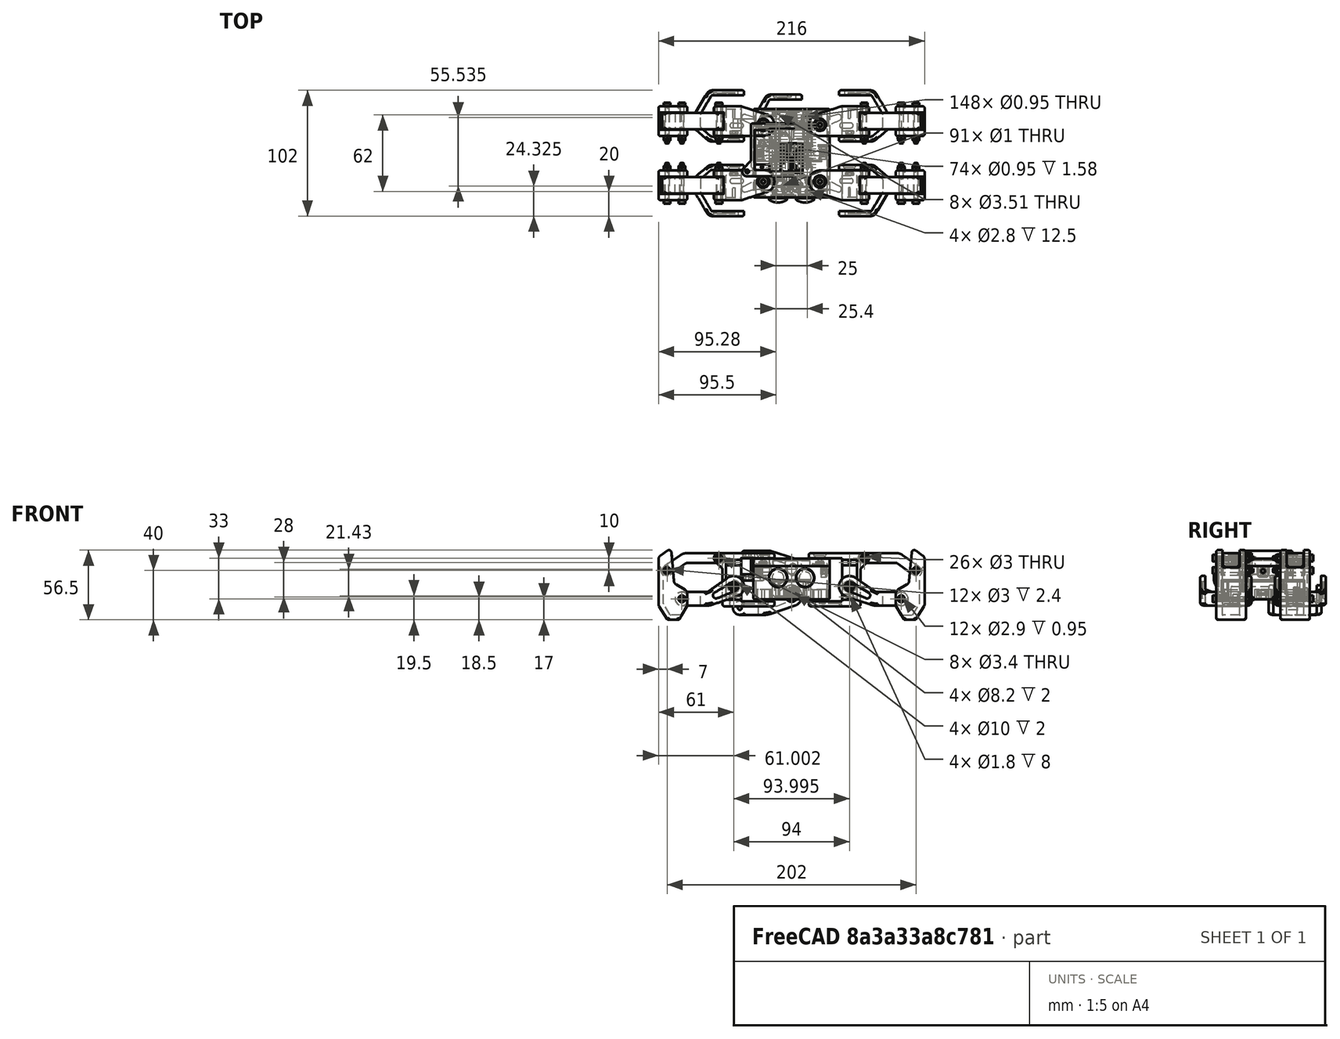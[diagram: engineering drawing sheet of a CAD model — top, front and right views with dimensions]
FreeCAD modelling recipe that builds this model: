
FCSTD DOCUMENT  (FreeCAD 1.0R39109 (Git))
Label: kame32
License: All rights reserved
LicenseURL: http://en.wikipedia.org/wiki/All_rights_reserved
objects: Sketcher::SketchObject×74, Part::FeaturePython×56, PartDesign::Pocket×54, PartDesign::Pad×23, PartDesign::Fillet×20, Part::Feature×14, PartDesign::Body×9, PartDesign::Chamfer×4, App::DocumentObjectGroup×4, PartDesign::Thickness×1, Part::MultiFuse×1, Part::Box×1, Part::Fillet×1, App::Part×1
note: 536 computed .brp shape members not serialized (recipe doc carries the construction recipe); baked Part::Feature solids carry a one-line shape summary decoded from their .brp

FEATURE [Sketcher::SketchObject] Sketch032
  ArcFitTolerance = 0
  AttachmentOffset = pos=(0,-0.5,0) rot=(0,0,1;0rad)
  AttachmentSupport = -> [XZ_Plane001]
  FullyConstrained = true
  MakeInternals = false
  MapMode = 5
  Placement = pos=(0,-1e-16,-0.5) rot=(1,0,0;1.5708rad)
  sketch-geometry (10):
    g0: ArcOfCircle CenterX=-42 CenterY=-10 CenterZ=0 NormalX=0 NormalY=0 NormalZ=1 AngleXU=0 Radius=5.5 StartAngle=1.5708 EndAngle=4.71239
    g1: ArcOfCircle CenterX=0 CenterY=0 CenterZ=0 NormalX=0 NormalY=0 NormalZ=1 AngleXU=0 Radius=8.5 StartAngle=5.03312 EndAngle=8.46485
    g2: LineSegment StartX=-42 StartY=-4.5 StartZ=0 EndX=-21.7189 EndY=-4.5 EndZ=0
    g3: LineSegment StartX=-20.8585 StartY=-4.22873 StartZ=0 EndX=-4.8754 EndY=6.96279 EndZ=0
    g4: LineSegment StartX=2.67968 StartY=-8.06656 StartZ=0 EndX=-17.7782 EndY=-14.8626 EndZ=0
    g5: LineSegment StartX=-21.7189 StartY=-15.5 StartZ=0 EndX=-42 EndY=-15.5 EndZ=0
    g6: Circle CenterX=-42 CenterY=-10 CenterZ=0 NormalX=0 NormalY=0 NormalZ=1 AngleXU=0 Radius=1.7
    g7: Circle CenterX=0 CenterY=0 CenterZ=0 NormalX=0 NormalY=0 NormalZ=1 AngleXU=0 Radius=1.7
    g8: ArcOfCircle CenterX=-21.7189 CenterY=-3 CenterZ=0 NormalX=0 NormalY=0 NormalZ=1 AngleXU=0 Radius=12.5 StartAngle=4.71239 EndAngle=5.03312
    g9: ArcOfCircle CenterX=-21.7189 CenterY=-3 CenterZ=0 NormalX=0 NormalY=0 NormalZ=1 AngleXU=0 Radius=1.5 StartAngle=4.71239 EndAngle=5.32325
  constraints (22):
    c: Tangent(g0,g2) = 1.5708
    c: Tangent(g1,g4) = 1.5708
    c: Horizontal(g5)
    c: Radius(g0) = 5.5
    c: Horizontal(g2)
    c: Tangent(g5,g0) = 1.5708
    c: Coincident(g6,g0)
    c: Radius(g6) = 1.7
    c: Radius(g1) = 8.5
    c: DistanceX(g0,g1) = 42
    c: DistanceY(g0,g1) = 10
    c: Coincident(g7,g1)
    c: Equal(g7,g6)
    c: Tangent(g3,g1) = 1.5708
    c: Coincident(g1,g-1)
    c: Tangent(g8,g5) = 1.5708
    c: Tangent(g8,g4) = 1.5708
    c: Coincident(g9,g8)
    c: Tangent(g9,g3) = -1.5708
    c: Tangent(g9,g2) = -1.5708
    c: Radius(g9) = 1.5
    c: Angle(g3,g2) = 2.53073
FEATURE [PartDesign::Pad] Pad017
  Direction = (0,-1,2e-16)
  Length = 50
  Length2 = 10
  Placement = pos=(0,0,0) rot=(1,0,0;1.5708rad)
  Profile = -> Sketch032
  ReferenceAxis = -> Sketch032 [N_Axis]
  Refine = true
  Reversed = true
  Suppressed = false
  Type = 0
FEATURE [Sketcher::SketchObject] Sketch033
  ArcFitTolerance = 0
  AttachmentSupport = -> [Pad017]
  ExternalGeometry = -> [Pad017]
  FullyConstrained = true
  MakeInternals = false
  MapMode = 5
  Placement = pos=(0,-7e-15,-16) rot=(1,0,0;3.14159rad)
  sketch-geometry (31):
    g0: LineSegment StartX=-54 StartY=-14.25 StartZ=0 EndX=-31.4689 EndY=-14.25 EndZ=0
    g1: LineSegment StartX=-30.8158 StartY=-14.0072 StartZ=0 EndX=-21.7189 EndY=-6.16102 EndZ=0
    g2: LineSegment StartX=-17.25 StartY=-4.5 StartZ=0 EndX=11 EndY=-4.5 EndZ=0
    g3: LineSegment StartX=11 StartY=-4.5 StartZ=0 EndX=11 EndY=-8.5 EndZ=0
    g4: LineSegment StartX=11 StartY=-8.5 StartZ=0 EndX=-17.25 EndY=-8.5 EndZ=0
    g5: LineSegment StartX=-19.1064 StartY=-9.18998 StartZ=0 EndX=-26.6531 EndY=-15.6992 EndZ=0
    g6: LineSegment StartX=-27 StartY=-16.4565 StartZ=0 EndX=-27 EndY=-26.2161 EndZ=0
    g7: LineSegment StartX=-26.8632 StartY=-26.721 StartZ=0 EndX=-18.2663 EndY=-41.4171 EndZ=0
    g8: LineSegment StartX=-17.25 StartY=-42 StartZ=0 EndX=11 EndY=-42 EndZ=0
    g9: LineSegment StartX=11 StartY=-42 StartZ=0 EndX=11 EndY=-46 EndZ=0
    g10: LineSegment StartX=11 StartY=-46 StartZ=0 EndX=-17.25 EndY=-46 EndZ=0
    g11: LineSegment StartX=-21.7189 StartY=-43.4368 StartZ=0 EndX=-30.6058 EndY=-28.2451 EndZ=0
    g12: LineSegment StartX=-31.4689 StartY=-27.75 StartZ=0 EndX=-54 EndY=-27.75 EndZ=0
    g13: LineSegment [constr] StartX=-54 StartY=-27.75 StartZ=0 EndX=-54 EndY=-14.25 EndZ=0
    g14: LineSegment [constr] StartX=11 StartY=-8.5 StartZ=0 EndX=11 EndY=-42 EndZ=0
    g15: ArcOfCircle CenterX=-31.4689 CenterY=-13.25 CenterZ=0 NormalX=0 NormalY=0 NormalZ=1 AngleXU=0 Radius=1 StartAngle=4.71239 EndAngle=5.42411
    g16: ArcOfCircle CenterX=-17.25 CenterY=-11.3422 CenterZ=0 NormalX=0 NormalY=0 NormalZ=1 AngleXU=0 Radius=6.84224 StartAngle=1.5708 EndAngle=2.28251
    g17: ArcOfCircle CenterX=-17.25 CenterY=-11.3422 CenterZ=0 NormalX=0 NormalY=0 NormalZ=1 AngleXU=0 Radius=2.84224 StartAngle=1.5708 EndAngle=2.28251
    g18: ArcOfCircle CenterX=-17.25 CenterY=-40.8226 CenterZ=0 NormalX=0 NormalY=0 NormalZ=1 AngleXU=0 Radius=1.17738 StartAngle=3.67089 EndAngle=4.71239
    g19: ArcOfCircle CenterX=-17.25 CenterY=-40.8226 CenterZ=0 NormalX=0 NormalY=0 NormalZ=1 AngleXU=0 Radius=5.17738 StartAngle=3.67089 EndAngle=4.71239
    g20: ArcOfCircle CenterX=-26 CenterY=-16.4565 CenterZ=0 NormalX=0 NormalY=0 NormalZ=1 AngleXU=0 Radius=1 StartAngle=2.28251 EndAngle=3.14159
    g21: ArcOfCircle CenterX=-26 CenterY=-26.2161 CenterZ=0 NormalX=0 NormalY=0 NormalZ=1 AngleXU=0 Radius=1 StartAngle=3.14159 EndAngle=3.67089
    g22: ArcOfCircle CenterX=-31.4689 CenterY=-28.75 CenterZ=0 NormalX=0 NormalY=0 NormalZ=1 AngleXU=0 Radius=1 StartAngle=0.5293 EndAngle=1.5708
    g23: LineSegment StartX=-54 StartY=-14.25 StartZ=0 EndX=-54 EndY=20 EndZ=0
    g24: LineSegment StartX=-54 StartY=20 StartZ=0 EndX=26 EndY=20 EndZ=0
    g25: LineSegment StartX=26 StartY=-60 StartZ=0 EndX=-54 EndY=-60 EndZ=0
    g26: LineSegment StartX=-54 StartY=-60 StartZ=0 EndX=-54 EndY=-27.75 EndZ=0
    g27: LineSegment StartX=26 StartY=20 StartZ=0 EndX=26 EndY=-60 EndZ=0
    g28: LineSegment [constr] StartX=-31.4689 StartY=-14.25 StartZ=0 EndX=-31.4689 EndY=-27.75 EndZ=0
    g29: LineSegment [constr] StartX=-21.7189 StartY=-6.16102 StartZ=0 EndX=-21.7189 EndY=-43.4368 EndZ=0
    g30: LineSegment [constr] StartX=-17.25 StartY=-4.5 StartZ=0 EndX=-17.25 EndY=-46 EndZ=0
  constraints (80):
    c: Coincident(g25,g26)
    c: Coincident(g12,g26)
    c: Coincident(g0,g23)
    c: Coincident(g23,g24)
    c: Coincident(g4,g17)
    c: Coincident(g2,g16)
    c: Coincident(g9,g10)
    c: Coincident(g8,g9)
    c: Coincident(g3,g4)
    c: Coincident(g2,g3)
    c: Coincident(g25,g27)
    c: Coincident(g24,g27)
    c: Coincident(g0,g13)
    c: Coincident(g12,g13)
    c: Tangent(g7,g18) = -1.5708
    c: Tangent(g11,g19) = 1.5708
    c: Coincident(g18,g19)
    c: Tangent(g8,g18) = -1.5708
    c: Tangent(g10,g19) = 1.5708
    c: Coincident(g16,g17)
    c: Equal(g9,g3)
    c: Distance(g3) = 4
    c: Horizontal(g2)
    c: Horizontal(g4)
    c: Horizontal(g8)
    c: Horizontal(g10)
    c: Horizontal(g12)
    c: Horizontal(g0)
    c: Horizontal(g24)
    c: Horizontal(g25)
    c: Vertical(g23)
    c: Vertical(g13)
    c: Vertical(g26)
    c: Vertical(g6)
    c: Vertical(g3)
    c: Vertical(g9)
    c: Equal(g15,g20)
    c: Equal(g15,g21)
    c: Equal(g15,g22)
    c: Radius(g15) = 1
    c: Tangent(g12,g22) = -1.5708
    c: Tangent(g11,g22) = -1.5708
    c: Tangent(g7,g21) = -1.5708
    c: Tangent(g6,g21) = -1.5708
    c: Tangent(g5,g20) = -1.5708
    c: Tangent(g6,g20) = -1.5708
    c: Tangent(g1,g15) = -1.5708
    c: Tangent(g0,g15) = -1.5708
    c: Tangent(g5,g17) = -1.5708
    c: Tangent(g1,g16) = 1.5708
    c: Parallel(g1,g5)
    c: Parallel(g7,g11)
    c: Distance(g13) = 13.5
    c: Coincident(g3,g14)
    c: Vertical(g14)
    c: Equal(g25,g27)
    c: Distance(g27) = 80
    c: Vertical(g27)
    c: DistanceX(g-2,g23) = -54
    c: DistanceX(g-2,g2) = 11
    c: Distance(g14) = 33.5
    c: Coincident(g14,g8)
    c: Coincident(g28,g0)
    c: Coincident(g28,g12)
    c: Vertical(g28)
    c: DistanceY(g-1,g0) = -14.25
    c: DistanceY(g-1,g3) = -8.5
    c: Distance(g6,g27) = 53
    c: DistanceY(g-1,g23) = 20
    c: Coincident(g29,g1)
    c: Coincident(g29,g11)
    c: Vertical(g29)
    c: Coincident(g30,g2)
    c: Coincident(g30,g10)
    c: Vertical(g30)
    c: PointOnObject(g16,g30)
    c: PointOnObject(g4,g30)
    c: PointOnObject(g1,g-3)
    c: DistanceX(g-2,g2) = -17.25
    c: Distance(g0,g29) = 9.75
FEATURE [PartDesign::Pocket] Pocket012
  BaseFeature = -> Pad017
  Direction = (0,0,1)
  Length = 40
  Length2 = 5
  Placement = pos=(0,0,0) rot=(1,0,0;1.5708rad)
  Profile = -> Sketch033
  ReferenceAxis = -> Sketch033 [N_Axis]
  Refine = true
  Suppressed = false
  Type = 0
FEATURE [Sketcher::SketchObject] Sketch007
  ArcFitTolerance = 0
  FullyConstrained = true
  MakeInternals = false
  MapMode = 5
  Placement = pos=(0,19.25,0) rot=(0,0.707107,0.707107;3.14159rad)
  sketch-geometry (10):
    g0: ArcOfCircle CenterX=12 CenterY=22 CenterZ=0 NormalX=0 NormalY=0 NormalZ=1 AngleXU=0 Radius=4 StartAngle=1.5708 EndAngle=4.71239
    g1: LineSegment StartX=12 StartY=26 StartZ=0 EndX=38.4573 EndY=26 EndZ=0
    g2: LineSegment StartX=43.0459 StartY=24.5532 StartZ=0 EndX=56.2943 EndY=15.2766 EndZ=0
    g3: LineSegment StartX=12 StartY=18 StartZ=0 EndX=37.9844 EndY=18 EndZ=0
    g4: LineSegment StartX=38.8447 StartY=17.7287 StartZ=0 EndX=51.7057 EndY=8.72338 EndZ=0
    g5: ArcOfCircle CenterX=54 CenterY=12 CenterZ=0 NormalX=0 NormalY=0 NormalZ=1 AngleXU=0 Radius=4 StartAngle=4.10153 EndAngle=7.24312
    g6: Circle CenterX=12 CenterY=22 CenterZ=0 NormalX=0 NormalY=0 NormalZ=1 AngleXU=0 Radius=1.7
    g7: Circle CenterX=54 CenterY=12 CenterZ=0 NormalX=0 NormalY=0 NormalZ=1 AngleXU=0 Radius=1.7
    g8: ArcOfCircle CenterX=38.4573 CenterY=18 CenterZ=0 NormalX=0 NormalY=0 NormalZ=1 AngleXU=0 Radius=8 StartAngle=0.959931 EndAngle=1.5708
    g9: ArcOfCircle CenterX=37.9844 CenterY=16.5 CenterZ=0 NormalX=0 NormalY=0 NormalZ=1 AngleXU=0 Radius=1.5 StartAngle=0.959931 EndAngle=1.5708
  constraints (26):
    c: Tangent(g0,g1) = 1.5708
    c: Tangent(g0,g3) = -1.5708
    c: Coincident(g5,g2)
    c: Coincident(g5,g4)
    c: Tangent(g2,g5)
    c: Tangent(g4,g5)
    c: Parallel(g1,g3)
    c: Parallel(g2,g4)
    c: Horizontal(g1)
    c: Radius(g0) = 4
    c: Equal(g0,g5)
    c: Coincident(g6,g0)
    c: Coincident(g7,g5)
    c: Radius(g6) = 1.7
    c: Equal(g6,g7)
    c: Angle(g1,g2) = 2.53073
    c: DistanceY(g0,g5) = -10  'z_length'
    c: DistanceX(g0,g5) = 42  'x_legth'
    c: DistanceX(g-2,g0) = 12
    c: DistanceY(g-1,g0) = 22
    c: Tangent(g1,g8) = 1.5708
    c: Tangent(g2,g8) = 1.5708
    c: Tangent(g3,g9) = 1.5708
    c: Tangent(g4,g9) = 1.5708
    c: Radius(g8) = 8
    c: Radius(g9) = 1.5
FEATURE [PartDesign::Pad] Pad019
  Direction = (1e-16,1,-2e-16)
  Length = 13.5
  Length2 = 10
  Placement = pos=(0,19.25,0) rot=(0,0.707107,0.707107;3.14159rad)
  Profile = -> Sketch007
  ReferenceAxis = -> Sketch007 [N_Axis]
  Refine = true
  Suppressed = false
  Type = 0
FEATURE [PartDesign::Fillet] Fillet006
  Base = -> Pad019 [Edge24,Edge23]
  BaseFeature = -> Pad019
  Placement = pos=(0,19.25,0) rot=(0,0.707107,0.707107;3.14159rad)
  Radius = 1.5
  Refine = true
  SupportTransform = false
  Suppressed = false
  UseAllEdges = false
FEATURE [Sketcher::SketchObject] Sketch035
  ArcFitTolerance = 0
  AttachmentSupport = -> [Fillet006]
  ExternalGeometry = -> [Fillet006]
  FullyConstrained = true
  MakeInternals = false
  MapMode = 5
  Placement = pos=(0,32.75,-4.7e-15) rot=(0,0.707107,0.707107;3.14159rad)
  sketch-geometry (4):
    g0: Circle CenterX=12 CenterY=22 CenterZ=0 NormalX=0 NormalY=0 NormalZ=1 AngleXU=0 Radius=1.7
    g1: Circle CenterX=54 CenterY=12 CenterZ=0 NormalX=0 NormalY=0 NormalZ=1 AngleXU=0 Radius=1.7
    g2: Circle CenterX=54 CenterY=12 CenterZ=0 NormalX=0 NormalY=0 NormalZ=1 AngleXU=0 Radius=4
    g3: Circle CenterX=12 CenterY=22 CenterZ=0 NormalX=0 NormalY=0 NormalZ=1 AngleXU=0 Radius=4
  constraints (8):
    c: Coincident(g0,g-5)
    c: Equal(g-3,g0)
    c: Equal(g-4,g1)
    c: Coincident(g2,g1)
    c: PointOnObject(g-6,g2)
    c: Coincident(g3,g0)
    c: PointOnObject(g-5,g3)
    c: Coincident(g-6,g1)
FEATURE [PartDesign::Pad] Pad020
  BaseFeature = -> Fillet006
  Direction = (0,1,-2e-16)
  Length = 13.5
  Length2 = 10
  Placement = pos=(0,19.25,0) rot=(0,0.707107,0.707107;3.14159rad)
  Profile = -> Sketch035
  ReferenceAxis = -> Sketch035 [N_Axis]
  Refine = true
  Reversed = true
  Suppressed = false
  Type = 0
FEATURE [PartDesign::Body] Body002  label="leg-link"
  AllowCompound = false
  Group = -> [Sketch007,Pad019,Fillet006,Sketch035,Pad020]
  Origin = -> Origin002
  Placement = pos=(0,-5,0) rot=(0,0,1;0rad)
  Tip = -> Pad020
FEATURE [Sketcher::SketchObject] Sketch036
  ArcFitTolerance = 0
  AttachmentSupport = -> [XZ_Plane003]
  FullyConstrained = true
  MakeInternals = false
  MapMode = 5
  Placement = pos=(0,0,0) rot=(1,0,0;1.5708rad)
  sketch-geometry (19):
    g0: Circle CenterX=-54 CenterY=12.5 CenterZ=0 NormalX=0 NormalY=0 NormalZ=1 AngleXU=0 Radius=1.5
    g1: Circle CenterX=-42 CenterY=-10.5 CenterZ=0 NormalX=0 NormalY=0 NormalZ=1 AngleXU=0 Radius=1.5
    g2: LineSegment StartX=-59.2943 StartY=24.6841 StartZ=0 EndX=-53.6472 EndY=28.6383 EndZ=0
    g3: LineSegment StartX=-37.5 StartY=-6.5 StartZ=0 EndX=-37.5 EndY=-14.5 EndZ=0
    g4: LineSegment StartX=-38.041 StartY=-16.5089 StartZ=0 EndX=-44.1353 EndY=-27.0022 EndZ=0
    g5: LineSegment StartX=-45 StartY=-27.5 StartZ=0 EndX=-53 EndY=-27.5 EndZ=0
    g6: LineSegment StartX=-53.8466 StartY=-27.0322 StartZ=0 EndX=-60.3865 EndY=-16.6288 EndZ=0
    g7: LineSegment StartX=-61 StartY=-14.5 StartZ=0 EndX=-61 EndY=21.4075 EndZ=0
    g8: ArcOfCircle CenterX=-52.5 CenterY=27 CenterZ=0 NormalX=0 NormalY=0 NormalZ=1 AngleXU=0 Radius=2 StartAngle=0.0872665 EndAngle=2.18166
    g9: ArcOfCircle CenterX=-41.5 CenterY=-6.5 CenterZ=0 NormalX=0 NormalY=0 NormalZ=1 AngleXU=0 Radius=4 StartAngle=0 EndAngle=1.0472
    g10: ArcOfCircle CenterX=-41.5 CenterY=-14.5 CenterZ=0 NormalX=0 NormalY=0 NormalZ=1 AngleXU=0 Radius=4 StartAngle=5.75703 EndAngle=6.28319
    g11: ArcOfCircle CenterX=-57 CenterY=-14.5 CenterZ=0 NormalX=0 NormalY=0 NormalZ=1 AngleXU=0 Radius=4 StartAngle=3.14159 EndAngle=3.7028
    g12: ArcOfCircle CenterX=-57 CenterY=21.4075 CenterZ=0 NormalX=0 NormalY=0 NormalZ=1 AngleXU=0 Radius=4 StartAngle=2.18166 EndAngle=3.14159
    g13: ArcOfCircle CenterX=-45 CenterY=-26.5 CenterZ=0 NormalX=0 NormalY=0 NormalZ=1 AngleXU=0 Radius=1 StartAngle=4.71239 EndAngle=5.75703
    g14: ArcOfCircle CenterX=-53 CenterY=-26.5 CenterZ=0 NormalX=0 NormalY=0 NormalZ=1 AngleXU=0 Radius=1 StartAngle=3.7028 EndAngle=4.71239
    g15: LineSegment StartX=-50.5076 StartY=27.1743 StartZ=0 EndX=-48.491 EndY=4.12464 EndZ=0
    g16: LineSegment StartX=-39.5 StartY=-3.0359 StartZ=0 EndX=-46.5062 EndY=1.00916 EndZ=0
    g17: ArcOfCircle CenterX=-44.5062 CenterY=4.47326 CenterZ=0 NormalX=0 NormalY=0 NormalZ=1 AngleXU=0 Radius=4 StartAngle=3.22886 EndAngle=4.18879
    g18: LineSegment [constr] StartX=-61 StartY=-14.5 StartZ=0 EndX=-37.5 EndY=-14.5 EndZ=0
  constraints (48):
    c: Equal(g1,g0)
    c: Radius(g1) = 1.5
    c: DistanceX(g0,g1) = 12
    c: Vertical(g3)
    c: Horizontal(g5)
    c: Vertical(g7)
    c: Tangent(g2,g8) = 1.5708
    c: Tangent(g3,g9) = 1.5708
    c: Tangent(g3,g10) = 1.5708
    c: Tangent(g4,g10) = 1.5708
    c: Tangent(g6,g11) = 1.5708
    c: Tangent(g7,g11) = 1.5708
    c: Tangent(g2,g12) = 1.5708
    c: Tangent(g7,g12) = 1.5708
    c: Tangent(g5,g13) = 1.5708
    c: Tangent(g4,g13) = 1.5708
    c: Tangent(g6,g14) = 1.5708
    c: Tangent(g5,g14) = 1.5708
    c: Equal(g14,g13)
    c: Radius(g14) = 1
    c: Distance(g5) = 8
    c: Distance(g3,g7) = 23.5
    c: Angle(g-1,g2) = 0.610865
    c: Radius(g8) = 2
    c: Distance(g3) = 8
    c: Distance(g0,g7) = 7
    c: Tangent(g15,g17) = -1.5708
    c: Tangent(g16,g17) = 1.5708
    c: Tangent(g15,g8) = 1.5708
    c: Tangent(g16,g9) = -1.5708
    c: DistanceX(g5,g1) = 3
    c: Coincident(g18,g7)
    c: Coincident(g18,g3)
    c: Horizontal(g18)
    c: Equal(g10,g11)
    c: Equal(g11,g9)
    c: Radius(g9) = 4
    c: Equal(g17,g12)
    c: Angle(g-1,g15) = 1.65806
    c: Angle(g-1,g16) = 2.61799
    c: DistanceX(g0,g8) = 1.5
    c: Equal(g9,g17)
    c: DistanceX(g-2,g1) = -42
    c: DistanceY(g-1,g0) = 12.5
    c: DistanceY(g-1,g8) = 27
    c: DistanceY(g-1,g5) = -27.5
    c: DistanceY(g-1,g11) = -14.5
    c: DistanceY(g-1,g1) = -10.5
FEATURE [PartDesign::Pad] Pad021
  Direction = (0,-1,2e-16)
  Length = 24
  Length2 = 10
  Placement = pos=(0,0,0) rot=(1,0,0;1.5708rad)
  Profile = -> Sketch036
  ReferenceAxis = -> Sketch036 [N_Axis]
  Refine = true
  Suppressed = false
  Type = 0
FEATURE [PartDesign::Fillet] Fillet007
  Base = -> Pad021 [Edge6,Edge7]
  BaseFeature = -> Pad021
  Placement = pos=(0,0,0) rot=(1,0,0;1.5708rad)
  Radius = 1.5
  Refine = true
  SupportTransform = false
  Suppressed = false
  UseAllEdges = false
FEATURE [Sketcher::SketchObject] Sketch037
  ArcFitTolerance = 0
  AttachmentOffset = pos=(0,0,-5) rot=(0,0,1;0rad)
  AttachmentSupport = -> [Fillet007]
  ExternalGeometry = -> [Fillet007]
  FullyConstrained = true
  MakeInternals = false
  MapMode = 5
  Placement = pos=(0,-19,4.2e-15) rot=(1,0,0;1.5708rad)
  sketch-geometry (15):
    g0: LineSegment StartX=-37.4756 StartY=-23.5 StartZ=0 EndX=-51.3424 EndY=-23.5 EndZ=0
    g1: LineSegment StartX=-51.3424 StartY=-23.5 StartZ=0 EndX=-57 EndY=-14.5 EndZ=0
    g2: LineSegment StartX=-57 StartY=-14.5 StartZ=0 EndX=-57 EndY=8.5 EndZ=0
    g3: LineSegment StartX=-79 StartY=15 StartZ=0 EndX=-79 EndY=35 EndZ=0
    g4: LineSegment StartX=-79 StartY=35 StartZ=0 EndX=-15.7333 EndY=35 EndZ=0
    g5: LineSegment StartX=-15.7333 StartY=35 StartZ=0 EndX=-15.7333 EndY=-20.5 EndZ=0
    g6: LineSegment StartX=-15.7333 StartY=-20.5 StartZ=0 EndX=-35.7333 EndY=-20.5 EndZ=0
    g7: LineSegment StartX=-35.7333 StartY=-20.5 StartZ=0 EndX=-37.4756 EndY=-23.5 EndZ=0
    g8: LineSegment [constr] StartX=-51.3424 StartY=-23.5 StartZ=0 EndX=-54.7288 EndY=-25.6288 EndZ=0
    g9: LineSegment [constr] StartX=-51.3424 StartY=-23.5 StartZ=0 EndX=-51.3424 EndY=-27.5 EndZ=0
    g10: LineSegment [constr] StartX=-37.4756 StartY=-23.5 StartZ=0 EndX=-40.9346 EndY=-21.4911 EndZ=0
    g11: LineSegment [constr] StartX=-61 StartY=-14.5 StartZ=0 EndX=-57 EndY=-14.5 EndZ=0
    g12: ArcOfCircle CenterX=-54 CenterY=12.5 CenterZ=0 NormalX=0 NormalY=0 NormalZ=1 AngleXU=0 Radius=5 StartAngle=3.14159 EndAngle=4.06889
    g13: LineSegment StartX=-59 StartY=12.5 StartZ=0 EndX=-59 EndY=15 EndZ=0
    g14: LineSegment StartX=-59 StartY=15 StartZ=0 EndX=-79 EndY=15 EndZ=0
  constraints (44):
    c: Horizontal(g0)
    c: Coincident(g0,g1)
    c: Coincident(g1,g2)
    c: Vertical(g2)
    c: Vertical(g3)
    c: Coincident(g3,g4)
    c: Horizontal(g4)
    c: Coincident(g4,g5)
    c: Vertical(g5)
    c: Coincident(g5,g6)
    c: Horizontal(g6)
    c: Coincident(g6,g7)
    c: Coincident(g7,g0)
    c: Parallel(g1,g-7)
    c: Coincident(g8,g0)
    c: PointOnObject(g8,g-7)
    c: Coincident(g9,g0)
    c: PointOnObject(g9,g-9)
    c: Vertical(g9)
    c: Coincident(g10,g0)
    c: PointOnObject(g10,g-11)
    c: Coincident(g11,g-6)
    c: PointOnObject(g11,g2)
    c: Horizontal(g11)
    c: Equal(g11,g8)
    c: Equal(g8,g9)
    c: Equal(g9,g10)
    c: Perpendicular(g-7,g8)
    c: Perpendicular(g-11,g10)
    c: Parallel(g7,g-11)
    c: Distance(g11) = 4
    c: DistanceY(g-10,g6) = 7
    c: Coincident(g12,g-12)
    c: Coincident(g12,g2)
    c: Tangent(g12,g13) = 1.5708
    c: Coincident(g13,g14)
    c: Horizontal(g14)
    c: Coincident(g14,g3)
    c: Radius(g12) = 5
    c: Distance(g6) = 20
    c: Distance(g14) = 20
    c: Distance(g3) = 20
    c: Vertical(g13)
    c: DistanceY(g-9,g13) = 42.5
FEATURE [PartDesign::Pocket] Pocket013
  BaseFeature = -> Fillet007
  Direction = (0,1,-2e-16)
  Length = 14
  Length2 = 5
  Placement = pos=(0,0,0) rot=(1,0,0;1.5708rad)
  Profile = -> Sketch037
  ReferenceAxis = -> Sketch037 [N_Axis]
  Refine = true
  Suppressed = false
  Type = 0
FEATURE [PartDesign::Fillet] Fillet008
  Base = -> Pocket013 [Edge79,Edge33,Edge80,Edge81,Edge82]
  BaseFeature = -> Pocket013
  Placement = pos=(0,0,0) rot=(1,0,0;1.5708rad)
  Radius = 0.5
  Refine = true
  SupportTransform = false
  Suppressed = false
  UseAllEdges = false
FEATURE [PartDesign::Body] Body003  label="foot"
  AllowCompound = false
  Group = -> [Sketch036,Pad021,Fillet007,Sketch037,Pocket013,Fillet008]
  Origin = -> Origin003
  Placement = pos=(0,33,0) rot=(0,0,1;0rad)
  Tip = -> Fillet008
FEATURE [Sketcher::SketchObject] Sketch056
  ArcFitTolerance = 0
  AttachmentSupport = -> [XY_Plane006]
  FullyConstrained = true
  MakeInternals = false
  MapMode = 5
  sketch-geometry (5):
    g0: ArcOfCircle CenterX=0 CenterY=0 CenterZ=0 NormalX=0 NormalY=0 NormalZ=1 AngleXU=0 Radius=9 StartAngle=4.71239 EndAngle=7.5465
    g1: LineSegment StartX=2.72391 StartY=8.5779 StartZ=0 EndX=-17.5 EndY=15 EndZ=0
    g2: LineSegment StartX=-17.5 StartY=15 StartZ=0 EndX=-33 EndY=15 EndZ=0
    g3: LineSegment StartX=-33 StartY=15 StartZ=0 EndX=-33 EndY=-9 EndZ=0
    g4: LineSegment StartX=-33 StartY=-9 StartZ=0 EndX=0 EndY=-9 EndZ=0
  constraints (13):
    c: Coincident(g0,g-1)
    c: Tangent(g0,g1) = -1.5708
    c: Coincident(g1,g2)
    c: Horizontal(g2)
    c: Coincident(g2,g3)
    c: Vertical(g3)
    c: Coincident(g3,g4)
    c: Horizontal(g4)
    c: Tangent(g4,g0) = -1.5708
    c: Radius(g0) = 9
    c: Distance(g3) = 24
    c: Distance(g4) = 33
    c: Distance(g2) = 15.5
FEATURE [PartDesign::Pad] Pad025
  Direction = (0,0,1)
  Length = 43
  Length2 = 10
  Profile = -> Sketch056
  ReferenceAxis = -> Sketch056 [N_Axis]
  Refine = true
  Suppressed = false
  Type = 0
FEATURE [Sketcher::SketchObject] Sketch057
  ArcFitTolerance = 0
  AttachmentSupport = -> [Pad025]
  ExternalGeometry = -> [Pad025]
  FullyConstrained = false
  MakeInternals = false
  MapMode = 5
  Placement = pos=(0,-9,0) rot=(1,0,0;1.5708rad)
  sketch-geometry (5):
    g0: Circle CenterX=-35.9977 CenterY=39 CenterZ=0 NormalX=0 NormalY=0 NormalZ=1 AngleXU=0 Radius=1.5
    g1: ArcOfCircle CenterX=-35.9977 CenterY=39 CenterZ=0 NormalX=0 NormalY=0 NormalZ=1 AngleXU=0 Radius=4 StartAngle=1.57403 EndAngle=3.9468
    g2: LineSegment StartX=-36.0107 StartY=43 StartZ=0 EndX=-33 EndY=43 EndZ=0
    g3: LineSegment StartX=-33 StartY=43 StartZ=0 EndX=-33 EndY=30.3465 EndZ=0
    g4: LineSegment StartX=-38.7696 StartY=36.1161 StartZ=0 EndX=-33 EndY=30.3465 EndZ=0
  constraints (11):
    c: Coincident(g1,g0)
    c: Coincident(g2,g1)
    c: Coincident(g2,g-3)
    c: Horizontal(g2)
    c: Coincident(g3,g2)
    c: Vertical(g3)
    c: Coincident(g4,g1)
    c: Coincident(g4,g3)
    c: Angle(g3,g4) = 0.785398
    c: Radius(g1) = 4
    c: Radius(g0) = 1.5
FEATURE [PartDesign::Pad] Pad026
  BaseFeature = -> Pad025
  Direction = (0,-1,2e-16)
  Length = 24
  Length2 = 10
  Profile = -> Sketch057
  ReferenceAxis = -> Sketch057 [N_Axis]
  Refine = true
  Reversed = true
  Suppressed = false
  Type = 0
FEATURE [Sketcher::SketchObject] Sketch058
  ArcFitTolerance = 0
  AttachmentSupport = -> [Pad026]
  FullyConstrained = true
  MakeInternals = false
  MapMode = 5
  Placement = pos=(0,-9,0) rot=(1,0,0;1.5708rad)
  sketch-geometry (4):
    g0: LineSegment StartX=-18 StartY=4 StartZ=0 EndX=18 EndY=4 EndZ=0
    g1: LineSegment StartX=18 StartY=4 StartZ=0 EndX=18 EndY=39 EndZ=0
    g2: LineSegment StartX=18 StartY=39 StartZ=0 EndX=-18 EndY=39 EndZ=0
    g3: LineSegment StartX=-18 StartY=39 StartZ=0 EndX=-18 EndY=4 EndZ=0
  constraints (12):
    c: Coincident(g0,g1)
    c: Coincident(g1,g2)
    c: Coincident(g2,g3)
    c: Coincident(g3,g0)
    c: Horizontal(g0)
    c: Horizontal(g2)
    c: Vertical(g1)
    c: Vertical(g3)
    c: DistanceX(g-2,g2) = -18
    c: Distance(g3) = 35
    c: DistanceY(g-1,g0) = 4
    c: Distance(g2) = 36
FEATURE [PartDesign::Pocket] Pocket027
  BaseFeature = -> Pad026
  Direction = (0,1,-2e-16)
  Length = 30
  Length2 = 5
  Profile = -> Sketch058
  ReferenceAxis = -> Sketch058 [N_Axis]
  Refine = true
  Suppressed = false
  Type = 0
FEATURE [Sketcher::SketchObject] Sketch059
  ArcFitTolerance = 1e-06
  AttachmentSupport = -> [Pocket027]
  ExternalGeometry = -> [Pocket027]
  FullyConstrained = true
  MakeInternals = false
  MapMode = 5
  Placement = pos=(0,-9,0) rot=(1,0,0;1.5708rad)
  sketch-geometry (1):
    g0: Circle CenterX=-23.9977 CenterY=16 CenterZ=0 NormalX=0 NormalY=0 NormalZ=1 AngleXU=0 Radius=1.5
  constraints (3):
    c: DistanceX(g-3,g0) = 12
    c: DistanceY(g0,g-3) = 23
    c: Radius(g0) = 1.5
FEATURE [PartDesign::Pocket] Pocket028
  BaseFeature = -> Pocket027
  Direction = (0,1,-2e-16)
  Length = 35
  Length2 = 5
  Profile = -> Sketch059
  ReferenceAxis = -> Sketch059 [N_Axis]
  Refine = true
  Suppressed = false
  Type = 0
FEATURE [Sketcher::SketchObject] Sketch060
  ArcFitTolerance = 1e-06
  AttachmentSupport = -> [Pocket028]
  ExternalGeometry = -> [Pocket028]
  FullyConstrained = true
  MakeInternals = false
  MapMode = 5
  Placement = pos=(0,15,0) rot=(0,0.707107,0.707107;3.14159rad)
  sketch-geometry (4):
    g0: LineSegment StartX=18 StartY=33.2 StartZ=0 EndX=18 EndY=9.80002 EndZ=0
    g1: LineSegment StartX=18 StartY=9.80002 StartZ=0 EndX=30.2 EndY=9.80002 EndZ=0
    g2: LineSegment StartX=30.2 StartY=9.80002 StartZ=0 EndX=30.2 EndY=33.2 EndZ=0
    g3: LineSegment StartX=30.2 StartY=33.2 StartZ=0 EndX=18 EndY=33.2 EndZ=0
  constraints (12):
    c: Coincident(g0,g1)
    c: Coincident(g1,g2)
    c: Coincident(g2,g3)
    c: Coincident(g3,g0)
    c: Vertical(g0)
    c: Vertical(g2)
    c: Horizontal(g1)
    c: Horizontal(g3)
    c: PointOnObject(g0,g-3)
    c: Distance(g1) = 12.2
    c: Distance(g2) = 23.4
    c: Distance(g-4,g1) = 6.2
FEATURE [PartDesign::Pocket] Pocket029
  BaseFeature = -> Pocket028
  Direction = (0,-1,2e-16)
  Length = 20
  Length2 = 5
  Profile = -> Sketch060
  ReferenceAxis = -> Sketch060 [N_Axis]
  Refine = true
  Suppressed = false
  Type = 0
FEATURE [Sketcher::SketchObject] Sketch061
  ArcFitTolerance = 1e-06
  AttachmentSupport = -> [Pocket029]
  ExternalGeometry = -> [Pocket029]
  FullyConstrained = true
  MakeInternals = false
  MapMode = 5
  Placement = pos=(0,15,0) rot=(0,0.707107,0.707107;3.14159rad)
  sketch-geometry (6):
    g0: LineSegment StartX=30.2 StartY=37.7 StartZ=0 EndX=30.2 EndY=33.2 EndZ=0
    g1: LineSegment StartX=30.2 StartY=33.2 StartZ=0 EndX=30.2 EndY=9.80002 EndZ=0
    g2: LineSegment StartX=30.2 StartY=9.80002 StartZ=0 EndX=30.2 EndY=5.30002 EndZ=0
    g3: LineSegment StartX=30.2 StartY=5.30002 StartZ=0 EndX=18 EndY=5.30002 EndZ=0
    g4: LineSegment StartX=18 StartY=5.30002 StartZ=0 EndX=18 EndY=37.7 EndZ=0
    g5: LineSegment StartX=18 StartY=37.7 StartZ=0 EndX=30.2 EndY=37.7 EndZ=0
  constraints (16):
    c: Vertical(g0)
    c: Coincident(g0,g1)
    c: Coincident(g1,g2)
    c: Vertical(g2)
    c: Coincident(g2,g3)
    c: Horizontal(g3)
    c: Coincident(g3,g4)
    c: Vertical(g4)
    c: Coincident(g4,g5)
    c: Coincident(g5,g0)
    c: Horizontal(g5)
    c: Equal(g0,g2)
    c: Coincident(g0,g-3)
    c: PointOnObject(g-3,g4)
    c: Distance(g4) = 32.4
    c: Coincident(g-4,g1)
FEATURE [PartDesign::Pocket] Pocket030
  BaseFeature = -> Pocket029
  Direction = (0,-1,2e-16)
  Length = 2
  Length2 = 5
  Profile = -> Sketch061
  ReferenceAxis = -> Sketch061 [N_Axis]
  Refine = true
  Suppressed = false
  Type = 0
FEATURE [Sketcher::SketchObject] Sketch062
  ArcFitTolerance = 1e-06
  AttachmentSupport = -> [Pocket030]
  ExternalGeometry = -> [Pocket030]
  FullyConstrained = true
  MakeInternals = false
  MapMode = 5
  Placement = pos=(0,13,0) rot=(0,0.707107,0.707107;3.14159rad)
  sketch-geometry (5):
    g0: Circle CenterX=23.9977 CenterY=35.5 CenterZ=0 NormalX=0 NormalY=0 NormalZ=1 AngleXU=0 Radius=0.9
    g1: Circle CenterX=23.9977 CenterY=7.50002 CenterZ=0 NormalX=0 NormalY=0 NormalZ=1 AngleXU=0 Radius=0.9
    g2: LineSegment [constr] StartX=23.9977 StartY=7.50002 StartZ=0 EndX=23.9977 EndY=9.80002 EndZ=0
    g3: LineSegment [constr] StartX=23.9977 StartY=9.80002 StartZ=0 EndX=23.9977 EndY=33.2 EndZ=0
    g4: LineSegment [constr] StartX=23.9977 StartY=33.2 StartZ=0 EndX=23.9977 EndY=35.5 EndZ=0
  constraints (14):
    c: Coincident(g2,g1)
    c: PointOnObject(g2,g-4)
    c: Coincident(g3,g2)
    c: PointOnObject(g3,g-3)
    c: Vertical(g3)
    c: Coincident(g4,g3)
    c: Coincident(g4,g0)
    c: Vertical(g4)
    c: Vertical(g2)
    c: Equal(g2,g4)
    c: PointOnObject(g-5,g3)
    c: Distance(g1,g0) = 28
    c: Equal(g1,g0)
    c: Radius(g0) = 0.9
FEATURE [PartDesign::Pocket] Pocket031
  BaseFeature = -> Pocket030
  Direction = (0,-1,2e-16)
  Length = 8
  Length2 = 5
  Profile = -> Sketch062
  ReferenceAxis = -> Sketch062 [N_Axis]
  Refine = true
  Suppressed = false
  Type = 0
FEATURE [Sketcher::SketchObject] Sketch063
  ArcFitTolerance = 1e-06
  AttachmentOffset = pos=(0,0,-5) rot=(0,0,1;0rad)
  AttachmentSupport = -> [Pocket031]
  ExternalGeometry = -> [Pocket031]
  FullyConstrained = true
  MakeInternals = false
  MapMode = 5
  Placement = pos=(0,10,1.1e-15) rot=(0,0.707107,0.707107;3.14159rad)
  sketch-geometry (1):
    g0: Circle CenterX=35.9977 CenterY=39 CenterZ=0 NormalX=0 NormalY=0 NormalZ=1 AngleXU=0 Radius=5
  constraints (2):
    c: Coincident(g0,g-3)
    c: Radius(g0) = 5
FEATURE [PartDesign::Pocket] Pocket032
  BaseFeature = -> Pocket031
  Direction = (0,-1,2e-16)
  Length = 14
  Length2 = 5
  Profile = -> Sketch063
  ReferenceAxis = -> Sketch063 [N_Axis]
  Refine = true
  Suppressed = false
  Type = 0
FEATURE [Sketcher::SketchObject] Sketch064
  ArcFitTolerance = 1e-06
  AttachmentSupport = -> [Pocket032]
  ExternalGeometry = -> [Pocket032]
  FullyConstrained = true
  MakeInternals = false
  MapMode = 5
  Placement = pos=(0,-5,1.1e-15) rot=(0,0.707107,0.707107;3.14159rad)
  sketch-geometry (7):
    g0: LineSegment StartX=22.41 StartY=18.75 StartZ=0 EndX=20.8223 EndY=16 EndZ=0
    g1: LineSegment StartX=20.8223 StartY=16 StartZ=0 EndX=22.41 EndY=13.25 EndZ=0
    g2: LineSegment StartX=22.41 StartY=13.25 StartZ=0 EndX=25.5855 EndY=13.25 EndZ=0
    g3: LineSegment StartX=25.5855 StartY=13.25 StartZ=0 EndX=27.1732 EndY=16 EndZ=0
    g4: LineSegment StartX=27.1732 StartY=16 StartZ=0 EndX=25.5855 EndY=18.75 EndZ=0
    g5: LineSegment StartX=25.5855 StartY=18.75 StartZ=0 EndX=22.41 EndY=18.75 EndZ=0
    g6: Circle [constr] CenterX=23.9977 CenterY=16 CenterZ=0 NormalX=0 NormalY=0 NormalZ=1 AngleXU=0 Radius=3.17543
  constraints (16):
    c: Coincident(g0,g1)
    c: Coincident(g1,g2)
    c: Coincident(g2,g3)
    c: Coincident(g3,g4)
    c: Coincident(g4,g5)
    c: Coincident(g5,g0)
    c: Equal(g0, g1-g5) x5
    c: PointOnObject(g0,g6)
    c: PointOnObject(g1,g6)
    c: PointOnObject(g2,g6)
    c: PointOnObject(g3,g6)
    c: PointOnObject(g4,g6)
    c: PointOnObject(g5,g6)
    c: Coincident(g6,g-3)
    c: Horizontal(g5)
    c: Distance(g0,g1) = 5.5
FEATURE [PartDesign::Pocket] Pocket033
  BaseFeature = -> Pocket032
  Direction = (0,-1,2e-16)
  Length = 2
  Length2 = 5
  Profile = -> Sketch064
  ReferenceAxis = -> Sketch064 [N_Axis]
  Refine = true
  Suppressed = false
  Type = 0
FEATURE [PartDesign::Fillet] Fillet012
  Base = -> Pocket033 [Edge67,Edge64,Edge52,Edge46]
  BaseFeature = -> Pocket033
  Radius = 0.5
  Refine = true
  SupportTransform = false
  Suppressed = false
  UseAllEdges = false
FEATURE [Sketcher::SketchObject] Sketch065
  ArcFitTolerance = 1e-06
  AttachmentSupport = -> [Fillet012]
  ExternalGeometry = -> [Fillet012]
  FullyConstrained = true
  MakeInternals = false
  MapMode = 5
  Placement = pos=(0,0,0) rot=(1,0,0;3.14159rad)
  sketch-geometry (4):
    g0: ArcOfCircle CenterX=-25 CenterY=0.5 CenterZ=0 NormalX=0 NormalY=0 NormalZ=1 AngleXU=0 Radius=2 StartAngle=1.5708 EndAngle=4.71239
    g1: ArcOfCircle CenterX=-18 CenterY=0.5 CenterZ=0 NormalX=0 NormalY=0 NormalZ=1 AngleXU=0 Radius=2 StartAngle=4.71239 EndAngle=7.85398
    g2: LineSegment StartX=-25 StartY=2.5 StartZ=0 EndX=-18 EndY=2.5 EndZ=0
    g3: LineSegment StartX=-25 StartY=-1.5 StartZ=0 EndX=-18 EndY=-1.5 EndZ=0
  constraints (10):
    c: Tangent(g0,g2) = 1.5708
    c: Tangent(g0,g3) = -1.5708
    c: Tangent(g1,g2) = 1.5708
    c: Tangent(g1,g3) = -1.5708
    c: Equal(g0,g1)
    c: Horizontal(g2)
    c: Distance(g0,g-3) = 2.5
    c: Radius(g1) = 2
    c: Distance(g3) = 7
    c: DistanceX(g-2,g0) = -25
FEATURE [PartDesign::Pocket] Pocket034
  BaseFeature = -> Fillet012
  Direction = (0,0,1)
  Length = 10
  Length2 = 5
  Profile = -> Sketch065
  ReferenceAxis = -> Sketch065 [N_Axis]
  Refine = true
  Suppressed = false
  Type = 0
FEATURE [Sketcher::SketchObject] Sketch066
  ArcFitTolerance = 1e-06
  AttachmentSupport = -> [Pocket034]
  FullyConstrained = true
  MakeInternals = false
  MapMode = 5
  Placement = pos=(0,0,0) rot=(1,0,0;3.14159rad)
  sketch-geometry (1):
    g0: Circle CenterX=0 CenterY=0 CenterZ=0 NormalX=0 NormalY=0 NormalZ=1 AngleXU=0 Radius=3.75
  constraints (2):
    c: Coincident(g0,g-1)
    c: Diameter(g0) = 7.5
FEATURE [PartDesign::Pocket] Pocket035
  BaseFeature = -> Pocket034
  Direction = (0,0,1)
  Length = 9
  Length2 = 5
  Profile = -> Sketch066
  ReferenceAxis = -> Sketch066 [N_Axis]
  Refine = true
  Suppressed = false
  Type = 0
FEATURE [Sketcher::SketchObject] Sketch067
  ArcFitTolerance = 1e-06
  AttachmentSupport = -> [Pocket035]
  ExternalGeometry = -> [Pocket035]
  FullyConstrained = true
  MakeInternals = false
  MapMode = 5
  Placement = pos=(0,0,0) rot=(1,0,0;3.14159rad)
  sketch-geometry (7):
    g0: ArcOfCircle CenterX=-14.9681 CenterY=-6.06462 CenterZ=0 NormalX=0 NormalY=0 NormalZ=1 AngleXU=0 Radius=2.5 StartAngle=2.03323 EndAngle=5.01987
    g1: LineSegment StartX=-16.0834 StartY=-3.82719 StartZ=0 EndX=-1.67297 EndY=3.35614 EndZ=0
    g2: LineSegment StartX=-14.2114 StartY=-8.44737 StartZ=0 EndX=1.13496 EndY=-3.57412 EndZ=0
    g3: ArcOfCircle CenterX=0 CenterY=0 CenterZ=0 NormalX=0 NormalY=0 NormalZ=1 AngleXU=0 Radius=3.75 StartAngle=5.01987 EndAngle=8.31641
    g4: LineSegment [constr] StartX=-14.9681 StartY=-6.06462 StartZ=0 EndX=-17.2851 EndY=-7.00341 EndZ=0
    g5: LineSegment [constr] StartX=-14.9681 StartY=-6.06462 StartZ=0 EndX=0 EndY=0 EndZ=0
    g6: LineSegment [constr] StartX=0 StartY=0 StartZ=0 EndX=3.47556 EndY=1.40819 EndZ=0
  constraints (17):
    c: Coincident(g3,g-1)
    c: Tangent(g3,g1) = 1.5708
    c: Tangent(g1,g0) = 1.5708
    c: Tangent(g2,g0) = -1.5708
    c: Tangent(g3,g2) = -1.5708
    c: Coincident(g4,g0)
    c: PointOnObject(g4,g0)
    c: Coincident(g5,g0)
    c: Coincident(g5,g3)
    c: Coincident(g6,g3)
    c: PointOnObject(g6,g3)
    c: Parallel(g6,g5)
    c: Parallel(g5,g4)
    c: Equal(g3,g-3)
    c: Distance(g4,g6) = 22.4
    c: Radius(g0) = 2.5
    c: Parallel(g2,g-4)
FEATURE [PartDesign::Pocket] Pocket036
  BaseFeature = -> Pocket035
  Direction = (0,0,1)
  Length = 2
  Length2 = 5
  Profile = -> Sketch067
  ReferenceAxis = -> Sketch067 [N_Axis]
  Refine = true
  Suppressed = false
  Type = 0
FEATURE [Sketcher::SketchObject] Sketch068
  ArcFitTolerance = 1e-06
  AttachmentSupport = -> [Pocket036]
  ExternalGeometry = -> [Pocket036]
  FullyConstrained = true
  MakeInternals = false
  MapMode = 5
  Placement = pos=(0,0,43) rot=(0,0,1;0rad)
  sketch-geometry (1):
    g0: Circle CenterX=0 CenterY=0 CenterZ=0 NormalX=0 NormalY=0 NormalZ=1 AngleXU=0 Radius=4.1
  constraints (2):
    c: Coincident(g0,g-1)
    c: Radius(g0) = 4.1
FEATURE [PartDesign::Pocket] Pocket037
  BaseFeature = -> Pocket036
  Direction = (0,0,-1)
  Length = 7
  Length2 = 5
  Profile = -> Sketch068
  ReferenceAxis = -> Sketch068 [N_Axis]
  Refine = true
  Suppressed = false
  Type = 0
FEATURE [Sketcher::SketchObject] Sketch069
  ArcFitTolerance = 1e-06
  AttachmentSupport = -> [Pocket037]
  FullyConstrained = true
  MakeInternals = false
  MapMode = 5
  Placement = pos=(0,0,43) rot=(0,0,1;0rad)
  sketch-geometry (1):
    g0: Circle CenterX=0 CenterY=0 CenterZ=0 NormalX=0 NormalY=0 NormalZ=1 AngleXU=0 Radius=5
  constraints (2):
    c: Coincident(g0,g-1)
    c: Radius(g0) = 5
FEATURE [PartDesign::Pocket] Pocket038
  BaseFeature = -> Pocket037
  Direction = (0,0,-1)
  Length = 2
  Length2 = 5
  Profile = -> Sketch069
  ReferenceAxis = -> Sketch069 [N_Axis]
  Refine = true
  Suppressed = false
  Type = 0
FEATURE [PartDesign::Fillet] Fillet013
  Base = -> Pocket038 [Edge85,Edge45,Edge47,Edge7,Edge14,Edge16,Edge9,Edge11,Edge64,Edge65,Edge51]
  BaseFeature = -> Pocket038
  Radius = 1.5
  Refine = true
  SupportTransform = false
  Suppressed = false
  UseAllEdges = false
FEATURE [Sketcher::SketchObject] Sketch070
  ArcFitTolerance = 1e-06
  AttachmentSupport = -> [Fillet013]
  ExternalGeometry = -> [Fillet013]
  FullyConstrained = true
  MakeInternals = false
  MapMode = 5
  Placement = pos=(0,0,0) rot=(1,0,0;3.14159rad)
  sketch-geometry (4):
    g0: LineSegment StartX=-43 StartY=4 StartZ=0 EndX=-43 EndY=-10 EndZ=0
    g1: LineSegment StartX=-43 StartY=-10 StartZ=0 EndX=-33 EndY=-10 EndZ=0
    g2: LineSegment StartX=-33 StartY=-10 StartZ=0 EndX=-33 EndY=4 EndZ=0
    g3: LineSegment StartX=-33 StartY=4 StartZ=0 EndX=-43 EndY=4 EndZ=0
  constraints (12):
    c: Coincident(g0,g1)
    c: Coincident(g1,g2)
    c: Coincident(g2,g3)
    c: Coincident(g3,g0)
    c: Vertical(g0)
    c: Vertical(g2)
    c: Horizontal(g1)
    c: Horizontal(g3)
    c: PointOnObject(g1,g-3)
    c: PointOnObject(g-4,g1)
    c: PointOnObject(g-4,g3)
    c: Distance(g3) = 10
FEATURE [PartDesign::Pocket] Pocket039
  BaseFeature = -> Fillet013
  Direction = (0,0,1)
  Length = 36
  Length2 = 5
  Profile = -> Sketch070
  ReferenceAxis = -> Sketch070 [N_Axis]
  Refine = true
  Suppressed = false
  Type = 0
FEATURE [PartDesign::Fillet] Fillet014
  Base = -> Pocket039 [Edge209]
  BaseFeature = -> Pocket039
  Radius = 1.5
  Refine = true
  SupportTransform = false
  Suppressed = false
  UseAllEdges = false
FEATURE [PartDesign::Body] Body005  label="bracket-sg90"
  AllowCompound = false
  Group = -> [Sketch056,Pad025,Sketch057,Pad026,Sketch058,Pocket027,Sketch059,Pocket028,Sketch060,Pocket029,Sketch061,Pocket030,Sketch062,Pocket031,Sketch063,Pocket032,Sketch064,Pocket033,Fillet012,Sketch065,Pocket034,Sketch066,Pocket035,Sketch067,Pocket036,Sketch068,Pocket037,Sketch069,Pocket038,Fillet013,Sketch070,Pocket039,Fillet014]
  Origin = -> Origin006
  Tip = -> Fillet014
FEATURE [PartDesign::Fillet] Fillet015
  Base = -> Pocket012 [Edge58,Edge76]
  BaseFeature = -> Pocket012
  Placement = pos=(0,0,0) rot=(1,0,0;1.5708rad)
  Radius = 1.5
  Refine = true
  SupportTransform = false
  Suppressed = false
  UseAllEdges = false
FEATURE [Sketcher::SketchObject] Sketch071
  ArcFitTolerance = 1e-06
  AttachmentSupport = -> [Fillet015]
  ExternalGeometry = -> [Fillet015]
  FullyConstrained = false
  MakeInternals = false
  MapMode = 5
  Placement = pos=(0,14.25,-3.1e-15) rot=(1,0,0;1.5708rad)
  sketch-geometry (2):
    g0: Circle CenterX=-42 CenterY=-10.5 CenterZ=0 NormalX=0 NormalY=0 NormalZ=1 AngleXU=0 Radius=5.5
    g1: Circle CenterX=-42 CenterY=-10.5 CenterZ=0 NormalX=0 NormalY=0 NormalZ=1 AngleXU=0 Radius=1.6
  constraints (3):
    c: Coincident(g0,g-3)
    c: PointOnObject(g-3,g0)
    c: Coincident(g1,g0)
FEATURE [PartDesign::Pad] Pad027
  BaseFeature = -> Fillet015
  Direction = (0,-1,2e-16)
  Length = 13.5
  Length2 = 10
  Placement = pos=(0,0,0) rot=(1,0,0;1.5708rad)
  Profile = -> Sketch071
  ReferenceAxis = -> Sketch071 [N_Axis]
  Refine = true
  Reversed = true
  Suppressed = false
  Type = 0
FEATURE [Sketcher::SketchObject] Sketch072
  ArcFitTolerance = 1e-06
  AttachmentSupport = -> [Pad027]
  ExternalGeometry = -> [Pad027]
  FullyConstrained = true
  MakeInternals = false
  MapMode = 5
  Placement = pos=(0,4.5,-1e-15) rot=(1,0,0;1.5708rad)
  sketch-geometry (1):
    g0: Circle CenterX=0 CenterY=-0.5 CenterZ=0 NormalX=0 NormalY=0 NormalZ=1 AngleXU=0 Radius=4.1
  constraints (2):
    c: Coincident(g0,g-3)
    c: Radius(g0) = 4.1
FEATURE [PartDesign::Pocket] Pocket040
  BaseFeature = -> Pad027
  Direction = (0,1,-2e-16)
  Length = 10
  Length2 = 5
  Placement = pos=(0,0,0) rot=(1,0,0;1.5708rad)
  Profile = -> Sketch072
  ReferenceAxis = -> Sketch072 [N_Axis]
  Refine = true
  Suppressed = false
  Type = 0
FEATURE [Sketcher::SketchObject] Sketch073
  ArcFitTolerance = 1e-06
  AttachmentSupport = -> [Pocket040]
  ExternalGeometry = -> [Pocket040]
  FullyConstrained = true
  MakeInternals = false
  MapMode = 5
  Placement = pos=(0,4.5,-1e-15) rot=(1,0,0;1.5708rad)
  sketch-geometry (1):
    g0: Circle CenterX=0 CenterY=-0.5 CenterZ=0 NormalX=0 NormalY=0 NormalZ=1 AngleXU=0 Radius=5
  constraints (2):
    c: Coincident(g0,g-3)
    c: Radius(g0) = 5
FEATURE [PartDesign::Pocket] Pocket041
  BaseFeature = -> Pocket040
  Direction = (0,1,-2e-16)
  Length = 2
  Length2 = 5
  Placement = pos=(0,0,0) rot=(1,0,0;1.5708rad)
  Profile = -> Sketch073
  ReferenceAxis = -> Sketch073 [N_Axis]
  Refine = true
  Suppressed = false
  Type = 0
FEATURE [Sketcher::SketchObject] Sketch074
  ArcFitTolerance = 1e-06
  AttachmentSupport = -> [Pocket041]
  ExternalGeometry = -> [Pocket041]
  FullyConstrained = true
  MakeInternals = false
  MapMode = 5
  Placement = pos=(0,46,-1.01e-14) rot=(-1,0,0;1.5708rad)
  sketch-geometry (1):
    g0: Circle CenterX=0 CenterY=0.5 CenterZ=0 NormalX=0 NormalY=0 NormalZ=1 AngleXU=0 Radius=3.75
  constraints (2):
    c: Coincident(g0,g-3)
    c: Radius(g0) = 3.75
FEATURE [PartDesign::Pocket] Pocket042
  BaseFeature = -> Pocket041
  Direction = (0,-1,-2e-16)
  Length = 7
  Length2 = 5
  Placement = pos=(0,0,0) rot=(1,0,0;1.5708rad)
  Profile = -> Sketch074
  ReferenceAxis = -> Sketch074 [N_Axis]
  Refine = true
  Suppressed = false
  Type = 0
FEATURE [Sketcher::SketchObject] Sketch075
  ArcFitTolerance = 1e-06
  AttachmentSupport = -> [Pocket042]
  ExternalGeometry = -> [Pocket042]
  FullyConstrained = true
  MakeInternals = false
  MapMode = 5
  Placement = pos=(0,46,-1.01e-14) rot=(-1,0,0;1.5708rad)
  sketch-geometry (8):
    g0: ArcOfCircle CenterX=-14.3401 CenterY=7.7086 CenterZ=0 NormalX=0 NormalY=0 NormalZ=1 AngleXU=0 Radius=2.5 StartAngle=1.18296 EndAngle=4.16863
    g1: LineSegment [constr] StartX=0 StartY=0.5 StartZ=0 EndX=-14.3401 EndY=7.7086 EndZ=0
    g2: LineSegment [constr] StartX=-14.3401 StartY=7.7086 StartZ=0 EndX=-16.5738 EndY=8.83144 EndZ=0
    g3: ArcOfCircle CenterX=0 CenterY=0.5 CenterZ=0 NormalX=0 NormalY=0 NormalZ=1 AngleXU=0 Radius=3.75 StartAngle=4.16863 EndAngle=7.46615
    g4: LineSegment [constr] StartX=0 StartY=0.5 StartZ=0 EndX=3.35049 EndY=-1.18425 EndZ=0
    g5: LineSegment StartX=-13.3946 StartY=10.0229 StartZ=0 EndX=1.4182 EndY=3.97149 EndZ=0
    g6: LineSegment StartX=-1.94008 StartY=-2.70914 StartZ=0 EndX=-15.6335 EndY=5.56917 EndZ=0
    g7: Circle [constr] CenterX=-14.3401 CenterY=7.7086 CenterZ=0 NormalX=0 NormalY=0 NormalZ=1 AngleXU=0 Radius=4.67979
  constraints (19):
    c: Coincident(g1,g-3)
    c: Coincident(g1,g0)
    c: Coincident(g2,g0)
    c: PointOnObject(g2,g0)
    c: Coincident(g3,g1)
    c: PointOnObject(g3,g-3)
    c: Coincident(g4,g1)
    c: PointOnObject(g4,g3)
    c: Parallel(g4,g1)
    c: Parallel(g1,g2)
    c: Distance(g2,g4) = 22.3
    c: Radius(g0) = 2.5
    c: Tangent(g6,g0) = 1.5708
    c: Tangent(g5,g0) = 1.5708
    c: Tangent(g5,g3) = 1.5708
    c: Tangent(g6,g3) = 1.5708
    c: Coincident(g7,g0)
    c: Tangent(g7,g-4)
    c: Tangent(g7,g-5)
FEATURE [PartDesign::Pocket] Pocket043
  BaseFeature = -> Pocket042
  Direction = (0,-1,-2e-16)
  Length = 2
  Length2 = 5
  Placement = pos=(0,0,0) rot=(1,0,0;1.5708rad)
  Profile = -> Sketch075
  ReferenceAxis = -> Sketch075 [N_Axis]
  Refine = true
  Suppressed = false
  Type = 0
FEATURE [PartDesign::Body] Body001  label="leg-sg90"
  AllowCompound = false
  Group = -> [Sketch032,Pad017,Sketch033,Pocket012,Fillet015,Sketch071,Pad027,Sketch072,Pocket040,Sketch073,Pocket041,Sketch074,Pocket042,Sketch075,Pocket043]
  Origin = -> Origin001
  Tip = -> Pocket043
FEATURE [Sketcher::SketchObject] Sketch
  ArcFitTolerance = 1e-06
  AttachmentSupport = -> [XY_Plane007]
  FullyConstrained = true
  MakeInternals = false
  MapMode = 5
  sketch-geometry (4):
    g0: LineSegment StartX=-31 StartY=36 StartZ=0 EndX=-31 EndY=-36 EndZ=0
    g1: LineSegment StartX=-31 StartY=-36 StartZ=0 EndX=31 EndY=-36 EndZ=0
    g2: LineSegment StartX=31 StartY=-36 StartZ=0 EndX=31 EndY=36 EndZ=0
    g3: LineSegment StartX=31 StartY=36 StartZ=0 EndX=-31 EndY=36 EndZ=0
  constraints (10):
    c: Coincident(g0,g1)
    c: Coincident(g1,g2)
    c: Coincident(g2,g3)
    c: Coincident(g3,g0)
    c: Vertical(g2)
    c: Horizontal(g1)
    c: Distance(g1) = 62
    c: Distance(g2) = 72
    c: Symmetric(g0,g0,g-1)
    c: Symmetric(g2,g0,g-2)
FEATURE [PartDesign::Pad] Pad
  Direction = (0,0,1)
  Length = 26
  Length2 = 10
  Profile = -> Sketch
  ReferenceAxis = -> Sketch [N_Axis]
  Refine = true
  Suppressed = false
  Type = 0
FEATURE [PartDesign::Thickness] Thickness
  Base = -> Pad [Face6]
  BaseFeature = -> Pad
  Intersection = false
  Join = 0
  Mode = 0
  Refine = true
  Reversed = true
  SupportTransform = false
  Suppressed = false
  Value = 2
FEATURE [PartDesign::Fillet] Fillet
  Base = -> Thickness [Face5,Edge2,Edge1,Edge8,Edge5]
  BaseFeature = -> Thickness
  Radius = 1.5
  Refine = true
  SupportTransform = false
  Suppressed = false
  UseAllEdges = false
FEATURE [Sketcher::SketchObject] Sketch076
  ArcFitTolerance = 1e-06
  AttachmentSupport = -> [Fillet]
  ExternalGeometry = -> [Fillet]
  FullyConstrained = true
  MakeInternals = false
  MapMode = 5
  Placement = pos=(0,0,2) rot=(0,0,1;0rad)
  sketch-geometry (8):
    g0: LineSegment StartX=-29 StartY=34 StartZ=0 EndX=-29 EndY=-34 EndZ=0
    g1: LineSegment StartX=-29 StartY=-34 StartZ=0 EndX=-15.5 EndY=-34 EndZ=0
    g2: LineSegment StartX=-15.5 StartY=-34 StartZ=0 EndX=-15.5 EndY=34 EndZ=0
    g3: LineSegment StartX=-15.5 StartY=34 StartZ=0 EndX=-29 EndY=34 EndZ=0
    g4: LineSegment StartX=15.5 StartY=34 StartZ=0 EndX=15.5 EndY=-34 EndZ=0
    g5: LineSegment StartX=15.5 StartY=-34 StartZ=0 EndX=29 EndY=-34 EndZ=0
    g6: LineSegment StartX=29 StartY=-34 StartZ=0 EndX=29 EndY=34 EndZ=0
    g7: LineSegment StartX=29 StartY=34 StartZ=0 EndX=15.5 EndY=34 EndZ=0
  constraints (22):
    c: Coincident(g0,g1)
    c: Coincident(g1,g2)
    c: Coincident(g2,g3)
    c: Coincident(g3,g0)
    c: Vertical(g0)
    c: Vertical(g2)
    c: Horizontal(g1)
    c: Horizontal(g3)
    c: Coincident(g4,g5)
    c: Coincident(g5,g6)
    c: Coincident(g6,g7)
    c: Coincident(g7,g4)
    c: Vertical(g4)
    c: Vertical(g6)
    c: Horizontal(g5)
    c: Horizontal(g7)
    c: Symmetric(g4,g1,g-2)
    c: Equal(g3,g7)
    c: Equal(g4,g2)
    c: Distance(g1,g4) = 31
    c: Coincident(g0,g-4)
    c: Equal(g0,g-4)
FEATURE [PartDesign::Pad] Pad028
  BaseFeature = -> Fillet
  Direction = (0,0,1)
  Length = 6
  Length2 = 10
  Profile = -> Sketch076
  ReferenceAxis = -> Sketch076 [N_Axis]
  Refine = true
  Suppressed = false
  Type = 0
FEATURE [Sketcher::SketchObject] Sketch077
  ArcFitTolerance = 1e-06
  AttachmentSupport = -> [Pad028]
  ExternalGeometry = -> [Pad028]
  FullyConstrained = true
  MakeInternals = false
  MapMode = 5
  Placement = pos=(0,0,8) rot=(0,0,1;0rad)
  sketch-geometry (44):
    g0: LineSegment StartX=-29 StartY=29.2 StartZ=0 EndX=-29 EndY=6.8 EndZ=0
    g1: LineSegment StartX=-29 StartY=6.8 StartZ=0 EndX=-17 EndY=6.8 EndZ=0
    g2: LineSegment StartX=-17 StartY=6.8 StartZ=0 EndX=-17 EndY=29.2 EndZ=0
    g3: LineSegment StartX=-17 StartY=29.2 StartZ=0 EndX=-29 EndY=29.2 EndZ=0
    g4: LineSegment StartX=-29 StartY=-6.8 StartZ=0 EndX=-29 EndY=-29.2 EndZ=0
    g5: LineSegment StartX=-29 StartY=-29.2 StartZ=0 EndX=-17 EndY=-29.2 EndZ=0
    g6: LineSegment StartX=-17 StartY=-29.2 StartZ=0 EndX=-17 EndY=-6.8 EndZ=0
    g7: LineSegment StartX=-17 StartY=-6.8 StartZ=0 EndX=-29 EndY=-6.8 EndZ=0
    g8: LineSegment StartX=17 StartY=6.8 StartZ=0 EndX=17 EndY=29.2 EndZ=0
    g9: LineSegment StartX=17 StartY=29.2 StartZ=0 EndX=29 EndY=29.2 EndZ=0
    g10: LineSegment StartX=29 StartY=29.2 StartZ=0 EndX=29 EndY=6.8 EndZ=0
    g11: LineSegment StartX=29 StartY=6.8 StartZ=0 EndX=17 EndY=6.8 EndZ=0
    g12: LineSegment StartX=29 StartY=-6.8 StartZ=0 EndX=29 EndY=-29.2 EndZ=0
    g13: LineSegment StartX=29 StartY=-29.2 StartZ=0 EndX=17 EndY=-29.2 EndZ=0
    g14: LineSegment StartX=17 StartY=-29.2 StartZ=0 EndX=17 EndY=-6.8 EndZ=0
    g15: LineSegment StartX=17 StartY=-6.8 StartZ=0 EndX=29 EndY=-6.8 EndZ=0
    g16: Circle CenterX=-23 CenterY=32 CenterZ=0 NormalX=0 NormalY=0 NormalZ=1 AngleXU=0 Radius=0.9
    g17: Circle CenterX=-23 CenterY=4 CenterZ=0 NormalX=0 NormalY=0 NormalZ=1 AngleXU=0 Radius=0.9
    g18: Circle CenterX=-23 CenterY=-4 CenterZ=0 NormalX=0 NormalY=0 NormalZ=1 AngleXU=0 Radius=0.9
    g19: Circle CenterX=-23 CenterY=-32 CenterZ=0 NormalX=0 NormalY=0 NormalZ=1 AngleXU=0 Radius=0.9
    g20: Circle CenterX=23 CenterY=-4 CenterZ=0 NormalX=0 NormalY=0 NormalZ=1 AngleXU=0 Radius=0.9
    g21: Circle CenterX=23 CenterY=-32 CenterZ=0 NormalX=0 NormalY=0 NormalZ=1 AngleXU=0 Radius=0.9
    g22: Circle CenterX=23 CenterY=32 CenterZ=0 NormalX=0 NormalY=0 NormalZ=1 AngleXU=0 Radius=0.9
    g23: LineSegment [constr] StartX=-29 StartY=29.2 StartZ=0 EndX=-23 EndY=32 EndZ=0
    g24: LineSegment [constr] StartX=-23 StartY=32 StartZ=0 EndX=-17 EndY=29.2 EndZ=0
    g25: LineSegment [constr] StartX=-17 StartY=6.8 StartZ=0 EndX=-23 EndY=4 EndZ=0
    g26: LineSegment [constr] StartX=-23 StartY=4 StartZ=0 EndX=-29 EndY=6.8 EndZ=0
    g27: LineSegment [constr] StartX=23 StartY=32 StartZ=0 EndX=17 EndY=29.2 EndZ=0
    g28: LineSegment [constr] StartX=23 StartY=32 StartZ=0 EndX=29 EndY=29.2 EndZ=0
    g29: LineSegment [constr] StartX=23 StartY=-32 StartZ=0 EndX=17 EndY=-29.2 EndZ=0
    g30: LineSegment [constr] StartX=23 StartY=-32 StartZ=0 EndX=29 EndY=-29.2 EndZ=0
    g31: LineSegment [constr] StartX=17 StartY=-6.8 StartZ=0 EndX=23 EndY=-4 EndZ=0
    g32: LineSegment [constr] StartX=23 StartY=-4 StartZ=0 EndX=29 EndY=-6.8 EndZ=0
    g33: LineSegment [constr] StartX=-23 StartY=-32 StartZ=0 EndX=-17 EndY=-29.2 EndZ=0
    g34: LineSegment [constr] StartX=-23 StartY=-32 StartZ=0 EndX=-29 EndY=-29.2 EndZ=0
    g35: LineSegment [constr] StartX=-29 StartY=-6.8 StartZ=0 EndX=-23 EndY=-4 EndZ=0
    g36: LineSegment [constr] StartX=-17 StartY=-6.8 StartZ=0 EndX=-23 EndY=-4 EndZ=0
    g37: Circle CenterX=23 CenterY=4 CenterZ=0 NormalX=0 NormalY=0 NormalZ=1 AngleXU=0 Radius=0.9
    g38: LineSegment [constr] StartX=17 StartY=6.8 StartZ=0 EndX=23 EndY=4 EndZ=0
    g39: LineSegment [constr] StartX=23 StartY=4 StartZ=0 EndX=29 EndY=6.8 EndZ=0
    g40: Circle [constr] CenterX=-23 CenterY=23 CenterZ=0 NormalX=0 NormalY=0 NormalZ=1 AngleXU=0 Radius=2
    g41: LineSegment [constr] StartX=-23 StartY=23 StartZ=0 EndX=-29 EndY=23 EndZ=0
    g42: LineSegment [constr] StartX=-23 StartY=23 StartZ=0 EndX=-17 EndY=23 EndZ=0
    g43: LineSegment [constr] StartX=-23 StartY=23 StartZ=0 EndX=-23 EndY=29.2 EndZ=0
  constraints (113):
    c: Coincident(g0,g1)
    c: Coincident(g1,g2)
    c: Coincident(g2,g3)
    c: Coincident(g3,g0)
    c: Vertical(g0)
    c: Vertical(g2)
    c: Horizontal(g1)
    c: Horizontal(g3)
    c: Coincident(g4,g5)
    c: Coincident(g5,g6)
    c: Coincident(g6,g7)
    c: Coincident(g7,g4)
    c: Vertical(g4)
    c: Vertical(g6)
    c: Horizontal(g5)
    c: Horizontal(g7)
    c: Coincident(g8,g9)
    c: Coincident(g9,g10)
    c: Coincident(g10,g11)
    c: Coincident(g11,g8)
    c: Vertical(g8)
    c: Vertical(g10)
    c: Horizontal(g9)
    c: Horizontal(g11)
    c: Coincident(g12,g13)
    c: Coincident(g13,g14)
    c: Coincident(g14,g15)
    c: Coincident(g15,g12)
    c: Vertical(g12)
    c: Vertical(g14)
    c: Horizontal(g13)
    c: Horizontal(g15)
    c: Equal(g2,g6)
    c: Equal(g6,g10)
    c: Equal(g10,g12)
    c: Symmetric(g1,g6,g-1)
    c: Equal(g7,g15)
    c: Equal(g15,g11)
    c: Equal(g11,g1)
    c: PointOnObject(g0,g-3)
    c: Coincident(g23,g0)
    c: Coincident(g23,g16)
    c: Coincident(g24,g16)
    c: Coincident(g24,g2)
    c: Coincident(g25,g1)
    c: Coincident(g25,g17)
    c: Coincident(g26,g17)
    c: Coincident(g26,g0)
    c: Coincident(g27,g22)
    c: Coincident(g27,g8)
    c: Coincident(g28,g22)
    c: Coincident(g28,g9)
    c: Coincident(g29,g21)
    c: Coincident(g29,g13)
    c: Coincident(g30,g21)
    c: Coincident(g30,g12)
    c: Coincident(g31,g14)
    c: Coincident(g31,g20)
    c: Coincident(g32,g20)
    c: Coincident(g32,g12)
    c: Coincident(g33,g19)
    c: Coincident(g33,g5)
    c: Coincident(g34,g19)
    c: Coincident(g34,g4)
    c: Coincident(g35,g4)
    c: Coincident(g35,g18)
    c: Coincident(g36,g6)
    c: Coincident(g36,g18)
    c: Coincident(g38,g8)
    c: Coincident(g38,g37)
    c: Coincident(g39,g37)
    c: Coincident(g39,g10)
    c: Equal(g24,g23)
    c: Equal(g23,g26)
    c: Equal(g26,g25)
    c: Equal(g25,g38)
    c: Equal(g38,g39)
    c: Equal(g39,g28)
    c: Equal(g28,g27)
    c: Equal(g27,g34)
    c: Equal(g34,g33)
    c: Equal(g33,g35)
    c: Equal(g35,g36)
    c: Equal(g36,g30)
    c: Equal(g30,g29)
    c: Equal(g29,g31)
    c: Equal(g31,g32)
    c: Distance(g16,g17) = 28
    c: Symmetric(g8,g1,g-2)
    c: Symmetric(g6,g14,g-2)
    c: Distance(g1) = 12
    c: Equal(g22,g16)
    c: Equal(g22,g17)
    c: Equal(g22,g37)
    c: Equal(g22,g20)
    c: Equal(g22,g18)
    c: Equal(g22,g19)
    c: Equal(g22,g21)
    c: Radius(g22) = 0.9
    c: Coincident(g41,g40)
    c: PointOnObject(g41,g0)
    c: Horizontal(g41)
    c: Coincident(g42,g40)
    c: PointOnObject(g42,g2)
    c: Horizontal(g42)
    c: Equal(g42,g41)
    c: Distance(g0) = 22.4
    c: Coincident(g43,g40)
    c: PointOnObject(g43,g3)
    c: Vertical(g43)
    c: Distance(g43) = 6.2
    c: DistanceY(g-1,g40) = 23
    c: Radius(g40) = 2
FEATURE [PartDesign::Pocket] Pocket
  BaseFeature = -> Pad028
  Direction = (0,0,-1)
  Length = 10
  Length2 = 5
  Profile = -> Sketch077
  ReferenceAxis = -> Sketch077 [N_Axis]
  Refine = true
  Suppressed = false
  Type = 0
FEATURE [PartDesign::Fillet] Fillet017
  Base = -> Pocket [Edge45,Edge32,Edge38,Edge39]
  BaseFeature = -> Pocket
  Radius = 0.5
  Refine = true
  SupportTransform = false
  Suppressed = false
  UseAllEdges = false
FEATURE [Sketcher::SketchObject] Sketch078
  ArcFitTolerance = 1e-06
  AttachmentSupport = -> [Fillet017]
  FullyConstrained = true
  MakeInternals = false
  MapMode = 5
  Placement = pos=(31,0,0) rot=(0.57735,0.57735,0.57735;2.0944rad)
  sketch-geometry (1):
    g0: Circle CenterX=0 CenterY=23 CenterZ=0 NormalX=0 NormalY=0 NormalZ=1 AngleXU=0 Radius=1.6
  constraints (3):
    c: PointOnObject(g0,g-2)
    c: DistanceY(g-1,g0) = 23
    c: Radius(g0) = 1.6
FEATURE [PartDesign::Pocket] Pocket044
  BaseFeature = -> Fillet017
  Direction = (-1,0,0)
  Length = 80
  Length2 = 5
  Profile = -> Sketch078
  ReferenceAxis = -> Sketch078 [N_Axis]
  Refine = true
  Suppressed = false
  Type = 0
FEATURE [Sketcher::SketchObject] Sketch079
  ArcFitTolerance = 1e-06
  AttachmentSupport = -> [Pocket044]
  ExternalGeometry = -> [Pocket044]
  FullyConstrained = true
  MakeInternals = false
  MapMode = 5
  Placement = pos=(0,0,2) rot=(0,0,1;0rad)
  sketch-geometry (21):
    g0: LineSegment StartX=-15.5 StartY=34 StartZ=0 EndX=-15.5 EndY=28 EndZ=0
    g1: LineSegment StartX=-15.5 StartY=28 StartZ=0 EndX=-9.5 EndY=28 EndZ=0
    g2: LineSegment StartX=-9.5 StartY=28 StartZ=0 EndX=-9.5 EndY=34 EndZ=0
    g3: LineSegment StartX=-9.5 StartY=34 StartZ=0 EndX=-15.5 EndY=34 EndZ=0
    g4: LineSegment StartX=15.5 StartY=34 StartZ=0 EndX=9.5 EndY=34 EndZ=0
    g5: LineSegment StartX=9.5 StartY=34 StartZ=0 EndX=9.5 EndY=28 EndZ=0
    g6: LineSegment StartX=9.5 StartY=28 StartZ=0 EndX=15.5 EndY=28 EndZ=0
    g7: LineSegment StartX=15.5 StartY=28 StartZ=0 EndX=15.5 EndY=34 EndZ=0
    g8: LineSegment StartX=15.5 StartY=-34 StartZ=0 EndX=15.5 EndY=-28 EndZ=0
    g9: LineSegment StartX=15.5 StartY=-28 StartZ=0 EndX=9.5 EndY=-28 EndZ=0
    g10: LineSegment StartX=9.5 StartY=-28 StartZ=0 EndX=9.5 EndY=-34 EndZ=0
    g11: LineSegment StartX=9.5 StartY=-34 StartZ=0 EndX=15.5 EndY=-34 EndZ=0
    g12: LineSegment StartX=-15.5 StartY=-34 StartZ=0 EndX=-9.5 EndY=-34 EndZ=0
    g13: LineSegment StartX=-9.5 StartY=-34 StartZ=0 EndX=-9.5 EndY=-28 EndZ=0
    g14: LineSegment StartX=-9.5 StartY=-28 StartZ=0 EndX=-15.5 EndY=-28 EndZ=0
    g15: LineSegment StartX=-15.5 StartY=-28 StartZ=0 EndX=-15.5 EndY=-34 EndZ=0
    g16: Circle CenterX=-12.5 CenterY=31 CenterZ=0 NormalX=0 NormalY=0 NormalZ=1 AngleXU=0 Radius=1.4
    g17: Circle CenterX=12.5 CenterY=31 CenterZ=0 NormalX=0 NormalY=0 NormalZ=1 AngleXU=0 Radius=1.4
    g18: Circle CenterX=-12.5 CenterY=-31 CenterZ=0 NormalX=0 NormalY=0 NormalZ=1 AngleXU=0 Radius=1.4
    g19: Circle CenterX=12.5 CenterY=-31 CenterZ=0 NormalX=0 NormalY=0 NormalZ=1 AngleXU=0 Radius=1.4
    g20: Circle [constr] CenterX=-12.5 CenterY=31 CenterZ=0 NormalX=0 NormalY=0 NormalZ=1 AngleXU=0 Radius=3
  constraints (55):
    c: Coincident(g0,g1)
    c: Coincident(g1,g2)
    c: Coincident(g2,g3)
    c: Coincident(g3,g0)
    c: Vertical(g0)
    c: Vertical(g2)
    c: Horizontal(g1)
    c: Horizontal(g3)
    c: Coincident(g0,g-3)
    c: Coincident(g4,g5)
    c: Coincident(g5,g6)
    c: Coincident(g6,g7)
    c: Coincident(g7,g4)
    c: Horizontal(g4)
    c: Horizontal(g6)
    c: Vertical(g5)
    c: Vertical(g7)
    c: Coincident(g4,g-4)
    c: Coincident(g8,g9)
    c: Coincident(g9,g10)
    c: Coincident(g10,g11)
    c: Coincident(g11,g8)
    c: Vertical(g8)
    c: Vertical(g10)
    c: Horizontal(g9)
    c: Horizontal(g11)
    c: Coincident(g8,g-4)
    c: Coincident(g12,g13)
    c: Coincident(g13,g14)
    c: Coincident(g14,g15)
    c: Coincident(g15,g12)
    c: Horizontal(g12)
    c: Horizontal(g14)
    c: Vertical(g13)
    c: Vertical(g15)
    c: Coincident(g12,g-3)
    c: Equal(g18,g16)
    c: Equal(g18,g17)
    c: Equal(g18,g19)
    c: Radius(g18) = 1.4
    c: Equal(g2,g5)
    c: Equal(g5,g10)
    c: Equal(g10,g13)
    c: Symmetric(g18,g19,g-2)
    c: Symmetric(g19,g17,g-1)
    c: Symmetric(g18,g16,g-1)
    c: Coincident(g20,g16)
    c: Radius(g20) = 3
    c: Distance(g16,g17) = 25
    c: Distance(g18,g16) = 62
    c: Equal(g2,g1)
    c: Distance(g1) = 6
    c: Equal(g6,g9)
    c: Equal(g9,g14)
    c: Equal(g14,g1)
FEATURE [PartDesign::Pad] Pad029
  BaseFeature = -> Pocket044
  Direction = (0,0,1)
  Length = 11.5
  Length2 = 10
  Profile = -> Sketch079
  ReferenceAxis = -> Sketch079 [N_Axis]
  Refine = true
  Suppressed = false
  Type = 0
FEATURE [PartDesign::Fillet] Fillet018
  Base = -> Pad029 [Edge156,Edge145,Edge167,Edge168]
  BaseFeature = -> Pad029
  Radius = 1.5
  Refine = true
  SupportTransform = false
  Suppressed = false
  UseAllEdges = false
FEATURE [Sketcher::SketchObject] Sketch081
  ArcFitTolerance = 1e-06
  AttachmentSupport = -> [Fillet018]
  FullyConstrained = true
  MakeInternals = false
  MapMode = 5
  Placement = pos=(0,0,8) rot=(0,0,1;0rad)
  sketch-geometry (8):
    g0: LineSegment StartX=-28 StartY=1.9 StartZ=0 EndX=-28 EndY=-1.9 EndZ=0
    g1: LineSegment StartX=-28 StartY=-1.9 StartZ=0 EndX=-18 EndY=-1.9 EndZ=0
    g2: LineSegment StartX=-18 StartY=-1.9 StartZ=0 EndX=-18 EndY=1.9 EndZ=0
    g3: LineSegment StartX=-18 StartY=1.9 StartZ=0 EndX=-28 EndY=1.9 EndZ=0
    g4: LineSegment StartX=18 StartY=1.9 StartZ=0 EndX=18 EndY=-1.9 EndZ=0
    g5: LineSegment StartX=18 StartY=-1.9 StartZ=0 EndX=28 EndY=-1.9 EndZ=0
    g6: LineSegment StartX=28 StartY=-1.9 StartZ=0 EndX=28 EndY=1.9 EndZ=0
    g7: LineSegment StartX=28 StartY=1.9 StartZ=0 EndX=18 EndY=1.9 EndZ=0
  constraints (22):
    c: Coincident(g0,g1)
    c: Coincident(g1,g2)
    c: Coincident(g2,g3)
    c: Coincident(g3,g0)
    c: Vertical(g2)
    c: Horizontal(g1)
    c: Horizontal(g3)
    c: Coincident(g4,g5)
    c: Coincident(g5,g6)
    c: Coincident(g6,g7)
    c: Coincident(g7,g4)
    c: Vertical(g4)
    c: Vertical(g6)
    c: Horizontal(g5)
    c: Horizontal(g7)
    c: Equal(g5,g1)
    c: Equal(g2,g4)
    c: Symmetric(g4,g2,g-2)
    c: Symmetric(g0,g0,g-1)
    c: Distance(g0) = 3.8
    c: Distance(g3) = 10
    c: Distance(g0,g-3) = 1
FEATURE [Sketcher::SketchObject] Sketch082
  ArcFitTolerance = 1e-06
  AttachmentOffset = pos=(0,0,-36) rot=(0,0,1;0rad)
  AttachmentSupport = -> [XZ_Plane008]
  FullyConstrained = true
  MakeInternals = false
  MapMode = 5
  Placement = pos=(0,36,-8e-15) rot=(1,0,0;1.5708rad)
  sketch-geometry (4):
    g0: LineSegment StartX=-31 StartY=22.5 StartZ=0 EndX=31 EndY=22.5 EndZ=0
    g1: LineSegment StartX=31 StartY=22.5 StartZ=0 EndX=31 EndY=28.5 EndZ=0
    g2: LineSegment StartX=31 StartY=28.5 StartZ=0 EndX=-31 EndY=28.5 EndZ=0
    g3: LineSegment StartX=-31 StartY=28.5 StartZ=0 EndX=-31 EndY=22.5 EndZ=0
  constraints (11):
    c: Coincident(g0,g1)
    c: Coincident(g1,g2)
    c: Coincident(g2,g3)
    c: Coincident(g3,g0)
    c: Horizontal(g0)
    c: Vertical(g1)
    c: Vertical(g3)
    c: Distance(g3) = 6
    c: Distance(g0) = 62
    c: Symmetric(g2,g1,g-2)
    c: DistanceY(g-1,g0) = 22.5
FEATURE [PartDesign::Pad] Pad030
  Direction = (0,-1,2e-16)
  Length = 72
  Length2 = 10
  Placement = pos=(0,0,0) rot=(1,0,0;1.5708rad)
  Profile = -> Sketch082
  ReferenceAxis = -> Sketch082 [N_Axis]
  Refine = true
  Suppressed = false
  Type = 0
FEATURE [PartDesign::Fillet] Fillet021
  Base = -> Pad030 [Face3,Edge7,Edge12,Edge6,Edge11]
  BaseFeature = -> Pad030
  Placement = pos=(0,0,0) rot=(1,0,0;1.5708rad)
  Radius = 1.5
  Refine = true
  SupportTransform = false
  Suppressed = false
  UseAllEdges = false
FEATURE [Sketcher::SketchObject] Sketch083
  ArcFitTolerance = 1e-06
  AttachmentSupport = -> [Fillet021]
  FullyConstrained = true
  MakeInternals = false
  MapMode = 5
  Placement = pos=(0,9.9e-15,22.5) rot=(1,0,0;3.14159rad)
  sketch-geometry (16):
    g0: LineSegment StartX=17 StartY=29.7 StartZ=0 EndX=17 EndY=6.3 EndZ=0
    g1: LineSegment StartX=17 StartY=6.3 StartZ=0 EndX=29 EndY=6.3 EndZ=0
    g2: LineSegment StartX=29 StartY=6.3 StartZ=0 EndX=29 EndY=29.7 EndZ=0
    g3: LineSegment StartX=29 StartY=29.7 StartZ=0 EndX=17 EndY=29.7 EndZ=0
    g4: LineSegment StartX=17 StartY=-6.3 StartZ=0 EndX=17 EndY=-29.7 EndZ=0
    g5: LineSegment StartX=17 StartY=-29.7 StartZ=0 EndX=29 EndY=-29.7 EndZ=0
    g6: LineSegment StartX=29 StartY=-29.7 StartZ=0 EndX=29 EndY=-6.3 EndZ=0
    g7: LineSegment StartX=29 StartY=-6.3 StartZ=0 EndX=17 EndY=-6.3 EndZ=0
    g8: LineSegment StartX=-29 StartY=29.7 StartZ=0 EndX=-29 EndY=6.3 EndZ=0
    g9: LineSegment StartX=-29 StartY=6.3 StartZ=0 EndX=-17 EndY=6.3 EndZ=0
    g10: LineSegment StartX=-17 StartY=6.3 StartZ=0 EndX=-17 EndY=29.7 EndZ=0
    g11: LineSegment StartX=-17 StartY=29.7 StartZ=0 EndX=-29 EndY=29.7 EndZ=0
    g12: LineSegment StartX=-17 StartY=-6.3 StartZ=0 EndX=-17 EndY=-29.7 EndZ=0
    g13: LineSegment StartX=-17 StartY=-29.7 StartZ=0 EndX=-29 EndY=-29.7 EndZ=0
    g14: LineSegment StartX=-29 StartY=-29.7 StartZ=0 EndX=-29 EndY=-6.3 EndZ=0
    g15: LineSegment StartX=-29 StartY=-6.3 StartZ=0 EndX=-17 EndY=-6.3 EndZ=0
  constraints (45):
    c: Coincident(g0,g1)
    c: Coincident(g1,g2)
    c: Coincident(g2,g3)
    c: Coincident(g3,g0)
    c: Vertical(g0)
    c: Vertical(g2)
    c: Horizontal(g1)
    c: Horizontal(g3)
    c: Coincident(g4,g5)
    c: Coincident(g5,g6)
    c: Coincident(g6,g7)
    c: Coincident(g7,g4)
    c: Vertical(g4)
    c: Vertical(g6)
    c: Horizontal(g5)
    c: Horizontal(g7)
    c: Coincident(g8,g9)
    c: Coincident(g9,g10)
    c: Coincident(g10,g11)
    c: Coincident(g11,g8)
    c: Vertical(g8)
    c: Vertical(g10)
    c: Horizontal(g9)
    c: Horizontal(g11)
    c: Coincident(g12,g13)
    c: Coincident(g13,g14)
    c: Coincident(g14,g15)
    c: Coincident(g15,g12)
    c: Vertical(g12)
    c: Vertical(g14)
    c: Horizontal(g13)
    c: Horizontal(g15)
    c: Distance(g7) = 12
    c: Distance(g4) = 23.4
    c: DistanceX(g-2,g5) = 29
    c: DistanceY(g-1,g5) = -29.7
    c: Equal(g10,g0)
    c: Equal(g0,g14)
    c: Equal(g14,g4)
    c: Symmetric(g0,g4,g-1)
    c: Symmetric(g9,g12,g-1)
    c: Equal(g7,g1)
    c: Equal(g1,g9)
    c: Equal(g9,g15)
    c: Symmetric(g12,g4,g-2)
FEATURE [PartDesign::Pocket] Pocket047
  BaseFeature = -> Fillet021
  Direction = (0,0,1)
  Length = 2
  Length2 = 5
  Placement = pos=(0,0,0) rot=(1,0,0;1.5708rad)
  Profile = -> Sketch083
  ReferenceAxis = -> Sketch083 [N_Axis]
  Refine = true
  Suppressed = false
  Type = 0
FEATURE [PartDesign::Fillet] Fillet022
  Base = -> Pocket047 [Edge66,Edge54,Edge52,Edge70,Edge68,Edge65,Edge50,Edge49,Edge41,Edge42,Edge46,Edge44,Edge62,Edge57,Edge58,Edge60]
  BaseFeature = -> Pocket047
  Placement = pos=(0,0,0) rot=(1,0,0;1.5708rad)
  Radius = 0.5
  Refine = true
  SupportTransform = false
  Suppressed = false
  UseAllEdges = false
FEATURE [Sketcher::SketchObject] Sketch084
  ArcFitTolerance = 1e-06
  AttachmentSupport = -> [Fillet022]
  FullyConstrained = true
  MakeInternals = false
  MapMode = 5
  Placement = pos=(0,9.9e-15,22.5) rot=(1,0,0;3.14159rad)
  sketch-geometry (8):
    g0: LineSegment StartX=23.8 StartY=5 StartZ=0 EndX=23.8 EndY=-5 EndZ=0
    g1: LineSegment StartX=23.8 StartY=-5 StartZ=0 EndX=28.8 EndY=-5 EndZ=0
    g2: LineSegment StartX=28.8 StartY=-5 StartZ=0 EndX=28.8 EndY=5 EndZ=0
    g3: LineSegment StartX=28.8 StartY=5 StartZ=0 EndX=23.8 EndY=5 EndZ=0
    g4: LineSegment StartX=-28.8 StartY=5 StartZ=0 EndX=-28.8 EndY=-5 EndZ=0
    g5: LineSegment StartX=-28.8 StartY=-5 StartZ=0 EndX=-23.8 EndY=-5 EndZ=0
    g6: LineSegment StartX=-23.8 StartY=-5 StartZ=0 EndX=-23.8 EndY=5 EndZ=0
    g7: LineSegment StartX=-23.8 StartY=5 StartZ=0 EndX=-28.8 EndY=5 EndZ=0
  constraints (22):
    c: Coincident(g0,g1)
    c: Coincident(g1,g2)
    c: Coincident(g2,g3)
    c: Coincident(g3,g0)
    c: Vertical(g2)
    c: Horizontal(g1)
    c: Horizontal(g3)
    c: Coincident(g4,g5)
    c: Coincident(g5,g6)
    c: Coincident(g6,g7)
    c: Coincident(g7,g4)
    c: Vertical(g4)
    c: Vertical(g6)
    c: Horizontal(g5)
    c: Horizontal(g7)
    c: Symmetric(g0,g0,g-1)
    c: DistanceX(g-2,g2) = 28.8
    c: Distance(g3) = 5
    c: Distance(g2) = 10
    c: Equal(g6,g0)
    c: Equal(g7,g3)
    c: Symmetric(g6,g0,g-2)
FEATURE [PartDesign::Pad] Pad031
  BaseFeature = -> Fillet022
  Direction = (0,0,-1)
  Length = 9
  Length2 = 10
  Placement = pos=(0,0,0) rot=(1,0,0;1.5708rad)
  Profile = -> Sketch084
  ReferenceAxis = -> Sketch084 [N_Axis]
  Refine = true
  Suppressed = false
  Type = 0
FEATURE [PartDesign::Chamfer] Chamfer
  Angle = 45
  Base = -> Pad031 [Edge40,Edge26]
  BaseFeature = -> Pad031
  ChamferType = 0
  FlipDirection = false
  Placement = pos=(0,0,0) rot=(1,0,0;1.5708rad)
  Refine = true
  Size = 1
  Size2 = 1
  SupportTransform = false
  Suppressed = false
  UseAllEdges = false
FEATURE [PartDesign::Fillet] Fillet023
  Base = -> Chamfer [Edge55,Edge62,Edge152,Edge145]
  BaseFeature = -> Chamfer
  Placement = pos=(0,0,0) rot=(1,0,0;1.5708rad)
  Radius = 3
  Refine = true
  SupportTransform = false
  Suppressed = false
  UseAllEdges = false
FEATURE [PartDesign::Chamfer] Chamfer001
  Angle = 45
  Base = -> Fillet023 [Edge19,Edge158]
  BaseFeature = -> Fillet023
  ChamferType = 0
  FlipDirection = false
  Placement = pos=(0,0,0) rot=(1,0,0;1.5708rad)
  Refine = true
  Size = 1
  Size2 = 1
  SupportTransform = false
  Suppressed = false
  UseAllEdges = false
FEATURE [Sketcher::SketchObject] Sketch085
  ArcFitTolerance = 1e-06
  AttachmentSupport = -> [Chamfer001]
  ExternalGeometry = -> [Chamfer001]
  FullyConstrained = true
  MakeInternals = false
  MapMode = 5
  Placement = pos=(-28.8,0,0) rot=(0.707107,0,-0.707107;3.14159rad)
  sketch-geometry (2):
    g0: Circle CenterX=-18.5 CenterY=0 CenterZ=0 NormalX=0 NormalY=0 NormalZ=1 AngleXU=0 Radius=1.6
    g1: Circle [constr] CenterX=-18.5 CenterY=0 CenterZ=0 NormalX=0 NormalY=0 NormalZ=1 AngleXU=0 Radius=5
  constraints (5):
    c: PointOnObject(g0,g-1)
    c: Coincident(g1,g0)
    c: Tangent(g1,g-4)
    c: Tangent(g1,g-3)
    c: Radius(g0) = 1.6
FEATURE [PartDesign::Pocket] Pocket048
  BaseFeature = -> Chamfer001
  Direction = (1,0,2e-16)
  Length = 80
  Length2 = 5
  Placement = pos=(0,0,0) rot=(1,0,0;1.5708rad)
  Profile = -> Sketch085
  ReferenceAxis = -> Sketch085 [N_Axis]
  Refine = true
  Suppressed = false
  Type = 0
FEATURE [Sketcher::SketchObject] Sketch086
  ArcFitTolerance = 1e-06
  AttachmentOffset = pos=(0,0,-2) rot=(0,0,1;0rad)
  AttachmentSupport = -> [Pocket048]
  ExternalGeometry = -> [Pocket048]
  FullyConstrained = true
  MakeInternals = false
  MapMode = 5
  Placement = pos=(25.8,0,4e-16) rot=(0.707107,0,-0.707107;3.14159rad)
  sketch-geometry (7):
    g0: LineSegment StartX=-18.5 StartY=3.17543 StartZ=0 EndX=-21.25 EndY=1.58771 EndZ=0
    g1: LineSegment StartX=-21.25 StartY=1.58771 StartZ=0 EndX=-21.25 EndY=-1.58771 EndZ=0
    g2: LineSegment StartX=-21.25 StartY=-1.58771 StartZ=0 EndX=-18.5 EndY=-3.17543 EndZ=0
    g3: LineSegment StartX=-18.5 StartY=-3.17543 StartZ=0 EndX=-15.75 EndY=-1.58771 EndZ=0
    g4: LineSegment StartX=-15.75 StartY=-1.58771 StartZ=0 EndX=-15.75 EndY=1.58771 EndZ=0
    g5: LineSegment StartX=-15.75 StartY=1.58771 StartZ=0 EndX=-18.5 EndY=3.17543 EndZ=0
    g6: Circle [constr] CenterX=-18.5 CenterY=0 CenterZ=0 NormalX=0 NormalY=0 NormalZ=1 AngleXU=0 Radius=3.17543
  constraints (16):
    c: Coincident(g0,g1)
    c: Coincident(g1,g2)
    c: Coincident(g2,g3)
    c: Coincident(g3,g4)
    c: Coincident(g4,g5)
    c: Coincident(g5,g0)
    c: Equal(g0, g1-g5) x5
    c: PointOnObject(g0,g6)
    c: PointOnObject(g1,g6)
    c: PointOnObject(g2,g6)
    c: PointOnObject(g3,g6)
    c: PointOnObject(g4,g6)
    c: PointOnObject(g5,g6)
    c: Coincident(g6,g-3)
    c: Vertical(g4)
    c: Distance(g0,g4) = 5.5
FEATURE [PartDesign::Pocket] Pocket049
  BaseFeature = -> Pocket048
  Direction = (1,0,2e-16)
  Length = 51.6
  Length2 = 5
  Placement = pos=(0,0,0) rot=(1,0,0;1.5708rad)
  Profile = -> Sketch086
  ReferenceAxis = -> Sketch086 [N_Axis]
  Refine = true
  Reversed = true
  Suppressed = false
  Type = 0
FEATURE [Sketcher::SketchObject] Sketch087
  ArcFitTolerance = 1e-06
  AttachmentSupport = -> [Pocket049]
  ExternalGeometry = -> [Pocket049]
  FullyConstrained = true
  MakeInternals = false
  MapMode = 5
  Placement = pos=(0,36,0) rot=(-1,0,0;1.5708rad)
  sketch-geometry (6):
    g0: LineSegment StartX=-5 StartY=-22.5 StartZ=0 EndX=-5 EndY=-26 EndZ=0
    g1: LineSegment StartX=5 StartY=-26 StartZ=0 EndX=5 EndY=-22.5 EndZ=0
    g2: LineSegment StartX=-5 StartY=-22.5 StartZ=0 EndX=5 EndY=-22.5 EndZ=0
    g3: ArcOfCircle CenterX=-3.5 CenterY=-26 CenterZ=0 NormalX=0 NormalY=0 NormalZ=1 AngleXU=0 Radius=1.5 StartAngle=3.14159 EndAngle=4.71239
    g4: ArcOfCircle CenterX=3.5 CenterY=-26 CenterZ=0 NormalX=0 NormalY=0 NormalZ=1 AngleXU=0 Radius=1.5 StartAngle=4.71239 EndAngle=6.28319
    g5: LineSegment StartX=-3.5 StartY=-27.5 StartZ=0 EndX=3.5 EndY=-27.5 EndZ=0
  constraints (15):
    c: Vertical(g0)
    c: Vertical(g1)
    c: PointOnObject(g0,g-3)
    c: Symmetric(g0,g1,g-2)
    c: Coincident(g2,g0)
    c: Coincident(g2,g1)
    c: Horizontal(g5)
    c: Equal(g3,g4)
    c: Tangent(g4,g1) = -1.5708
    c: Tangent(g3,g0) = -1.5708
    c: Tangent(g5,g3) = -1.5708
    c: Tangent(g5,g4) = -1.5708
    c: Distance(g2) = 10
    c: DistanceY(g3,g0) = 5
    c: Radius(g3) = 1.5
FEATURE [PartDesign::Pocket] Pocket050
  BaseFeature = -> Pocket049
  Direction = (0,-1,-2e-16)
  Length = 12
  Length2 = 5
  Placement = pos=(0,0,0) rot=(1,0,0;1.5708rad)
  Profile = -> Sketch087
  ReferenceAxis = -> Sketch087 [N_Axis]
  Refine = true
  Suppressed = false
  Type = 0
FEATURE [Sketcher::SketchObject] Sketch088
  ArcFitTolerance = 1e-06
  AttachmentSupport = -> [Pocket050]
  ExternalGeometry = -> [Pocket050]
  FullyConstrained = true
  MakeInternals = false
  MapMode = 5
  Placement = pos=(0,1.25e-14,28.5) rot=(0,0,1;3.14159rad)
  sketch-geometry (4):
    g0: LineSegment StartX=-9 StartY=16 StartZ=0 EndX=-9 EndY=-8 EndZ=0
    g1: LineSegment StartX=-9 StartY=-8 StartZ=0 EndX=9 EndY=-8 EndZ=0
    g2: LineSegment StartX=9 StartY=-8 StartZ=0 EndX=9 EndY=16 EndZ=0
    g3: LineSegment StartX=9 StartY=16 StartZ=0 EndX=-9 EndY=16 EndZ=0
  constraints (11):
    c: Coincident(g0,g1)
    c: Coincident(g1,g2)
    c: Coincident(g2,g3)
    c: Coincident(g3,g0)
    c: Vertical(g0)
    c: Vertical(g2)
    c: Horizontal(g3)
    c: Distance(g0,g-3) = 28
    c: Distance(g0) = 24
    c: Distance(g1) = 18
    c: Symmetric(g0,g1,g-2)
FEATURE [PartDesign::Pocket] Pocket051
  BaseFeature = -> Pocket050
  Direction = (0,0,-1)
  Length = 16
  Length2 = 5
  Placement = pos=(0,0,0) rot=(1,0,0;1.5708rad)
  Profile = -> Sketch088
  ReferenceAxis = -> Sketch088 [N_Axis]
  Refine = true
  Suppressed = false
  Type = 0
FEATURE [PartDesign::Fillet] Fillet024
  Base = -> Pocket051 [Edge170,Edge171,Edge175,Edge173]
  BaseFeature = -> Pocket051
  Placement = pos=(0,0,0) rot=(1,0,0;1.5708rad)
  Radius = 0.5
  Refine = true
  SupportTransform = false
  Suppressed = false
  UseAllEdges = false
FEATURE [Sketcher::SketchObject] Sketch089
  ArcFitTolerance = 1e-06
  AttachmentSupport = -> [Fillet024]
  FullyConstrained = true
  MakeInternals = false
  MapMode = 5
  Placement = pos=(0,1.25e-14,28.5) rot=(0,0,1;3.14159rad)
  sketch-geometry (8):
    g0: LineSegment [constr] StartX=-23 StartY=23 StartZ=0 EndX=-23 EndY=-23 EndZ=0
    g1: LineSegment [constr] StartX=-23 StartY=-23 StartZ=0 EndX=23 EndY=-23 EndZ=0
    g2: LineSegment [constr] StartX=23 StartY=-23 StartZ=0 EndX=23 EndY=23 EndZ=0
    g3: LineSegment [constr] StartX=23 StartY=23 StartZ=0 EndX=-23 EndY=23 EndZ=0
    g4: Circle CenterX=23 CenterY=23 CenterZ=0 NormalX=0 NormalY=0 NormalZ=1 AngleXU=0 Radius=1.6
    g5: Circle CenterX=-23 CenterY=23 CenterZ=0 NormalX=0 NormalY=0 NormalZ=1 AngleXU=0 Radius=1.6
    g6: Circle CenterX=-23 CenterY=-23 CenterZ=0 NormalX=0 NormalY=0 NormalZ=1 AngleXU=0 Radius=1.6
    g7: Circle CenterX=23 CenterY=-23 CenterZ=0 NormalX=0 NormalY=0 NormalZ=1 AngleXU=0 Radius=1.6
  constraints (18):
    c: Coincident(g0,g1)
    c: Coincident(g1,g2)
    c: Coincident(g2,g3)
    c: Coincident(g3,g0)
    c: Vertical(g2)
    c: Horizontal(g1)
    c: Symmetric(g0,g0,g-1)
    c: Symmetric(g2,g0,g-2)
    c: Coincident(g4,g2)
    c: Distance(g3) = 46
    c: Distance(g0) = 46
    c: Coincident(g5,g0)
    c: Coincident(g6,g0)
    c: Coincident(g7,g1)
    c: Equal(g5,g6)
    c: Equal(g5,g4)
    c: Equal(g5,g7)
    c: Radius(g5) = 1.6
FEATURE [PartDesign::Pocket] Pocket052
  BaseFeature = -> Fillet024
  Direction = (0,0,-1)
  Length = 10
  Length2 = 5
  Placement = pos=(0,0,0) rot=(1,0,0;1.5708rad)
  Profile = -> Sketch089
  ReferenceAxis = -> Sketch089 [N_Axis]
  Refine = true
  Suppressed = false
  Type = 0
FEATURE [Sketcher::SketchObject] Sketch090
  ArcFitTolerance = 1e-06
  AttachmentSupport = -> [Pocket052]
  ExternalGeometry = -> [Pocket052]
  FullyConstrained = true
  MakeInternals = false
  MapMode = 5
  Placement = pos=(0,0,24.5) rot=(1,0,0;3.14159rad)
  sketch-geometry (28):
    g0: LineSegment StartX=-21.4123 StartY=25.75 StartZ=0 EndX=-24.5877 EndY=25.75 EndZ=0
    g1: LineSegment StartX=-24.5877 StartY=25.75 StartZ=0 EndX=-26.1754 EndY=23 EndZ=0
    g2: LineSegment StartX=-26.1754 StartY=23 StartZ=0 EndX=-24.5877 EndY=20.25 EndZ=0
    g3: LineSegment StartX=-24.5877 StartY=20.25 StartZ=0 EndX=-21.4123 EndY=20.25 EndZ=0
    g4: LineSegment StartX=-21.4123 StartY=20.25 StartZ=0 EndX=-19.8246 EndY=23 EndZ=0
    g5: LineSegment StartX=-19.8246 StartY=23 StartZ=0 EndX=-21.4123 EndY=25.75 EndZ=0
    g6: Circle [constr] CenterX=-23 CenterY=23 CenterZ=0 NormalX=0 NormalY=0 NormalZ=1 AngleXU=0 Radius=3.17543
    g7: LineSegment StartX=21.4123 StartY=25.75 StartZ=0 EndX=19.8246 EndY=23 EndZ=0
    g8: LineSegment StartX=19.8246 StartY=23 StartZ=0 EndX=21.4123 EndY=20.25 EndZ=0
    g9: LineSegment StartX=21.4123 StartY=20.25 StartZ=0 EndX=24.5877 EndY=20.25 EndZ=0
    g10: LineSegment StartX=24.5877 StartY=20.25 StartZ=0 EndX=26.1754 EndY=23 EndZ=0
    g11: LineSegment StartX=26.1754 StartY=23 StartZ=0 EndX=24.5877 EndY=25.75 EndZ=0
    g12: LineSegment StartX=24.5877 StartY=25.75 StartZ=0 EndX=21.4123 EndY=25.75 EndZ=0
    g13: Circle [constr] CenterX=23 CenterY=23 CenterZ=0 NormalX=0 NormalY=0 NormalZ=1 AngleXU=0 Radius=3.17543
    g14: LineSegment StartX=-19.8246 StartY=-23 StartZ=0 EndX=-21.4123 EndY=-20.25 EndZ=0
    g15: LineSegment StartX=-21.4123 StartY=-20.25 StartZ=0 EndX=-24.5877 EndY=-20.25 EndZ=0
    g16: LineSegment StartX=-24.5877 StartY=-20.25 StartZ=0 EndX=-26.1754 EndY=-23 EndZ=0
    g17: LineSegment StartX=-26.1754 StartY=-23 StartZ=0 EndX=-24.5877 EndY=-25.75 EndZ=0
    g18: LineSegment StartX=-24.5877 StartY=-25.75 StartZ=0 EndX=-21.4123 EndY=-25.75 EndZ=0
    g19: LineSegment StartX=-21.4123 StartY=-25.75 StartZ=0 EndX=-19.8246 EndY=-23 EndZ=0
    g20: Circle [constr] CenterX=-23 CenterY=-23 CenterZ=0 NormalX=0 NormalY=0 NormalZ=1 AngleXU=0 Radius=3.17543
    g21: LineSegment StartX=26.1754 StartY=-23 StartZ=0 EndX=24.5877 EndY=-20.25 EndZ=0
    g22: LineSegment StartX=24.5877 StartY=-20.25 StartZ=0 EndX=21.4123 EndY=-20.25 EndZ=0
    g23: LineSegment StartX=21.4123 StartY=-20.25 StartZ=0 EndX=19.8246 EndY=-23 EndZ=0
    g24: LineSegment StartX=19.8246 StartY=-23 StartZ=0 EndX=21.4123 EndY=-25.75 EndZ=0
    g25: LineSegment StartX=21.4123 StartY=-25.75 StartZ=0 EndX=24.5877 EndY=-25.75 EndZ=0
    g26: LineSegment StartX=24.5877 StartY=-25.75 StartZ=0 EndX=26.1754 EndY=-23 EndZ=0
    g27: Circle [constr] CenterX=23 CenterY=-23 CenterZ=0 NormalX=0 NormalY=0 NormalZ=1 AngleXU=0 Radius=3.17543
  constraints (64):
    c: Coincident(g0,g1)
    c: Coincident(g1,g2)
    c: Coincident(g2,g3)
    c: Coincident(g3,g4)
    c: Coincident(g4,g5)
    c: Coincident(g5,g0)
    c: Equal(g0, g1-g5) x5
    c: PointOnObject(g0,g6)
    c: PointOnObject(g1,g6)
    c: PointOnObject(g2,g6)
    c: PointOnObject(g3,g6)
    c: PointOnObject(g4,g6)
    c: PointOnObject(g5,g6)
    c: Coincident(g6,g-3)
    c: Coincident(g7,g8)
    c: Coincident(g8,g9)
    c: Coincident(g9,g10)
    c: Coincident(g10,g11)
    c: Coincident(g11,g12)
    c: Coincident(g12,g7)
    c: Equal(g7, g8-g12) x5
    c: PointOnObject(g7,g13)
    c: PointOnObject(g8,g13)
    c: PointOnObject(g9,g13)
    c: PointOnObject(g10,g13)
    c: PointOnObject(g11,g13)
    c: PointOnObject(g12,g13)
    c: Coincident(g13,g-4)
    c: Coincident(g14,g15)
    c: Coincident(g15,g16)
    c: Coincident(g16,g17)
    c: Coincident(g17,g18)
    c: Coincident(g18,g19)
    c: Coincident(g19,g14)
    c: Equal(g14, g15-g19) x5
    c: PointOnObject(g14,g20)
    c: PointOnObject(g15,g20)
    c: PointOnObject(g16,g20)
    c: PointOnObject(g17,g20)
    c: PointOnObject(g18,g20)
    c: PointOnObject(g19,g20)
    c: Coincident(g20,g-6)
    c: Coincident(g21,g22)
    c: Coincident(g22,g23)
    c: Coincident(g23,g24)
    c: Coincident(g24,g25)
    c: Coincident(g25,g26)
    c: Coincident(g26,g21)
    c: Equal(g21, g22-g26) x5
    c: PointOnObject(g21,g27)
    c: PointOnObject(g22,g27)
    c: PointOnObject(g23,g27)
    c: PointOnObject(g24,g27)
    c: PointOnObject(g25,g27)
    c: PointOnObject(g26,g27)
    c: Coincident(g27,g-5)
    c: Horizontal(g18)
    c: Horizontal(g3)
    c: Horizontal(g9)
    c: Horizontal(g25)
    c: Equal(g18,g25)
    c: Equal(g25,g9)
    c: Equal(g9,g3)
    c: Distance(g7,g8) = 5.5
FEATURE [PartDesign::Pocket] Pocket053
  BaseFeature = -> Pocket052
  Direction = (0,0,1)
  Length = 2
  Length2 = 5
  Placement = pos=(0,0,0) rot=(1,0,0;1.5708rad)
  Profile = -> Sketch090
  ReferenceAxis = -> Sketch090 [N_Axis]
  Refine = true
  Suppressed = false
  Type = 0
FEATURE [Sketcher::SketchObject] Sketch091
  ArcFitTolerance = 1e-06
  AttachmentSupport = -> [Pocket053]
  FullyConstrained = true
  MakeInternals = false
  MapMode = 5
  Placement = pos=(0,9.9e-15,22.5) rot=(1,0,0;3.14159rad)
  sketch-geometry (4):
    g0: LineSegment StartX=-15 StartY=34 StartZ=0 EndX=15 EndY=34 EndZ=0
    g1: LineSegment StartX=15 StartY=34 StartZ=0 EndX=15 EndY=-34 EndZ=0
    g2: LineSegment StartX=15 StartY=-34 StartZ=0 EndX=-15 EndY=-34 EndZ=0
    g3: LineSegment StartX=-15 StartY=-34 StartZ=0 EndX=-15 EndY=34 EndZ=0
  constraints (10):
    c: Coincident(g0,g1)
    c: Vertical(g1)
    c: Coincident(g1,g2)
    c: Horizontal(g2)
    c: Coincident(g2,g3)
    c: Coincident(g3,g0)
    c: Symmetric(g2,g0,g-1)
    c: Symmetric(g0,g0,g-2)
    c: Distance(g0) = 30
    c: Distance(g1) = 68
FEATURE [PartDesign::Pocket] Pocket054
  BaseFeature = -> Pocket053
  Direction = (0,0,1)
  Length = 4.5
  Length2 = 5
  Placement = pos=(0,0,0) rot=(1,0,0;1.5708rad)
  Profile = -> Sketch091
  ReferenceAxis = -> Sketch091 [N_Axis]
  Refine = true
  Suppressed = false
  Type = 0
FEATURE [PartDesign::Chamfer] Chamfer002
  Angle = 45
  Base = -> Pocket054 [Edge24,Edge52,Edge40,Edge57]
  BaseFeature = -> Pocket054
  ChamferType = 0
  FlipDirection = false
  Placement = pos=(0,0,0) rot=(1,0,0;1.5708rad)
  Refine = true
  Size = 1
  Size2 = 1
  SupportTransform = false
  Suppressed = false
  UseAllEdges = false
FEATURE [PartDesign::Body] Body006  label="body-cover"
  AllowCompound = false
  Group = -> [Sketch082,Pad030,Fillet021,Sketch083,Pocket047,Fillet022,Sketch084,Pad031,Chamfer,Fillet023,Chamfer001,Sketch085,Pocket048,Sketch086,Pocket049,Sketch087,Pocket050,Sketch088,Pocket051,Fillet024,Sketch089,Pocket052,Sketch090,Pocket053,Sketch091,Pocket054,Chamfer002]
  Origin = -> Origin008
  Placement = pos=(0,0,1) rot=(0,0,1;0rad)
  Tip = -> Chamfer002
FEATURE [Part::Feature] Pad016  label="eye-base"
  Placement = pos=(-11,-36.1,14) rot=(1,0,0;1.5708rad)
  shape: bbox 15 x 0.3 x 15 mm, 3 faces (baked)
FEATURE [Part::Feature] Pad032  label="black-eye"
  Placement = pos=(-11,-36.1,14) rot=(1,0,0;1.5708rad)
  shape: bbox 9.7 x 0.4 x 9.7 mm, 3 faces (baked)
FEATURE [Part::Feature] Fillet004  label="eye-cover"
  Placement = pos=(-11,-36.1,14) rot=(1,0,0;1.5708rad)
  shape: bbox 18.49 x 3.9 x 19.71 mm, 4 faces (baked)
FEATURE [Part::Feature] Pad018  label="eye-base001"
  Placement = pos=(11,-36.1,14) rot=(1,0,0;1.5708rad)
  shape: bbox 15 x 0.3 x 15 mm, 3 faces (baked)
FEATURE [Part::Feature] Fillet005  label="eye-cover001"
  Placement = pos=(11,-36.1,14) rot=(1,0,0;1.5708rad)
  shape: bbox 18.49 x 3.9 x 19.71 mm, 4 faces (baked)
FEATURE [Part::Feature] Pad033  label="black-eye001"
  Placement = pos=(11,-36.1,14) rot=(1,0,0;1.5708rad)
  shape: bbox 9.7 x 0.4 x 9.7 mm, 3 faces (baked)
FEATURE [Part::Feature] Part__Feature116  label="JST XHP-3 Housing"
  Placement = pos=(1.25,1.5,-26) rot=(0,1,0;3.14159rad)
  shape: bbox 9.7 x 5.5 x 7.85 mm, 85 faces (baked)
FEATURE [PartDesign::Pocket] Pocket055
  BaseFeature = -> Fillet018
  Direction = (0,0,-1)
  Length = 12
  Length2 = 5
  Profile = -> Sketch081
  ReferenceAxis = -> Sketch081 [N_Axis]
  Refine = true
  Suppressed = false
  Type = 0
FEATURE [PartDesign::Fillet] Fillet025
  Base = -> Pocket055 [Edge195,Edge193,Edge198,Edge196,Edge161,Edge159,Edge156,Edge158]
  BaseFeature = -> Pocket055
  Radius = 0.2
  Refine = true
  SupportTransform = false
  Suppressed = false
  UseAllEdges = false
FEATURE [Sketcher::SketchObject] Sketch093
  ArcFitTolerance = 1e-06
  AttachmentSupport = -> [Fillet025]
  FullyConstrained = true
  MakeInternals = false
  MapMode = 5
  Placement = pos=(0,0,2) rot=(0,0,1;0rad)
  sketch-geometry (18):
    g0: LineSegment StartX=-4.2 StartY=28 StartZ=0 EndX=-9.5 EndY=29.5 EndZ=0
    g1: LineSegment StartX=-11 StartY=28 StartZ=0 EndX=-6.6 EndY=24.8 EndZ=0
    g2: LineSegment StartX=-6.6 StartY=24.8 StartZ=0 EndX=-3.8 EndY=24.8 EndZ=0
    g3: LineSegment StartX=-3.8 StartY=24.8 StartZ=0 EndX=-3.8 EndY=25.8 EndZ=0
    g4: LineSegment StartX=-3.8 StartY=25.8 StartZ=0 EndX=-5 EndY=25.8 EndZ=0
    g5: LineSegment StartX=-5 StartY=25.8 StartZ=0 EndX=-5 EndY=27 EndZ=0
    g6: LineSegment StartX=-5 StartY=27 StartZ=0 EndX=-4.2 EndY=27 EndZ=0
    g7: LineSegment StartX=-4.2 StartY=27 StartZ=0 EndX=-4.2 EndY=28 EndZ=0
    g8: LineSegment StartX=3.8 StartY=24.8 StartZ=0 EndX=3.8 EndY=25.8 EndZ=0
    g9: LineSegment StartX=3.8 StartY=25.8 StartZ=0 EndX=5 EndY=25.8 EndZ=0
    g10: LineSegment StartX=5 StartY=25.8 StartZ=0 EndX=5 EndY=27 EndZ=0
    g11: LineSegment StartX=5 StartY=27 StartZ=0 EndX=4.2 EndY=27 EndZ=0
    g12: LineSegment StartX=4.2 StartY=27 StartZ=0 EndX=4.2 EndY=28 EndZ=0
    g13: LineSegment StartX=4.2 StartY=28 StartZ=0 EndX=9.5 EndY=29.5 EndZ=0
    g14: LineSegment StartX=9.5 StartY=29.5 StartZ=0 EndX=11 EndY=28 EndZ=0
    g15: LineSegment StartX=3.8 StartY=24.8 StartZ=0 EndX=6.6 EndY=24.8 EndZ=0
    g16: LineSegment StartX=-9.5 StartY=29.5 StartZ=0 EndX=-11 EndY=28 EndZ=0
    g17: LineSegment StartX=11 StartY=28 StartZ=0 EndX=6.6 EndY=24.8 EndZ=0
  constraints (48):
    c: Coincident(g1,g2)
    c: Horizontal(g2)
    c: Coincident(g2,g3)
    c: Vertical(g3)
    c: Coincident(g3,g4)
    c: Horizontal(g4)
    c: Coincident(g4,g5)
    c: Vertical(g5)
    c: Coincident(g5,g6)
    c: Horizontal(g6)
    c: Coincident(g6,g7)
    c: Coincident(g7,g0)
    c: Vertical(g7)
    c: Vertical(g8)
    c: Coincident(g8,g9)
    c: Horizontal(g9)
    c: Coincident(g9,g10)
    c: Coincident(g10,g11)
    c: Horizontal(g11)
    c: Coincident(g11,g12)
    c: Vertical(g12)
    c: Coincident(g12,g13)
    c: Coincident(g13,g14)
    c: Coincident(g8,g15)
    c: Horizontal(g15)
    c: Coincident(g0,g16)
    c: Symmetric(g0,g12,g-2)
    c: Distance(g7,g7) = 1
    c: Symmetric(g8,g2,g-2)
    c: Vertical(g10)
    c: Distance(g5,g-3) = 4.5
    c: Equal(g10,g5)
    c: DistanceY(g5,g5) = 1.2
    c: Distance(g5,g-1) = 27
    c: DistanceX(g4,g4) = 1.2
    c: Equal(g8,g3)
    c: DistanceX(g0,g0) = 5.3
    c: Equal(g11,g6)
    c: Distance(g8,g8) = 1
    c: Equal(g2,g15)
    c: Coincident(g16,g-5)
    c: Coincident(g16,g1)
    c: Coincident(g17,g15)
    c: Coincident(g14,g17)
    c: Coincident(g-6,g14)
    c: Coincident(g13,g-4)
    c: Coincident(g0,g-3)
    c: DistanceX(g2,g2) = 2.8
FEATURE [PartDesign::Pad] Pad034
  BaseFeature = -> Fillet025
  Direction = (0,0,1)
  Length = 8
  Length2 = 10
  Profile = -> Sketch093
  ReferenceAxis = -> Sketch093 [N_Axis]
  Refine = true
  Suppressed = false
  Type = 0
FEATURE [Sketcher::SketchObject] Sketch095
  ArcFitTolerance = 1e-06
  AttachmentSupport = -> [Pad034]
  FullyConstrained = true
  MakeInternals = false
  MapMode = 5
  Placement = pos=(0,0,2) rot=(0,0,1;0rad)
  sketch-geometry (4):
    g0: LineSegment StartX=-5.75 StartY=28 StartZ=0 EndX=-5.75 EndY=24.8 EndZ=0
    g1: LineSegment StartX=-5.75 StartY=24.8 StartZ=0 EndX=5.75 EndY=24.8 EndZ=0
    g2: LineSegment StartX=5.75 StartY=24.8 StartZ=0 EndX=5.75 EndY=28 EndZ=0
    g3: LineSegment StartX=5.75 StartY=28 StartZ=0 EndX=-5.75 EndY=28 EndZ=0
  constraints (11):
    c: Coincident(g0,g1)
    c: Coincident(g1,g2)
    c: Coincident(g2,g3)
    c: Coincident(g3,g0)
    c: Vertical(g0)
    c: Vertical(g2)
    c: Horizontal(g1)
    c: Symmetric(g2,g0,g-2)
    c: DistanceX(g1,g1) = 11.5
    c: PointOnObject(g-3,g1)
    c: PointOnObject(g-4,g3)
FEATURE [PartDesign::Pad] Pad035
  BaseFeature = -> Pad034
  Direction = (0,0,1)
  Length = 1.5
  Length2 = 10
  Profile = -> Sketch095
  ReferenceAxis = -> Sketch095 [N_Axis]
  Refine = true
  Suppressed = false
  Type = 0
FEATURE [Sketcher::SketchObject] Sketch096
  ArcFitTolerance = 1e-06
  AttachmentSupport = -> [Pad035]
  FullyConstrained = true
  MakeInternals = false
  MapMode = 5
  Placement = pos=(0,0,3.5) rot=(0,0,1;0rad)
  sketch-geometry (4):
    g0: LineSegment StartX=-5 StartY=27 StartZ=0 EndX=-5 EndY=25.8 EndZ=0
    g1: LineSegment StartX=-5 StartY=25.8 StartZ=0 EndX=5 EndY=25.8 EndZ=0
    g2: LineSegment StartX=5 StartY=25.8 StartZ=0 EndX=5 EndY=27 EndZ=0
    g3: LineSegment StartX=5 StartY=27 StartZ=0 EndX=-5 EndY=27 EndZ=0
  constraints (10):
    c: Coincident(g0,g1)
    c: Coincident(g1,g2)
    c: Coincident(g2,g3)
    c: Coincident(g3,g0)
    c: Vertical(g0)
    c: Vertical(g2)
    c: Horizontal(g1)
    c: Horizontal(g3)
    c: Coincident(g-3,g0)
    c: Coincident(g1,g-4)
FEATURE [PartDesign::Pocket] Pocket056
  BaseFeature = -> Pad035
  Direction = (0,0,-1)
  Length = 1.5
  Length2 = 5
  Profile = -> Sketch096
  ReferenceAxis = -> Sketch096 [N_Axis]
  Refine = true
  Suppressed = false
  Type = 0
FEATURE [Sketcher::SketchObject] Sketch094
  ArcFitTolerance = 1e-06
  AttachmentSupport = -> [Pocket056]
  ExternalGeometry = -> [Fillet018]
  FullyConstrained = true
  MakeInternals = false
  MapMode = 5
  Placement = pos=(0,34,0) rot=(1,0,0;1.5708rad)
  sketch-geometry (4):
    g0: LineSegment StartX=-5.5 StartY=9.5 StartZ=0 EndX=-5.5 EndY=2 EndZ=0
    g1: LineSegment StartX=-5.5 StartY=2 StartZ=0 EndX=5.5 EndY=2 EndZ=0
    g2: LineSegment StartX=5.5 StartY=2 StartZ=0 EndX=5.5 EndY=9.5 EndZ=0
    g3: LineSegment StartX=5.5 StartY=9.5 StartZ=0 EndX=-5.5 EndY=9.5 EndZ=0
  constraints (11):
    c: Coincident(g0,g1)
    c: Coincident(g1,g2)
    c: Coincident(g2,g3)
    c: Coincident(g3,g0)
    c: Vertical(g0)
    c: Vertical(g2)
    c: Horizontal(g3)
    c: Symmetric(g0,g1,g-2)
    c: DistanceX(g3,g3) = 11
    c: PointOnObject(g0,g-3)
    c: DistanceY(g0,g0) = 7.5
FEATURE [PartDesign::Pocket] Pocket057
  BaseFeature = -> Pocket056
  Direction = (0,1,-2e-16)
  Length = 5
  Length2 = 5
  Profile = -> Sketch094
  ReferenceAxis = -> Sketch094 [N_Axis]
  Refine = true
  Suppressed = false
  Type = 0
FEATURE [PartDesign::Fillet] Fillet026
  Base = -> Pocket057 [Edge210,Edge207,Edge205,Edge208]
  BaseFeature = -> Pocket057
  Radius = 0.5
  Refine = true
  SupportTransform = false
  Suppressed = false
  UseAllEdges = false
FEATURE [Sketcher::SketchObject] Sketch097
  ArcFitTolerance = 1e-06
  AttachmentSupport = -> [Fillet026]
  ExternalGeometry = -> [Fillet026]
  FullyConstrained = true
  MakeInternals = false
  MapMode = 5
  Placement = pos=(0,0,2) rot=(0,0,1;0rad)
  sketch-geometry (4):
    g0: LineSegment StartX=-11 StartY=-28 StartZ=0 EndX=-11 EndY=-34 EndZ=0
    g1: LineSegment StartX=-11 StartY=-34 StartZ=0 EndX=11 EndY=-34 EndZ=0
    g2: LineSegment StartX=11 StartY=-34 StartZ=0 EndX=11 EndY=-28 EndZ=0
    g3: LineSegment StartX=11 StartY=-28 StartZ=0 EndX=-11 EndY=-28 EndZ=0
  constraints (10):
    c: Coincident(g0,g1)
    c: Coincident(g1,g2)
    c: Coincident(g2,g3)
    c: Coincident(g3,g0)
    c: Vertical(g0)
    c: Vertical(g2)
    c: Horizontal(g1)
    c: Coincident(g2,g-4)
    c: Coincident(g0,g-3)
    c: PointOnObject(g0,g-5)
FEATURE [PartDesign::Pad] Pad036
  BaseFeature = -> Fillet026
  Direction = (0,0,1)
  Length = 11.5
  Length2 = 10
  Profile = -> Sketch097
  ReferenceAxis = -> Sketch097 [N_Axis]
  Refine = true
  Suppressed = false
  Type = 0
FEATURE [Sketcher::SketchObject] Sketch098
  ArcFitTolerance = 1e-06
  AttachmentSupport = -> [Pad036]
  ExternalGeometry = -> [Pad036]
  FullyConstrained = true
  MakeInternals = false
  MapMode = 5
  Placement = pos=(0,0,13.5) rot=(0,0,1;0rad)
  sketch-geometry (4):
    g0: LineSegment StartX=-6.6 StartY=-34 StartZ=0 EndX=6.6 EndY=-34 EndZ=0
    g1: LineSegment StartX=6.6 StartY=-34 StartZ=0 EndX=6.6 EndY=-27 EndZ=0
    g2: LineSegment StartX=6.6 StartY=-27 StartZ=0 EndX=-6.6 EndY=-27 EndZ=0
    g3: LineSegment StartX=-6.6 StartY=-27 StartZ=0 EndX=-6.6 EndY=-34 EndZ=0
  constraints (11):
    c: Coincident(g0,g1)
    c: Coincident(g1,g2)
    c: Coincident(g2,g3)
    c: Coincident(g3,g0)
    c: Horizontal(g0)
    c: Vertical(g1)
    c: Vertical(g3)
    c: DistanceX(g2,g2) = 13.2
    c: DistanceY(g1,g1) = 7
    c: PointOnObject(g0,g-3)
    c: Symmetric(g2,g1,g-2)
FEATURE [PartDesign::Pocket] Pocket058
  BaseFeature = -> Pad036
  Direction = (0,0,-1)
  Length = 8.5
  Length2 = 5
  Profile = -> Sketch098
  ReferenceAxis = -> Sketch098 [N_Axis]
  Refine = true
  Suppressed = false
  Type = 0
FEATURE [Sketcher::SketchObject] Sketch099
  ArcFitTolerance = 1e-06
  AttachmentSupport = -> [Pocket058]
  ExternalGeometry = -> [Pocket058]
  FullyConstrained = true
  MakeInternals = false
  MapMode = 5
  Placement = pos=(0,0,5) rot=(0,0,1;0rad)
  sketch-geometry (4):
    g0: LineSegment StartX=-5.5 StartY=-27 StartZ=0 EndX=-5.5 EndY=-33 EndZ=0
    g1: LineSegment StartX=-5.5 StartY=-33 StartZ=0 EndX=5.5 EndY=-33 EndZ=0
    g2: LineSegment StartX=5.5 StartY=-33 StartZ=0 EndX=5.5 EndY=-27 EndZ=0
    g3: LineSegment StartX=5.5 StartY=-27 StartZ=0 EndX=-5.5 EndY=-27 EndZ=0
  constraints (11):
    c: Coincident(g0,g1)
    c: Coincident(g1,g2)
    c: Coincident(g2,g3)
    c: Coincident(g3,g0)
    c: Vertical(g0)
    c: Vertical(g2)
    c: Horizontal(g1)
    c: Symmetric(g0,g2,g-2)
    c: Distance(g0,g-3) = 1
    c: DistanceY(g0,g0) = 6
    c: DistanceX(g3,g3) = 11
FEATURE [PartDesign::Pocket] Pocket059
  BaseFeature = -> Pocket058
  Direction = (0,0,-1)
  Length = 21
  Length2 = 5
  Profile = -> Sketch099
  ReferenceAxis = -> Sketch099 [N_Axis]
  Refine = true
  Suppressed = false
  Type = 0
FEATURE [PartDesign::Pocket] Pocket073
  BaseFeature = -> Pocket059
  Direction = (0,0,-1)
  Length = 1
  Length2 = 5
  Profile = -> Pocket059 [Face89]
  Refine = true
  Suppressed = false
  Type = 0
FEATURE [PartDesign::Pad] Pad039
  BaseFeature = -> Pocket073
  Direction = (0,0,1)
  Length = 1
  Length2 = 10
  Profile = -> Pocket073 [Face16]
  Refine = true
  Suppressed = false
  Type = 0
FEATURE [Part::Feature] Part__Feature118  label="Nyloc-nut-M004"
  shape: bbox 3.5 x 3.5 x 0.95 mm, 4 faces (baked)
FEATURE [Part::Feature] Part__Feature117  label="Nyloc-nut-M3"
  shape: bbox 6.35 x 6.35 x 3.86 mm, 32 faces (baked)
FEATURE [Part::Feature] Fusion022  label="hex-m3-30mm"
  shape: bbox 5.5 x 5.5 x 33 mm, 16 faces (baked)
FEATURE [Part::FeaturePython] Clone032  label="Clone of hex-m3-30mm"  # Draft clone (typed FeaturePython)
  Objects = -> [Fusion022]
  Placement = pos=(-89,-37.9,-3) rot=(1,0,0;1.5708rad)
  Scale = (1,1,1)
FEATURE [Part::FeaturePython] Clone033  label="Clone of hex-m3-30mm001"  # Draft clone (typed FeaturePython)
  Objects = -> [Fusion022]
  Placement = pos=(101,37.9,20) rot=(-1,0,0;1.5708rad)
  Scale = (1,1,1)
FEATURE [Part::FeaturePython] Clone034  label="Clone of hex-m3-30mm002"  # Draft clone (typed FeaturePython)
  Objects = -> [Fusion022]
  Placement = pos=(-101,-37.9,20) rot=(1,0,0;1.5708rad)
  Scale = (1,1,1)
FEATURE [Part::FeaturePython] Clone035  label="Clone of hex-m3-30mm003"  # Draft clone (typed FeaturePython)
  Objects = -> [Fusion022]
  Placement = pos=(-89,37.9,-3) rot=(-1,0,0;1.5708rad)
  Scale = (1,1,1)
FEATURE [Part::FeaturePython] Clone036  label="Clone of hex-m3-30mm004"  # Draft clone (typed FeaturePython)
  Objects = -> [Fusion022]
  Placement = pos=(-59,-37.9,30) rot=(1,0,0;1.5708rad)
  Scale = (1,1,1)
FEATURE [Part::FeaturePython] Clone037  label="Clone of hex-m3-30mm005"  # Draft clone (typed FeaturePython)
  Objects = -> [Fusion022]
  Placement = pos=(-59,37.9,30) rot=(-1,0,0;1.5708rad)
  Scale = (1,1,1)
FEATURE [Part::FeaturePython] Clone038  label="Clone of hex-m3-30mm006"  # Draft clone (typed FeaturePython)
  Objects = -> [Fusion022]
  Placement = pos=(59,37.9,30) rot=(-1,0,0;1.5708rad)
  Scale = (1,1,1)
FEATURE [Part::FeaturePython] Clone039  label="Clone of hex-m3-30mm007"  # Draft clone (typed FeaturePython)
  Objects = -> [Fusion022]
  Placement = pos=(89,-37.9,-3) rot=(1,0,0;1.5708rad)
  Scale = (1,1,1)
FEATURE [Part::FeaturePython] Clone040  label="Clone of hex-m3-30mm008"  # Draft clone (typed FeaturePython)
  Objects = -> [Fusion022]
  Placement = pos=(89,37.9,-3) rot=(-1,0,0;1.5708rad)
  Scale = (1,1,1)
FEATURE [Part::FeaturePython] Clone041  label="Clone of hex-m3-30mm009"  # Draft clone (typed FeaturePython)
  Objects = -> [Fusion022]
  Placement = pos=(101,-37.9,20) rot=(1,0,0;1.5708rad)
  Scale = (1,1,1)
FEATURE [Part::FeaturePython] Clone042  label="Clone of hex-m3-30mm010"  # Draft clone (typed FeaturePython)
  Objects = -> [Fusion022]
  Placement = pos=(59,-37.9,30) rot=(1,0,0;1.5708rad)
  Scale = (1,1,1)
FEATURE [Part::FeaturePython] Clone043  label="Clone of hex-m3-30mm011"  # Draft clone (typed FeaturePython)
  Objects = -> [Fusion022]
  Placement = pos=(-101,37.9,20) rot=(-1,0,0;1.5708rad)
  Scale = (1,1,1)
FEATURE [Part::MultiFuse] Fusion  label="m3-nyloc-nut"
  Refine = true
  Shapes = -> [Part__Feature117,Part__Feature118]
FEATURE [Part::FeaturePython] Clone099  label="Clone of m3-nyloc-nut"  # Draft clone (typed FeaturePython)
  Objects = -> [Fusion]
  Placement = pos=(-101,14,20) rot=(0,-0.707107,0.707107;3.14159rad)
  Scale = (1,1,1)
FEATURE [Part::FeaturePython] Clone100  label="Clone of m3-nyloc-nut001"  # Draft clone (typed FeaturePython)
  Objects = -> [Fusion]
  Placement = pos=(-89,14,-3) rot=(0,-0.71,0.71;3.14159rad)
  Scale = (1,1,1)
FEATURE [Part::FeaturePython] Clone101  label="Clone of m3-nyloc-nut002"  # Draft clone (typed FeaturePython)
  Objects = -> [Fusion]
  Placement = pos=(-59,14,30) rot=(0,-0.707107,0.707107;3.14159rad)
  Scale = (1,1,1)
FEATURE [Part::FeaturePython] Clone102  label="Clone of m3-nyloc-nut003"  # Draft clone (typed FeaturePython)
  Objects = -> [Fusion]
  Placement = pos=(101,-14,20) rot=(-1,0,0;1.5708rad)
  Scale = (1,1,1)
FEATURE [Part::FeaturePython] Clone103  label="Clone of m3-nyloc-nut004"  # Draft clone (typed FeaturePython)
  Objects = -> [Fusion]
  Placement = pos=(59,-14,30) rot=(-1,0,0;1.5708rad)
  Scale = (1,1,1)
FEATURE [Part::FeaturePython] Clone104  label="Clone of m3-nyloc-nut005"  # Draft clone (typed FeaturePython)
  Objects = -> [Fusion]
  Placement = pos=(89,14,-3) rot=(0,-0.71,0.71;3.14159rad)
  Scale = (1,1,1)
FEATURE [Part::FeaturePython] Clone105  label="Clone of m3-nyloc-nut006"  # Draft clone (typed FeaturePython)
  Objects = -> [Fusion]
  Placement = pos=(59,14,30) rot=(0,-0.707107,0.707107;3.14159rad)
  Scale = (1,1,1)
FEATURE [Part::FeaturePython] Clone106  label="Clone of m3-nyloc-nut007"  # Draft clone (typed FeaturePython)
  Objects = -> [Fusion]
  Placement = pos=(101,14,20) rot=(0,-0.71,0.71;3.14159rad)
  Scale = (1,1,1)
FEATURE [Part::FeaturePython] Clone107  label="Clone of m3-nyloc-nut008"  # Draft clone (typed FeaturePython)
  Objects = -> [Fusion]
  Placement = pos=(89,-14,-3) rot=(-1,0,0;1.5708rad)
  Scale = (1,1,1)
FEATURE [Part::FeaturePython] Clone108  label="Clone of m3-nyloc-nut009"  # Draft clone (typed FeaturePython)
  Objects = -> [Fusion]
  Placement = pos=(-59,-14,30) rot=(-1,0,0;1.5708rad)
  Scale = (1,1,1)
FEATURE [Part::FeaturePython] Clone109  label="Clone of m3-nyloc-nut010"  # Draft clone (typed FeaturePython)
  Objects = -> [Fusion]
  Placement = pos=(-89,-14,-3) rot=(-1,0,0;1.5708rad)
  Scale = (1,1,1)
FEATURE [Part::FeaturePython] Clone110  label="Clone of m3-nyloc-nut011"  # Draft clone (typed FeaturePython)
  Objects = -> [Fusion]
  Placement = pos=(-101,-14,20) rot=(-1,0,0;1.5708rad)
  Scale = (1,1,1)
FEATURE [Part::FeaturePython] Clone111  label="Clone of m3-nyloc-nut012"  # Draft clone (typed FeaturePython)
  Objects = -> [Fusion]
  Placement = pos=(27.5,0,19.5) rot=(0,-1,0;1.5708rad)
  Scale = (1,1,1)
FEATURE [Part::FeaturePython] Clone112  label="Clone of m3-nyloc-nut013"  # Draft clone (typed FeaturePython)
  Objects = -> [Fusion]
  Placement = pos=(-27.5,0,19.5) rot=(0.707107,0,0.707107;3.14159rad)
  Scale = (1,1,1)
FEATURE [Part::FeaturePython] Clone113  label="Clone of m3-nyloc-nut014"  # Draft clone (typed FeaturePython)
  Objects = -> [Fusion]
  Placement = pos=(23,-23,27) rot=(0.965926,0.258819,0;3.14159rad)
  Scale = (1,1,1)
FEATURE [Part::FeaturePython] Clone114  label="Clone of m3-nyloc-nut015"  # Draft clone (typed FeaturePython)
  Objects = -> [Fusion]
  Placement = pos=(23,23,27) rot=(0.965926,0.258819,0;3.14159rad)
  Scale = (1,1,1)
FEATURE [Part::FeaturePython] Clone115  label="Clone of m3-nyloc-nut016"  # Draft clone (typed FeaturePython)
  Objects = -> [Fusion]
  Placement = pos=(-23,23,27) rot=(0.965926,0.258819,0;3.14159rad)
  Scale = (1,1,1)
FEATURE [Part::FeaturePython] Clone116  label="Clone of m3-nyloc-nut017"  # Draft clone (typed FeaturePython)
  Objects = -> [Fusion]
  Placement = pos=(-23,-23,27) rot=(0.965926,0.258819,0;3.14159rad)
  Scale = (1,1,1)
FEATURE [Part::Feature] Part__Feature119  label="m3-nut"
  Placement = pos=(0,0,0) rot=(0,0,1;0.523599rad)
  shape: bbox 6.35 x 6.35 x 2.4 mm, 29 faces (baked)
FEATURE [Part::FeaturePython] Clone095  label="Clone of m3-nut"  # Draft clone (typed FeaturePython)
  Objects = -> [Part__Feature119]
  Placement = pos=(47,-15.5,7) rot=(0.935113,-0.250563,0.250563;1.63783rad)
  Scale = (1,1,1)
FEATURE [Part::FeaturePython] Clone096  label="Clone of m3-nut001"  # Draft clone (typed FeaturePython)
  Objects = -> [Part__Feature119]
  Placement = pos=(-47,-15.5,7) rot=(0.935113,-0.250563,0.250563;1.63783rad)
  Scale = (1,1,1)
FEATURE [Part::FeaturePython] Clone097  label="Clone of m3-nut002"  # Draft clone (typed FeaturePython)
  Objects = -> [Part__Feature119]
  Placement = pos=(47,17.9,7) rot=(0.935113,-0.250563,0.250563;1.63783rad)
  Scale = (1,1,1)
FEATURE [Part::FeaturePython] Clone098  label="Clone of m3-nut003"  # Draft clone (typed FeaturePython)
  Objects = -> [Part__Feature119]
  Placement = pos=(-47,17.9,7) rot=(0.935113,-0.250563,0.250563;1.63783rad)
  Scale = (1,1,1)
FEATURE [App::DocumentObjectGroup] Group001  label="screws"
  Group = -> [Clone032,Clone033,Clone034,Clone035,Clone036,Clone037,Clone038,Clone039,Clone040,Clone041,Clone042,Clone043,Clone095,Clone096,Clone097,Clone098,Clone099,Clone100,Clone101,Clone102,Clone103,Clone104,Clone105,Clone106,Clone107,Clone108,Clone109,Clone110,Clone111,Clone112,Clone113,Clone114,Clone115,Clone116,Fusion,Part__Feature119]
FEATURE [App::DocumentObjectGroup] Group002  label="third-party"
  Group = -> [Part__Feature116,Fusion022]
FEATURE [Part::FeaturePython] Clone133  label="body-cover001"  # Draft clone (typed FeaturePython)
  AttacherType = Attacher::AttachEngine3D
  Fuse = false
  Objects = -> [Body006]
  Placement = pos=(0,0,1) rot=(0,0,1;0rad)
  Scale = (1,1,1)
FEATURE [Part::FeaturePython] Clone153  label="JST XHP-3 Housing001"  # Draft clone (typed FeaturePython)
  AttacherType = Attacher::AttachEngine3D
  Fuse = false
  Objects = -> [Part__Feature116]
  Placement = pos=(1.25,26,2) rot=(0,-0.71,-0.71;3.14159rad)
  Scale = (1,1,1)
FEATURE [Part::Box] Box001  label="Cube001"
  AttacherType = Attacher::AttachEngine3D
  Height = 10
  Length = 25
  Placement = pos=(-12.5,-26,-3) rot=(0,0,1;0rad)
  Width = 45
FEATURE [Part::Fillet] Fillet031
  Base = -> Box001
  EdgeLinks = -> Box001 [Edge1,Edge2,Edge3,Edge4,Edge5,Edge6,Edge7,Edge8,Edge9,Edge10,Edge11,Edge12]
  Edges = 12 edges r=1: [Edge1,Edge2,Edge3,Edge4,Edge5,Edge6,Edge7,Edge8,Edge9,Edge10,Edge11,Edge12]
FEATURE [Part::Feature] Part__Feature021  label="kame32-pcb_copper"
  shape: bbox 66.6 x 29.6 x 1.58 mm, 2259 faces, 26 solids (baked)
FEATURE [Part::Feature] Part__Feature022  label="kame32-pcb_pad"
  shape: bbox 62.54 x 27.1 x 1.59 mm, 1062 faces, 255 solids (baked)
FEATURE [Part::Feature] Part__Feature023  label="kame32-pcb_PCB001"
  shape: bbox 67.6 x 30.6 x 1.51 mm, 99 faces (baked)
FEATURE [App::Part] kame32_pcb_002  label="pcb"
  Group = -> [Part__Feature021,Part__Feature022,Part__Feature023]
  Origin = -> Origin046
  Placement = pos=(45.7,183.8,10) rot=(0,0,1;4.71239rad)
FEATURE [Part::FeaturePython] Clone154  label="kame32-pcb_copper001"  # Draft clone (typed FeaturePython)
  AttacherType = Attacher::AttachEngine3D
  Fuse = false
  Objects = -> [Part__Feature021]
  Placement = pos=(45.7,183.8,11) rot=(0,0,1;4.71239rad)
  Scale = (1,1,1)
FEATURE [Part::FeaturePython] Clone155  label="kame32-pcb_pad001"  # Draft clone (typed FeaturePython)
  AttacherType = Attacher::AttachEngine3D
  Fuse = false
  Objects = -> [Part__Feature022]
  Placement = pos=(45.7,183.8,11) rot=(0,0,1;4.71239rad)
  Scale = (1,1,1)
FEATURE [Part::FeaturePython] Clone156  label="kame32-pcb_PCB002"  # Draft clone (typed FeaturePython)
  AttacherType = Attacher::AttachEngine3D
  Fuse = false
  Objects = -> [Part__Feature023]
  Placement = pos=(45.7,183.8,11) rot=(0,0,1;4.71239rad)
  Scale = (1,1,1)
FEATURE [Part::FeaturePython] Clone157  label="bracket-sg091"  # Draft clone (typed FeaturePython)
  AttacherType = Attacher::AttachEngine3D
  Fuse = false
  Objects = -> [Body005]
  Placement = pos=(-23,-23,-9) rot=(0,0,1;3.14159rad)
  Scale = (-1,1,1)
FEATURE [Part::FeaturePython] Clone158  label="bracket-sg092"  # Draft clone (typed FeaturePython)
  AttacherType = Attacher::AttachEngine3D
  Fuse = false
  Objects = -> [Body005]
  Placement = pos=(23,-23,-9) rot=(0,0,1;3.14159rad)
  Scale = (1,1,1)
FEATURE [Part::FeaturePython] Clone159  label="bracket-sg093"  # Draft clone (typed FeaturePython)
  AttacherType = Attacher::AttachEngine3D
  Fuse = false
  Objects = -> [Body005]
  Placement = pos=(22.99,23,-9) rot=(0,0,1;0rad)
  Scale = (-1,1,1)
FEATURE [Part::FeaturePython] Clone160  label="bracket-sg094"  # Draft clone (typed FeaturePython)
  AttacherType = Attacher::AttachEngine3D
  Fuse = false
  Objects = -> [Body005]
  Placement = pos=(-23,23,-9) rot=(0,0,1;0rad)
  Scale = (1,1,1)
FEATURE [Part::FeaturePython] Clone161  label="legA001"  # Draft clone (typed FeaturePython)
  AttacherType = Attacher::AttachEngine3D
  Fuse = false
  Objects = -> [Body002]
  Placement = pos=(47,52,8) rot=(0,0,1;3.14159rad)
  Scale = (1,1,1)
FEATURE [Part::FeaturePython] Clone162  label="legA002"  # Draft clone (typed FeaturePython)
  AttacherType = Attacher::AttachEngine3D
  Fuse = false
  Objects = -> [Body002]
  Placement = pos=(-47,0,8) rot=(0,0,1;0rad)
  Scale = (1,1,1)
FEATURE [Part::FeaturePython] Clone163  label="legA003"  # Draft clone (typed FeaturePython)
  AttacherType = Attacher::AttachEngine3D
  Fuse = false
  Objects = -> [Body002]
  Placement = pos=(-47,-52,8) rot=(0,0,1;0rad)
  Scale = (1,1,1)
FEATURE [Part::FeaturePython] Clone164  label="legA004"  # Draft clone (typed FeaturePython)
  AttacherType = Attacher::AttachEngine3D
  Fuse = false
  Objects = -> [Body002]
  Placement = pos=(47,0,8) rot=(0,0,1;3.14159rad)
  Scale = (1,1,1)
FEATURE [Part::FeaturePython] Clone165  label="legB001"  # Draft clone (typed FeaturePython)
  AttacherType = Attacher::AttachEngine3D
  Fuse = false
  Objects = -> [Body001]
  Placement = pos=(47,5,7.5) rot=(0,0,1;0rad)
  Scale = (-1,1,1)
FEATURE [Part::FeaturePython] Clone166  label="legB002"  # Draft clone (typed FeaturePython)
  AttacherType = Attacher::AttachEngine3D
  Fuse = false
  Objects = -> [Body001]
  Placement = pos=(-47,5,7.5) rot=(0,0,1;0rad)
  Scale = (1,1,1)
FEATURE [Part::FeaturePython] Clone167  label="legB003"  # Draft clone (typed FeaturePython)
  AttacherType = Attacher::AttachEngine3D
  Fuse = false
  Objects = -> [Body001]
  Placement = pos=(-47,-5,7.5) rot=(0,0,1;3.14159rad)
  Scale = (-1,1,1)
FEATURE [Part::FeaturePython] Clone168  label="legB004"  # Draft clone (typed FeaturePython)
  AttacherType = Attacher::AttachEngine3D
  Fuse = false
  Objects = -> [Body001]
  Placement = pos=(47,-5,7.5) rot=(0,0,1;3.14159rad)
  Scale = (1,1,1)
FEATURE [Part::FeaturePython] Clone169  label="foot001"  # Draft clone (typed FeaturePython)
  AttacherType = Attacher::AttachEngine3D
  Fuse = false
  Objects = -> [Body003]
  Placement = pos=(47,14,7.5) rot=(0,0,1;3.14159rad)
  Scale = (1,1,1)
FEATURE [Part::FeaturePython] Clone170  label="foot002"  # Draft clone (typed FeaturePython)
  AttacherType = Attacher::AttachEngine3D
  Fuse = false
  Objects = -> [Body003]
  Placement = pos=(-47,-14,7.5) rot=(0,0,1;0rad)
  Scale = (1,1,1)
FEATURE [Part::FeaturePython] Clone171  label="foot003"  # Draft clone (typed FeaturePython)
  AttacherType = Attacher::AttachEngine3D
  Fuse = false
  Objects = -> [Body003]
  Placement = pos=(47,-38,7.5) rot=(0,0,1;3.14159rad)
  Scale = (1,1,1)
FEATURE [Part::FeaturePython] Clone172  label="foot004"  # Draft clone (typed FeaturePython)
  AttacherType = Attacher::AttachEngine3D
  Fuse = false
  Objects = -> [Body003]
  Placement = pos=(-47,38,7.5) rot=(0,0,1;0rad)
  Scale = (1,1,1)
FEATURE [Sketcher::SketchObject] Sketch115
  ArcFitTolerance = 0
  AttachmentSupport = -> [XY_Plane047]
  FullyConstrained = true
  MakeInternals = false
  MapMode = 5
  sketch-geometry (5):
    g0: ArcOfCircle CenterX=0 CenterY=0 CenterZ=0 NormalX=0 NormalY=0 NormalZ=1 AngleXU=0 Radius=9 StartAngle=4.71239 EndAngle=7.5465
    g1: LineSegment StartX=2.72391 StartY=8.5779 StartZ=0 EndX=-17.5 EndY=15 EndZ=0
    g2: LineSegment StartX=-17.5 StartY=15 StartZ=0 EndX=-33 EndY=15 EndZ=0
    g3: LineSegment StartX=-33 StartY=15 StartZ=0 EndX=-33 EndY=-9 EndZ=0
    g4: LineSegment StartX=-33 StartY=-9 StartZ=0 EndX=0 EndY=-9 EndZ=0
  constraints (13):
    c: Coincident(g0,g-1)
    c: Tangent(g0,g1) = -1.5708
    c: Coincident(g1,g2)
    c: Horizontal(g2)
    c: Coincident(g2,g3)
    c: Vertical(g3)
    c: Coincident(g3,g4)
    c: Horizontal(g4)
    c: Tangent(g4,g0) = -1.5708
    c: Radius(g0) = 9
    c: Distance(g3) = 24
    c: Distance(g4) = 33
    c: Distance(g2) = 15.5
FEATURE [PartDesign::Pad] Pad040
  Direction = (0,0,1)
  Length = 43
  Length2 = 10
  Profile = -> Sketch115
  ReferenceAxis = -> Sketch115 [N_Axis]
  Refine = true
  Suppressed = false
  Type = 0
FEATURE [Sketcher::SketchObject] Sketch116
  ArcFitTolerance = 0
  AttachmentSupport = -> [Pad040]
  ExternalGeometry = -> [Pad040]
  FullyConstrained = false
  MakeInternals = false
  MapMode = 5
  Placement = pos=(0,-9,0) rot=(1,0,0;1.5708rad)
  sketch-geometry (5):
    g0: Circle CenterX=-35.9977 CenterY=39 CenterZ=0 NormalX=0 NormalY=0 NormalZ=1 AngleXU=0 Radius=1.5
    g1: ArcOfCircle CenterX=-35.9977 CenterY=39 CenterZ=0 NormalX=0 NormalY=0 NormalZ=1 AngleXU=0 Radius=4 StartAngle=1.57403 EndAngle=3.9468
    g2: LineSegment StartX=-36.0107 StartY=43 StartZ=0 EndX=-33 EndY=43 EndZ=0
    g3: LineSegment StartX=-33 StartY=43 StartZ=0 EndX=-33 EndY=30.3465 EndZ=0
    g4: LineSegment StartX=-38.7696 StartY=36.1161 StartZ=0 EndX=-33 EndY=30.3465 EndZ=0
  constraints (11):
    c: Coincident(g1,g0)
    c: Coincident(g2,g1)
    c: Coincident(g2,g-3)
    c: Horizontal(g2)
    c: Coincident(g3,g2)
    c: Vertical(g3)
    c: Coincident(g4,g1)
    c: Coincident(g4,g3)
    c: Angle(g3,g4) = 0.785398
    c: Radius(g1) = 4
    c: Radius(g0) = 1.5
FEATURE [PartDesign::Pad] Pad041
  BaseFeature = -> Pad040
  Direction = (0,-1,2e-16)
  Length = 24
  Length2 = 10
  Profile = -> Sketch116
  ReferenceAxis = -> Sketch116 [N_Axis]
  Refine = true
  Reversed = true
  Suppressed = false
  Type = 0
FEATURE [Sketcher::SketchObject] Sketch117
  ArcFitTolerance = 0
  AttachmentSupport = -> [Pad041]
  FullyConstrained = true
  MakeInternals = false
  MapMode = 5
  Placement = pos=(0,-9,0) rot=(1,0,0;1.5708rad)
  sketch-geometry (4):
    g0: LineSegment StartX=-18 StartY=4 StartZ=0 EndX=18 EndY=4 EndZ=0
    g1: LineSegment StartX=18 StartY=4 StartZ=0 EndX=18 EndY=39 EndZ=0
    g2: LineSegment StartX=18 StartY=39 StartZ=0 EndX=-18 EndY=39 EndZ=0
    g3: LineSegment StartX=-18 StartY=39 StartZ=0 EndX=-18 EndY=4 EndZ=0
  constraints (12):
    c: Coincident(g0,g1)
    c: Coincident(g1,g2)
    c: Coincident(g2,g3)
    c: Coincident(g3,g0)
    c: Horizontal(g0)
    c: Horizontal(g2)
    c: Vertical(g1)
    c: Vertical(g3)
    c: DistanceX(g-2,g2) = -18
    c: Distance(g3) = 35
    c: DistanceY(g-1,g0) = 4
    c: Distance(g2) = 36
FEATURE [PartDesign::Pocket] Pocket074
  BaseFeature = -> Pad041
  Direction = (0,1,-2e-16)
  Length = 30
  Length2 = 5
  Profile = -> Sketch117
  ReferenceAxis = -> Sketch117 [N_Axis]
  Refine = true
  Suppressed = false
  Type = 0
FEATURE [Sketcher::SketchObject] Sketch118
  ArcFitTolerance = 1e-06
  AttachmentSupport = -> [Pocket074]
  ExternalGeometry = -> [Pocket074]
  FullyConstrained = true
  MakeInternals = false
  MapMode = 5
  Placement = pos=(0,-9,0) rot=(1,0,0;1.5708rad)
  sketch-geometry (1):
    g0: Circle CenterX=-23.9977 CenterY=16 CenterZ=0 NormalX=0 NormalY=0 NormalZ=1 AngleXU=0 Radius=1.5
  constraints (3):
    c: DistanceX(g-3,g0) = 12
    c: DistanceY(g0,g-3) = 23
    c: Radius(g0) = 1.5
FEATURE [PartDesign::Pocket] Pocket075
  BaseFeature = -> Pocket074
  Direction = (0,1,-2e-16)
  Length = 35
  Length2 = 5
  Profile = -> Sketch118
  ReferenceAxis = -> Sketch118 [N_Axis]
  Refine = true
  Suppressed = false
  Type = 0
FEATURE [Sketcher::SketchObject] Sketch119
  ArcFitTolerance = 1e-06
  AttachmentSupport = -> [Pocket075]
  ExternalGeometry = -> [Pocket075]
  FullyConstrained = true
  MakeInternals = false
  MapMode = 5
  Placement = pos=(0,15,0) rot=(0,0.707107,0.707107;3.14159rad)
  sketch-geometry (4):
    g0: LineSegment StartX=18 StartY=33.2 StartZ=0 EndX=18 EndY=9.80002 EndZ=0
    g1: LineSegment StartX=18 StartY=9.80002 StartZ=0 EndX=30.2 EndY=9.80002 EndZ=0
    g2: LineSegment StartX=30.2 StartY=9.80002 StartZ=0 EndX=30.2 EndY=33.2 EndZ=0
    g3: LineSegment StartX=30.2 StartY=33.2 StartZ=0 EndX=18 EndY=33.2 EndZ=0
  constraints (12):
    c: Coincident(g0,g1)
    c: Coincident(g1,g2)
    c: Coincident(g2,g3)
    c: Coincident(g3,g0)
    c: Vertical(g0)
    c: Vertical(g2)
    c: Horizontal(g1)
    c: Horizontal(g3)
    c: PointOnObject(g0,g-3)
    c: Distance(g1) = 12.2
    c: Distance(g2) = 23.4
    c: Distance(g-4,g1) = 6.2
FEATURE [PartDesign::Pocket] Pocket076
  BaseFeature = -> Pocket075
  Direction = (0,-1,2e-16)
  Length = 20
  Length2 = 5
  Profile = -> Sketch119
  ReferenceAxis = -> Sketch119 [N_Axis]
  Refine = true
  Suppressed = false
  Type = 0
FEATURE [Sketcher::SketchObject] Sketch120
  ArcFitTolerance = 1e-06
  AttachmentSupport = -> [Pocket076]
  ExternalGeometry = -> [Pocket076]
  FullyConstrained = true
  MakeInternals = false
  MapMode = 5
  Placement = pos=(0,15,0) rot=(0,0.707107,0.707107;3.14159rad)
  sketch-geometry (6):
    g0: LineSegment StartX=30.2 StartY=37.7 StartZ=0 EndX=30.2 EndY=33.2 EndZ=0
    g1: LineSegment StartX=30.2 StartY=33.2 StartZ=0 EndX=30.2 EndY=9.80002 EndZ=0
    g2: LineSegment StartX=30.2 StartY=9.80002 StartZ=0 EndX=30.2 EndY=5.30002 EndZ=0
    g3: LineSegment StartX=30.2 StartY=5.30002 StartZ=0 EndX=18 EndY=5.30002 EndZ=0
    g4: LineSegment StartX=18 StartY=5.30002 StartZ=0 EndX=18 EndY=37.7 EndZ=0
    g5: LineSegment StartX=18 StartY=37.7 StartZ=0 EndX=30.2 EndY=37.7 EndZ=0
  constraints (16):
    c: Vertical(g0)
    c: Coincident(g0,g1)
    c: Coincident(g1,g2)
    c: Vertical(g2)
    c: Coincident(g2,g3)
    c: Horizontal(g3)
    c: Coincident(g3,g4)
    c: Vertical(g4)
    c: Coincident(g4,g5)
    c: Coincident(g5,g0)
    c: Horizontal(g5)
    c: Equal(g0,g2)
    c: Coincident(g0,g-3)
    c: PointOnObject(g-3,g4)
    c: Distance(g4) = 32.4
    c: Coincident(g-4,g1)
FEATURE [PartDesign::Pocket] Pocket077
  BaseFeature = -> Pocket076
  Direction = (0,-1,2e-16)
  Length = 2
  Length2 = 5
  Profile = -> Sketch120
  ReferenceAxis = -> Sketch120 [N_Axis]
  Refine = true
  Suppressed = false
  Type = 0
FEATURE [Sketcher::SketchObject] Sketch121
  ArcFitTolerance = 1e-06
  AttachmentSupport = -> [Pocket077]
  ExternalGeometry = -> [Pocket077]
  FullyConstrained = true
  MakeInternals = false
  MapMode = 5
  Placement = pos=(0,13,0) rot=(0,0.707107,0.707107;3.14159rad)
  sketch-geometry (5):
    g0: Circle CenterX=23.9977 CenterY=35.5 CenterZ=0 NormalX=0 NormalY=0 NormalZ=1 AngleXU=0 Radius=0.9
    g1: Circle CenterX=23.9977 CenterY=7.50002 CenterZ=0 NormalX=0 NormalY=0 NormalZ=1 AngleXU=0 Radius=0.9
    g2: LineSegment [constr] StartX=23.9977 StartY=7.50002 StartZ=0 EndX=23.9977 EndY=9.80002 EndZ=0
    g3: LineSegment [constr] StartX=23.9977 StartY=9.80002 StartZ=0 EndX=23.9977 EndY=33.2 EndZ=0
    g4: LineSegment [constr] StartX=23.9977 StartY=33.2 StartZ=0 EndX=23.9977 EndY=35.5 EndZ=0
  constraints (14):
    c: Coincident(g2,g1)
    c: PointOnObject(g2,g-4)
    c: Coincident(g3,g2)
    c: PointOnObject(g3,g-3)
    c: Vertical(g3)
    c: Coincident(g4,g3)
    c: Coincident(g4,g0)
    c: Vertical(g4)
    c: Vertical(g2)
    c: Equal(g2,g4)
    c: PointOnObject(g-5,g3)
    c: Distance(g1,g0) = 28
    c: Equal(g1,g0)
    c: Radius(g0) = 0.9
FEATURE [PartDesign::Pocket] Pocket078
  BaseFeature = -> Pocket077
  Direction = (0,-1,2e-16)
  Length = 8
  Length2 = 5
  Profile = -> Sketch121
  ReferenceAxis = -> Sketch121 [N_Axis]
  Refine = true
  Suppressed = false
  Type = 0
FEATURE [Sketcher::SketchObject] Sketch122
  ArcFitTolerance = 1e-06
  AttachmentOffset = pos=(0,0,-5) rot=(0,0,1;0rad)
  AttachmentSupport = -> [Pocket078]
  ExternalGeometry = -> [Pocket078]
  FullyConstrained = true
  MakeInternals = false
  MapMode = 5
  Placement = pos=(0,10,1.1e-15) rot=(0,0.707107,0.707107;3.14159rad)
  sketch-geometry (1):
    g0: Circle CenterX=35.9977 CenterY=39 CenterZ=0 NormalX=0 NormalY=0 NormalZ=1 AngleXU=0 Radius=5
  constraints (2):
    c: Coincident(g0,g-3)
    c: Radius(g0) = 5
FEATURE [PartDesign::Pocket] Pocket079
  BaseFeature = -> Pocket078
  Direction = (0,-1,2e-16)
  Length = 14
  Length2 = 5
  Profile = -> Sketch122
  ReferenceAxis = -> Sketch122 [N_Axis]
  Refine = true
  Suppressed = false
  Type = 0
FEATURE [Sketcher::SketchObject] Sketch123
  ArcFitTolerance = 1e-06
  AttachmentSupport = -> [Pocket079]
  ExternalGeometry = -> [Pocket079]
  FullyConstrained = true
  MakeInternals = false
  MapMode = 5
  Placement = pos=(0,-5,1.1e-15) rot=(0,0.707107,0.707107;3.14159rad)
  sketch-geometry (7):
    g0: LineSegment StartX=22.41 StartY=18.75 StartZ=0 EndX=20.8223 EndY=16 EndZ=0
    g1: LineSegment StartX=20.8223 StartY=16 StartZ=0 EndX=22.41 EndY=13.25 EndZ=0
    g2: LineSegment StartX=22.41 StartY=13.25 StartZ=0 EndX=25.5855 EndY=13.25 EndZ=0
    g3: LineSegment StartX=25.5855 StartY=13.25 StartZ=0 EndX=27.1732 EndY=16 EndZ=0
    g4: LineSegment StartX=27.1732 StartY=16 StartZ=0 EndX=25.5855 EndY=18.75 EndZ=0
    g5: LineSegment StartX=25.5855 StartY=18.75 StartZ=0 EndX=22.41 EndY=18.75 EndZ=0
    g6: Circle [constr] CenterX=23.9977 CenterY=16 CenterZ=0 NormalX=0 NormalY=0 NormalZ=1 AngleXU=0 Radius=3.17543
  constraints (16):
    c: Coincident(g0,g1)
    c: Coincident(g1,g2)
    c: Coincident(g2,g3)
    c: Coincident(g3,g4)
    c: Coincident(g4,g5)
    c: Coincident(g5,g0)
    c: Equal(g0, g1-g5) x5
    c: PointOnObject(g0,g6)
    c: PointOnObject(g1,g6)
    c: PointOnObject(g2,g6)
    c: PointOnObject(g3,g6)
    c: PointOnObject(g4,g6)
    c: PointOnObject(g5,g6)
    c: Coincident(g6,g-3)
    c: Horizontal(g5)
    c: Distance(g0,g1) = 5.5
FEATURE [PartDesign::Pocket] Pocket080
  BaseFeature = -> Pocket079
  Direction = (0,-1,2e-16)
  Length = 2
  Length2 = 5
  Profile = -> Sketch123
  ReferenceAxis = -> Sketch123 [N_Axis]
  Refine = true
  Suppressed = false
  Type = 0
FEATURE [PartDesign::Fillet] Fillet032
  Base = -> Pocket080 [Edge67,Edge64,Edge52,Edge46]
  BaseFeature = -> Pocket080
  Radius = 0.5
  Refine = true
  SupportTransform = false
  Suppressed = false
  UseAllEdges = false
FEATURE [Sketcher::SketchObject] Sketch124
  ArcFitTolerance = 1e-06
  AttachmentSupport = -> [Fillet032]
  ExternalGeometry = -> [Fillet032]
  FullyConstrained = true
  MakeInternals = false
  MapMode = 5
  Placement = pos=(0,0,0) rot=(1,0,0;3.14159rad)
  sketch-geometry (4):
    g0: ArcOfCircle CenterX=-25 CenterY=0.5 CenterZ=0 NormalX=0 NormalY=0 NormalZ=1 AngleXU=0 Radius=2 StartAngle=1.5708 EndAngle=4.71239
    g1: ArcOfCircle CenterX=-18 CenterY=0.5 CenterZ=0 NormalX=0 NormalY=0 NormalZ=1 AngleXU=0 Radius=2 StartAngle=4.71239 EndAngle=7.85398
    g2: LineSegment StartX=-25 StartY=2.5 StartZ=0 EndX=-18 EndY=2.5 EndZ=0
    g3: LineSegment StartX=-25 StartY=-1.5 StartZ=0 EndX=-18 EndY=-1.5 EndZ=0
  constraints (10):
    c: Tangent(g0,g2) = 1.5708
    c: Tangent(g0,g3) = -1.5708
    c: Tangent(g1,g2) = 1.5708
    c: Tangent(g1,g3) = -1.5708
    c: Equal(g0,g1)
    c: Horizontal(g2)
    c: Distance(g0,g-3) = 2.5
    c: Radius(g1) = 2
    c: Distance(g3) = 7
    c: DistanceX(g-2,g0) = -25
FEATURE [PartDesign::Pocket] Pocket081
  BaseFeature = -> Fillet032
  Direction = (0,0,1)
  Length = 10
  Length2 = 5
  Profile = -> Sketch124
  ReferenceAxis = -> Sketch124 [N_Axis]
  Refine = true
  Suppressed = false
  Type = 0
FEATURE [Sketcher::SketchObject] Sketch125
  ArcFitTolerance = 1e-06
  AttachmentSupport = -> [Pocket081]
  FullyConstrained = true
  MakeInternals = false
  MapMode = 5
  Placement = pos=(0,0,0) rot=(1,0,0;3.14159rad)
  sketch-geometry (1):
    g0: Circle CenterX=0 CenterY=0 CenterZ=0 NormalX=0 NormalY=0 NormalZ=1 AngleXU=0 Radius=3.7
  constraints (2):
    c: Coincident(g0,g-1)
    c: Diameter(g0) = 7.4
FEATURE [PartDesign::Pocket] Pocket082
  BaseFeature = -> Pocket081
  Direction = (0,0,1)
  Length = 9
  Length2 = 5
  Profile = -> Sketch125
  ReferenceAxis = -> Sketch125 [N_Axis]
  Refine = true
  Suppressed = false
  Type = 0
FEATURE [Sketcher::SketchObject] Sketch126
  ArcFitTolerance = 1e-06
  AttachmentSupport = -> [Pocket082]
  ExternalGeometry = -> [Pocket082]
  FullyConstrained = true
  MakeInternals = false
  MapMode = 5
  Placement = pos=(0,0,0) rot=(1,0,0;3.14159rad)
  sketch-geometry (7):
    g0: ArcOfCircle CenterX=-12.9863 CenterY=-5.23031 CenterZ=0 NormalX=0 NormalY=0 NormalZ=1 AngleXU=0 Radius=2.1 StartAngle=2.02908 EndAngle=5.01987
    g1: LineSegment StartX=-13.9154 StartY=-3.347 StartZ=0 EndX=-3.12961 EndY=1.97371 EndZ=0
    g2: LineSegment StartX=-12.3507 StartY=-7.23182 StartZ=0 EndX=-0.888052 EndY=-3.59185 EndZ=0
    g3: ArcOfCircle CenterX=0 CenterY=0 CenterZ=0 NormalX=0 NormalY=0 NormalZ=1 AngleXU=0 Radius=3.7 StartAngle=4.47001 EndAngle=8.86212
    g4: LineSegment [constr] StartX=-12.9863 StartY=-5.23031 StartZ=0 EndX=-14.9342 EndY=-6.01485 EndZ=0
    g5: LineSegment [constr] StartX=-12.9863 StartY=-5.23031 StartZ=0 EndX=0 EndY=0 EndZ=0
    g6: LineSegment [constr] StartX=0 StartY=0 StartZ=0 EndX=3.43209 EndY=1.3823 EndZ=0
  constraints (19):
    c: Coincident(g3,g-1)
    c: Tangent(g1,g0) = 1.5708
    c: Tangent(g2,g0) = -1.5708
    c: Coincident(g4,g0)
    c: PointOnObject(g4,g0)
    c: Coincident(g5,g0)
    c: Coincident(g5,g3)
    c: Coincident(g6,g3)
    c: PointOnObject(g6,g3)
    c: Parallel(g6,g5)
    c: Parallel(g5,g4)
    c: Equal(g3,g-3)
    c: Distance(g4,g6) = 19.8
    c: Parallel(g2,g-4)
    c: Equal(g1,g2)
    c: Coincident(g3,g2)
    c: Coincident(g3,g1)
    c: Distance(g1,g2) = 6
    c: Radius(g0) = 2.1
FEATURE [PartDesign::Pocket] Pocket083
  BaseFeature = -> Pocket082
  Direction = (0,0,1)
  Length = 2
  Length2 = 5
  Profile = -> Sketch126
  ReferenceAxis = -> Sketch126 [N_Axis]
  Refine = true
  Suppressed = false
  Type = 0
FEATURE [Sketcher::SketchObject] Sketch127
  ArcFitTolerance = 1e-06
  AttachmentSupport = -> [Pocket083]
  ExternalGeometry = -> [Pocket083]
  FullyConstrained = true
  MakeInternals = false
  MapMode = 5
  Placement = pos=(0,0,43) rot=(0,0,1;0rad)
  sketch-geometry (1):
    g0: Circle CenterX=0 CenterY=0 CenterZ=0 NormalX=0 NormalY=0 NormalZ=1 AngleXU=0 Radius=4.1
  constraints (2):
    c: Coincident(g0,g-1)
    c: Radius(g0) = 4.1
FEATURE [PartDesign::Pocket] Pocket084
  BaseFeature = -> Pocket083
  Direction = (0,0,-1)
  Length = 7
  Length2 = 5
  Profile = -> Sketch127
  ReferenceAxis = -> Sketch127 [N_Axis]
  Refine = true
  Suppressed = false
  Type = 0
FEATURE [Sketcher::SketchObject] Sketch128
  ArcFitTolerance = 1e-06
  AttachmentSupport = -> [Pocket084]
  FullyConstrained = true
  MakeInternals = false
  MapMode = 5
  Placement = pos=(0,0,43) rot=(0,0,1;0rad)
  sketch-geometry (1):
    g0: Circle CenterX=0 CenterY=0 CenterZ=0 NormalX=0 NormalY=0 NormalZ=1 AngleXU=0 Radius=5
  constraints (2):
    c: Coincident(g0,g-1)
    c: Radius(g0) = 5
FEATURE [PartDesign::Pocket] Pocket085
  BaseFeature = -> Pocket084
  Direction = (0,0,-1)
  Length = 2
  Length2 = 5
  Profile = -> Sketch128
  ReferenceAxis = -> Sketch128 [N_Axis]
  Refine = true
  Suppressed = false
  Type = 0
FEATURE [PartDesign::Fillet] Fillet033
  Base = -> Pocket085 [Edge85,Edge45,Edge47,Edge7,Edge14,Edge16,Edge9,Edge11,Edge64,Edge65,Edge51]
  BaseFeature = -> Pocket085
  Radius = 1.5
  Refine = true
  SupportTransform = false
  Suppressed = false
  UseAllEdges = false
FEATURE [Sketcher::SketchObject] Sketch129
  ArcFitTolerance = 1e-06
  AttachmentSupport = -> [Fillet033]
  ExternalGeometry = -> [Fillet033]
  FullyConstrained = true
  MakeInternals = false
  MapMode = 5
  Placement = pos=(0,0,0) rot=(1,0,0;3.14159rad)
  sketch-geometry (4):
    g0: LineSegment StartX=-43 StartY=4 StartZ=0 EndX=-43 EndY=-10 EndZ=0
    g1: LineSegment StartX=-43 StartY=-10 StartZ=0 EndX=-33 EndY=-10 EndZ=0
    g2: LineSegment StartX=-33 StartY=-10 StartZ=0 EndX=-33 EndY=4 EndZ=0
    g3: LineSegment StartX=-33 StartY=4 StartZ=0 EndX=-43 EndY=4 EndZ=0
  constraints (12):
    c: Coincident(g0,g1)
    c: Coincident(g1,g2)
    c: Coincident(g2,g3)
    c: Coincident(g3,g0)
    c: Vertical(g0)
    c: Vertical(g2)
    c: Horizontal(g1)
    c: Horizontal(g3)
    c: PointOnObject(g1,g-3)
    c: PointOnObject(g-4,g1)
    c: PointOnObject(g-4,g3)
    c: Distance(g3) = 10
FEATURE [PartDesign::Pocket] Pocket086
  BaseFeature = -> Fillet033
  Direction = (0,0,1)
  Length = 36
  Length2 = 5
  Profile = -> Sketch129
  ReferenceAxis = -> Sketch129 [N_Axis]
  Refine = true
  Suppressed = false
  Type = 0
FEATURE [PartDesign::Fillet] Fillet034
  Base = -> Pocket086 [Edge209]
  BaseFeature = -> Pocket086
  Radius = 1.5
  Refine = true
  SupportTransform = false
  Suppressed = false
  UseAllEdges = false
FEATURE [PartDesign::Body] Body008  label="bracket-mg90s"
  AllowCompound = false
  Group = -> [Sketch115,Pad040,Sketch116,Pad041,Sketch117,Pocket074,Sketch118,Pocket075,Sketch119,Pocket076,Sketch120,Pocket077,Sketch121,Pocket078,Sketch122,Pocket079,Sketch123,Pocket080,Fillet032,Sketch124,Pocket081,Sketch125,Pocket082,Sketch126,Pocket083,Sketch127,Pocket084,Sketch128,Pocket085,Fillet033,Sketch129,Pocket086,Fillet034]
  Origin = -> Origin047
  Placement = pos=(0,24.1692,20.9304) rot=(1,0,0;1.5708rad)
  Tip = -> Fillet034
FEATURE [Sketcher::SketchObject] Sketch130
  ArcFitTolerance = 0
  AttachmentOffset = pos=(0,-0.5,0) rot=(0,0,1;0rad)
  AttachmentSupport = -> [XZ_Plane048]
  FullyConstrained = true
  MakeInternals = false
  MapMode = 5
  Placement = pos=(0,-1e-16,-0.5) rot=(1,0,0;1.5708rad)
  sketch-geometry (10):
    g0: ArcOfCircle CenterX=-42 CenterY=-10 CenterZ=0 NormalX=0 NormalY=0 NormalZ=1 AngleXU=0 Radius=5.5 StartAngle=1.5708 EndAngle=4.71239
    g1: ArcOfCircle CenterX=0 CenterY=0 CenterZ=0 NormalX=0 NormalY=0 NormalZ=1 AngleXU=0 Radius=8.5 StartAngle=5.03312 EndAngle=8.46485
    g2: LineSegment StartX=-42 StartY=-4.5 StartZ=0 EndX=-21.7189 EndY=-4.5 EndZ=0
    g3: LineSegment StartX=-20.8585 StartY=-4.22873 StartZ=0 EndX=-4.8754 EndY=6.96279 EndZ=0
    g4: LineSegment StartX=2.67968 StartY=-8.06656 StartZ=0 EndX=-17.7782 EndY=-14.8626 EndZ=0
    g5: LineSegment StartX=-21.7189 StartY=-15.5 StartZ=0 EndX=-42 EndY=-15.5 EndZ=0
    g6: Circle CenterX=-42 CenterY=-10 CenterZ=0 NormalX=0 NormalY=0 NormalZ=1 AngleXU=0 Radius=1.7
    g7: Circle CenterX=0 CenterY=0 CenterZ=0 NormalX=0 NormalY=0 NormalZ=1 AngleXU=0 Radius=1.7
    g8: ArcOfCircle CenterX=-21.7189 CenterY=-3 CenterZ=0 NormalX=0 NormalY=0 NormalZ=1 AngleXU=0 Radius=12.5 StartAngle=4.71239 EndAngle=5.03312
    g9: ArcOfCircle CenterX=-21.7189 CenterY=-3 CenterZ=0 NormalX=0 NormalY=0 NormalZ=1 AngleXU=0 Radius=1.5 StartAngle=4.71239 EndAngle=5.32325
  constraints (22):
    c: Tangent(g0,g2) = 1.5708
    c: Tangent(g1,g4) = 1.5708
    c: Horizontal(g5)
    c: Radius(g0) = 5.5
    c: Horizontal(g2)
    c: Tangent(g5,g0) = 1.5708
    c: Coincident(g6,g0)
    c: Radius(g6) = 1.7
    c: Radius(g1) = 8.5
    c: DistanceX(g0,g1) = 42
    c: DistanceY(g0,g1) = 10
    c: Coincident(g7,g1)
    c: Equal(g7,g6)
    c: Tangent(g3,g1) = 1.5708
    c: Coincident(g1,g-1)
    c: Tangent(g8,g5) = 1.5708
    c: Tangent(g8,g4) = 1.5708
    c: Coincident(g9,g8)
    c: Tangent(g9,g3) = -1.5708
    c: Tangent(g9,g2) = -1.5708
    c: Radius(g9) = 1.5
    c: Angle(g3,g2) = 2.53073
FEATURE [PartDesign::Pad] Pad042
  Direction = (0,-1,2e-16)
  Length = 50
  Length2 = 10
  Placement = pos=(0,0,0) rot=(1,0,0;1.5708rad)
  Profile = -> Sketch130
  ReferenceAxis = -> Sketch130 [N_Axis]
  Refine = true
  Reversed = true
  Suppressed = false
  Type = 0
FEATURE [Sketcher::SketchObject] Sketch131
  ArcFitTolerance = 0
  AttachmentSupport = -> [Pad042]
  ExternalGeometry = -> [Pad042]
  FullyConstrained = true
  MakeInternals = false
  MapMode = 5
  Placement = pos=(0,-7e-15,-16) rot=(1,0,0;3.14159rad)
  sketch-geometry (31):
    g0: LineSegment StartX=-54 StartY=-14.25 StartZ=0 EndX=-31.4689 EndY=-14.25 EndZ=0
    g1: LineSegment StartX=-30.8158 StartY=-14.0072 StartZ=0 EndX=-21.7189 EndY=-6.16102 EndZ=0
    g2: LineSegment StartX=-17.25 StartY=-4.5 StartZ=0 EndX=11 EndY=-4.5 EndZ=0
    g3: LineSegment StartX=11 StartY=-4.5 StartZ=0 EndX=11 EndY=-8.5 EndZ=0
    g4: LineSegment StartX=11 StartY=-8.5 StartZ=0 EndX=-17.25 EndY=-8.5 EndZ=0
    g5: LineSegment StartX=-19.1064 StartY=-9.18998 StartZ=0 EndX=-26.6531 EndY=-15.6992 EndZ=0
    g6: LineSegment StartX=-27 StartY=-16.4565 StartZ=0 EndX=-27 EndY=-26.2526 EndZ=0
    g7: LineSegment StartX=-26.8814 StartY=-26.725 StartZ=0 EndX=-18.1933 EndY=-42.9353 EndZ=0
    g8: LineSegment StartX=-17.25 StartY=-43.5 StartZ=0 EndX=11 EndY=-43.5 EndZ=0
    g9: LineSegment StartX=11 StartY=-43.5 StartZ=0 EndX=11 EndY=-47.5 EndZ=0
    g10: LineSegment StartX=11 StartY=-47.5 StartZ=0 EndX=-17.25 EndY=-47.5 EndZ=0
    g11: LineSegment StartX=-21.7189 StartY=-44.8248 StartZ=0 EndX=-30.5875 EndY=-28.2776 EndZ=0
    g12: LineSegment StartX=-31.4689 StartY=-27.75 StartZ=0 EndX=-54 EndY=-27.75 EndZ=0
    g13: LineSegment [constr] StartX=-54 StartY=-27.75 StartZ=0 EndX=-54 EndY=-14.25 EndZ=0
    g14: LineSegment [constr] StartX=11 StartY=-8.5 StartZ=0 EndX=11 EndY=-43.5 EndZ=0
    g15: ArcOfCircle CenterX=-31.4689 CenterY=-13.25 CenterZ=0 NormalX=0 NormalY=0 NormalZ=1 AngleXU=0 Radius=1 StartAngle=4.71239 EndAngle=5.42411
    g16: ArcOfCircle CenterX=-17.25 CenterY=-11.3422 CenterZ=0 NormalX=0 NormalY=0 NormalZ=1 AngleXU=0 Radius=6.84224 StartAngle=1.5708 EndAngle=2.28251
    g17: ArcOfCircle CenterX=-17.25 CenterY=-11.3422 CenterZ=0 NormalX=0 NormalY=0 NormalZ=1 AngleXU=0 Radius=2.84224 StartAngle=1.5708 EndAngle=2.28251
    g18: ArcOfCircle CenterX=-17.25 CenterY=-42.4297 CenterZ=0 NormalX=0 NormalY=0 NormalZ=1 AngleXU=0 Radius=1.0703 StartAngle=3.63359 EndAngle=4.71239
    g19: ArcOfCircle CenterX=-17.25 CenterY=-42.4297 CenterZ=0 NormalX=0 NormalY=0 NormalZ=1 AngleXU=0 Radius=5.0703 StartAngle=3.63359 EndAngle=4.71239
    g20: ArcOfCircle CenterX=-26 CenterY=-16.4565 CenterZ=0 NormalX=0 NormalY=0 NormalZ=1 AngleXU=0 Radius=1 StartAngle=2.28251 EndAngle=3.14159
    g21: ArcOfCircle CenterX=-26 CenterY=-26.2526 CenterZ=0 NormalX=0 NormalY=0 NormalZ=1 AngleXU=0 Radius=1 StartAngle=3.14159 EndAngle=3.63359
    g22: ArcOfCircle CenterX=-31.4689 CenterY=-28.75 CenterZ=0 NormalX=0 NormalY=0 NormalZ=1 AngleXU=0 Radius=1 StartAngle=0.491998 EndAngle=1.5708
    g23: LineSegment StartX=-54 StartY=-14.25 StartZ=0 EndX=-54 EndY=20 EndZ=0
    g24: LineSegment StartX=-54 StartY=20 StartZ=0 EndX=26 EndY=20 EndZ=0
    g25: LineSegment StartX=26 StartY=-60 StartZ=0 EndX=-54 EndY=-60 EndZ=0
    g26: LineSegment StartX=-54 StartY=-60 StartZ=0 EndX=-54 EndY=-27.75 EndZ=0
    g27: LineSegment StartX=26 StartY=20 StartZ=0 EndX=26 EndY=-60 EndZ=0
    g28: LineSegment [constr] StartX=-31.4689 StartY=-14.25 StartZ=0 EndX=-31.4689 EndY=-27.75 EndZ=0
    g29: LineSegment [constr] StartX=-21.7189 StartY=-6.16102 StartZ=0 EndX=-21.7189 EndY=-44.8248 EndZ=0
    g30: LineSegment [constr] StartX=-17.25 StartY=-4.5 StartZ=0 EndX=-17.25 EndY=-47.5 EndZ=0
  constraints (80):
    c: Coincident(g25,g26)
    c: Coincident(g12,g26)
    c: Coincident(g0,g23)
    c: Coincident(g23,g24)
    c: Coincident(g4,g17)
    c: Coincident(g2,g16)
    c: Coincident(g9,g10)
    c: Coincident(g8,g9)
    c: Coincident(g3,g4)
    c: Coincident(g2,g3)
    c: Coincident(g25,g27)
    c: Coincident(g24,g27)
    c: Coincident(g0,g13)
    c: Coincident(g12,g13)
    c: Tangent(g7,g18) = -1.5708
    c: Tangent(g11,g19) = 1.5708
    c: Coincident(g18,g19)
    c: Tangent(g8,g18) = -1.5708
    c: Tangent(g10,g19) = 1.5708
    c: Coincident(g16,g17)
    c: Equal(g9,g3)
    c: Distance(g3) = 4
    c: Horizontal(g2)
    c: Horizontal(g4)
    c: Horizontal(g8)
    c: Horizontal(g10)
    c: Horizontal(g12)
    c: Horizontal(g0)
    c: Horizontal(g24)
    c: Horizontal(g25)
    c: Vertical(g23)
    c: Vertical(g13)
    c: Vertical(g26)
    c: Vertical(g6)
    c: Vertical(g3)
    c: Vertical(g9)
    c: Equal(g15,g20)
    c: Equal(g15,g21)
    c: Equal(g15,g22)
    c: Radius(g15) = 1
    c: Tangent(g12,g22) = -1.5708
    c: Tangent(g11,g22) = -1.5708
    c: Tangent(g7,g21) = -1.5708
    c: Tangent(g6,g21) = -1.5708
    c: Tangent(g5,g20) = -1.5708
    c: Tangent(g6,g20) = -1.5708
    c: Tangent(g1,g15) = -1.5708
    c: Tangent(g0,g15) = -1.5708
    c: Tangent(g5,g17) = -1.5708
    c: Tangent(g1,g16) = 1.5708
    c: Parallel(g1,g5)
    c: Parallel(g7,g11)
    c: Distance(g13) = 13.5
    c: Coincident(g3,g14)
    c: Vertical(g14)
    c: Equal(g25,g27)
    c: Distance(g27) = 80
    c: Vertical(g27)
    c: DistanceX(g-2,g23) = -54
    c: DistanceX(g-2,g2) = 11
    c: Distance(g14) = 35
    c: Coincident(g14,g8)
    c: Coincident(g28,g0)
    c: Coincident(g28,g12)
    c: Vertical(g28)
    c: DistanceY(g-1,g0) = -14.25
    c: DistanceY(g-1,g3) = -8.5
    c: Distance(g6,g27) = 53
    c: DistanceY(g-1,g23) = 20
    c: Coincident(g29,g1)
    c: Coincident(g29,g11)
    c: Vertical(g29)
    c: Coincident(g30,g2)
    c: Coincident(g30,g10)
    c: Vertical(g30)
    c: PointOnObject(g16,g30)
    c: PointOnObject(g4,g30)
    c: PointOnObject(g1,g-3)
    c: DistanceX(g-2,g2) = -17.25
    c: Distance(g0,g29) = 9.75
FEATURE [PartDesign::Pocket] Pocket087
  BaseFeature = -> Pad042
  Direction = (0,0,1)
  Length = 40
  Length2 = 5
  Placement = pos=(0,0,0) rot=(1,0,0;1.5708rad)
  Profile = -> Sketch131
  ReferenceAxis = -> Sketch131 [N_Axis]
  Refine = true
  Suppressed = false
  Type = 0
FEATURE [PartDesign::Fillet] Fillet035
  Base = -> Pocket087 [Edge58,Edge76]
  BaseFeature = -> Pocket087
  Placement = pos=(0,0,0) rot=(1,0,0;1.5708rad)
  Radius = 1.5
  Refine = true
  SupportTransform = false
  Suppressed = false
  UseAllEdges = false
FEATURE [Sketcher::SketchObject] Sketch132
  ArcFitTolerance = 1e-06
  AttachmentSupport = -> [Fillet035]
  ExternalGeometry = -> [Fillet035]
  FullyConstrained = false
  MakeInternals = false
  MapMode = 5
  Placement = pos=(0,14.25,-3.1e-15) rot=(1,0,0;1.5708rad)
  sketch-geometry (2):
    g0: Circle CenterX=-42 CenterY=-10.5 CenterZ=0 NormalX=0 NormalY=0 NormalZ=1 AngleXU=0 Radius=5.5
    g1: Circle CenterX=-42 CenterY=-10.5 CenterZ=0 NormalX=0 NormalY=0 NormalZ=1 AngleXU=0 Radius=1.6
  constraints (3):
    c: Coincident(g0,g-3)
    c: PointOnObject(g-3,g0)
    c: Coincident(g1,g0)
FEATURE [PartDesign::Pad] Pad043
  BaseFeature = -> Fillet035
  Direction = (0,-1,2e-16)
  Length = 13.5
  Length2 = 10
  Placement = pos=(0,0,0) rot=(1,0,0;1.5708rad)
  Profile = -> Sketch132
  ReferenceAxis = -> Sketch132 [N_Axis]
  Refine = true
  Reversed = true
  Suppressed = false
  Type = 0
FEATURE [Sketcher::SketchObject] Sketch133
  ArcFitTolerance = 1e-06
  AttachmentSupport = -> [Pad043]
  ExternalGeometry = -> [Pad043]
  FullyConstrained = true
  MakeInternals = false
  MapMode = 5
  Placement = pos=(0,4.5,-1e-15) rot=(1,0,0;1.5708rad)
  sketch-geometry (1):
    g0: Circle CenterX=0 CenterY=-0.5 CenterZ=0 NormalX=0 NormalY=0 NormalZ=1 AngleXU=0 Radius=4.1
  constraints (2):
    c: Coincident(g0,g-3)
    c: Radius(g0) = 4.1
FEATURE [PartDesign::Pocket] Pocket088
  BaseFeature = -> Pad043
  Direction = (0,1,-2e-16)
  Length = 10
  Length2 = 5
  Placement = pos=(0,0,0) rot=(1,0,0;1.5708rad)
  Profile = -> Sketch133
  ReferenceAxis = -> Sketch133 [N_Axis]
  Refine = true
  Suppressed = false
  Type = 0
FEATURE [Sketcher::SketchObject] Sketch134
  ArcFitTolerance = 1e-06
  AttachmentSupport = -> [Pocket088]
  ExternalGeometry = -> [Pocket088]
  FullyConstrained = true
  MakeInternals = false
  MapMode = 5
  Placement = pos=(0,4.5,-1e-15) rot=(1,0,0;1.5708rad)
  sketch-geometry (1):
    g0: Circle CenterX=0 CenterY=-0.5 CenterZ=0 NormalX=0 NormalY=0 NormalZ=1 AngleXU=0 Radius=5
  constraints (2):
    c: Coincident(g0,g-3)
    c: Radius(g0) = 5
FEATURE [PartDesign::Pocket] Pocket089
  BaseFeature = -> Pocket088
  Direction = (0,1,-2e-16)
  Length = 2
  Length2 = 5
  Placement = pos=(0,0,0) rot=(1,0,0;1.5708rad)
  Profile = -> Sketch134
  ReferenceAxis = -> Sketch134 [N_Axis]
  Refine = true
  Suppressed = false
  Type = 0
FEATURE [Sketcher::SketchObject] Sketch135
  ArcFitTolerance = 1e-06
  AttachmentSupport = -> [Pocket089]
  ExternalGeometry = -> [Pocket089]
  FullyConstrained = true
  MakeInternals = false
  MapMode = 5
  Placement = pos=(0,47.5,-1.04e-14) rot=(-1,0,0;1.5708rad)
  sketch-geometry (1):
    g0: Circle CenterX=0 CenterY=0.5 CenterZ=0 NormalX=0 NormalY=0 NormalZ=1 AngleXU=0 Radius=3.7
  constraints (2):
    c: Coincident(g0,g-3)
    c: Radius(g0) = 3.7
FEATURE [PartDesign::Pocket] Pocket090
  BaseFeature = -> Pocket089
  Direction = (0,-1,-2e-16)
  Length = 7
  Length2 = 5
  Placement = pos=(0,0,0) rot=(1,0,0;1.5708rad)
  Profile = -> Sketch135
  ReferenceAxis = -> Sketch135 [N_Axis]
  Refine = true
  Suppressed = false
  Type = 0
FEATURE [Sketcher::SketchObject] Sketch136
  ArcFitTolerance = 1e-06
  AttachmentSupport = -> [Pocket090]
  ExternalGeometry = -> [Pocket090]
  FullyConstrained = true
  MakeInternals = false
  MapMode = 5
  Placement = pos=(0,47.5,-1.04e-14) rot=(-1,0,0;1.5708rad)
  sketch-geometry (8):
    g0: ArcOfCircle CenterX=-12.5085 CenterY=6.78788 CenterZ=0 NormalX=0 NormalY=0 NormalZ=1 AngleXU=0 Radius=2.1 StartAngle=1.1804 EndAngle=4.17119
    g1: LineSegment [constr] StartX=0 StartY=0.5 StartZ=0 EndX=-12.5085 EndY=6.78788 EndZ=0
    g2: LineSegment [constr] StartX=-12.5085 StartY=6.78788 StartZ=0 EndX=-14.3848 EndY=7.73106 EndZ=0
    g3: ArcOfCircle CenterX=0 CenterY=0.5 CenterZ=0 NormalX=0 NormalY=0 NormalZ=1 AngleXU=0 Radius=3.7 StartAngle=3.62133 EndAngle=8.01345
    g4: LineSegment [constr] StartX=0 StartY=0.5 StartZ=0 EndX=3.30582 EndY=-1.1618 EndZ=0
    g5: LineSegment StartX=-11.7093 StartY=8.72987 StartZ=0 EndX=-0.587521 EndY=4.15306 EndZ=0
    g6: LineSegment StartX=-3.28233 StartY=-1.20773 StartZ=0 EndX=-13.5903 EndY=4.98798 EndZ=0
    g7: Circle [constr] CenterX=-12.5085 CenterY=6.78788 CenterZ=0 NormalX=0 NormalY=0 NormalZ=1 AngleXU=0 Radius=4.97615
  constraints (21):
    c: Coincident(g1,g-3)
    c: Coincident(g1,g0)
    c: Coincident(g2,g0)
    c: PointOnObject(g2,g0)
    c: Coincident(g3,g1)
    c: PointOnObject(g3,g-3)
    c: Coincident(g4,g1)
    c: PointOnObject(g4,g3)
    c: Parallel(g4,g1)
    c: Parallel(g1,g2)
    c: Distance(g2,g4) = 19.8
    c: Radius(g0) = 2.1
    c: Tangent(g6,g0) = 1.5708
    c: Tangent(g5,g0) = 1.5708
    c: Coincident(g7,g0)
    c: Tangent(g7,g-4)
    c: Tangent(g7,g-5)
    c: Coincident(g6,g3)
    c: Coincident(g5,g3)
    c: Equal(g6,g5)
    c: Distance(g3,g3) = 6
FEATURE [PartDesign::Pocket] Pocket091
  BaseFeature = -> Pocket090
  Direction = (0,-1,-2e-16)
  Length = 2
  Length2 = 5
  Placement = pos=(0,0,0) rot=(1,0,0;1.5708rad)
  Profile = -> Sketch136
  ReferenceAxis = -> Sketch136 [N_Axis]
  Refine = true
  Suppressed = false
  Type = 0
FEATURE [PartDesign::Body] Body009  label="leg-mg90s"
  AllowCompound = false
  Group = -> [Sketch130,Pad042,Sketch131,Pocket087,Fillet035,Sketch132,Pad043,Sketch133,Pocket088,Sketch134,Pocket089,Sketch135,Pocket090,Sketch136,Pocket091]
  Origin = -> Origin048
  Tip = -> Pocket091
FEATURE [PartDesign::Pad] Pad044
  BaseFeature = -> Pad039
  Direction = (0,0,1)
  Length = 1
  Length2 = 10
  Profile = -> Pad039 [Face81,Face77,Face16,Face11]
  Refine = true
  Suppressed = false
  Type = 0
FEATURE [PartDesign::Body] Body  label="body-box"
  AllowCompound = false
  Group = -> [Sketch,Pad,Thickness,Fillet,Sketch076,Pad028,Sketch077,Pocket,Fillet017,Sketch078,Pocket044,Sketch079,Pad029,Fillet018,Sketch081,Sketch093,Sketch094,Sketch095,Sketch096,Pocket055,Fillet025,Pad034,Pad035,Pocket056,Pocket057,Fillet026,Sketch097,Pad036,Sketch098,Pocket058,Sketch099,Pocket059,Pocket073,Pad039,Pad044]
  Origin = -> Origin007
  Placement = pos=(0,0,-3.5) rot=(0,0,1;0rad)
  Tip = -> Pad044
FEATURE [Part::FeaturePython] Clone  label="body-box002"  # Draft clone (typed FeaturePython)
  AttacherType = Attacher::AttachEngine3D
  Fuse = false
  Objects = -> [Body]
  Placement = pos=(0,0,-3.5) rot=(0,0,1;0rad)
  Scale = (1,1,1)
FEATURE [App::DocumentObjectGroup] Group003  label="assembly"
  Group = -> [Group001,Pad016,Pad032,Fillet004,Pad018,Fillet005,Pad033,Clone133,Clone153,Clone154,Clone155,Clone156,Clone157,Clone158,Clone159,Clone160,Clone161,Clone162,Clone163,Clone164,Clone165,Clone,Clone166,Clone167,Clone168,Clone169,Clone170,Clone171,Clone172,Fillet031]
FEATURE [Sketcher::SketchObject] Sketch137
  ArcFitTolerance = 1e-06
  AttachmentSupport = -> [XY_Plane]
  FullyConstrained = true
  MakeInternals = false
  MapMode = 5
  sketch-geometry (1):
    g0: Circle CenterX=0 CenterY=0 CenterZ=0 NormalX=0 NormalY=0 NormalZ=1 AngleXU=0 Radius=4.6
  constraints (2):
    c: Coincident(g0,g-1)
    c: Diameter(g0) = 9.2
FEATURE [PartDesign::Pad] Pad045
  Direction = (0,0,1)
  Length = 1.5
  Length2 = 10
  Profile = -> Sketch137
  ReferenceAxis = -> Sketch137 [N_Axis]
  Refine = true
  Suppressed = false
  Type = 0
FEATURE [Sketcher::SketchObject] Sketch138
  ArcFitTolerance = 1e-06
  AttachmentSupport = -> [Pad045]
  FullyConstrained = true
  MakeInternals = false
  MapMode = 5
  Placement = pos=(0,0,0) rot=(1,0,0;3.14159rad)
  sketch-geometry (1):
    g0: Circle CenterX=0 CenterY=0 CenterZ=0 NormalX=0 NormalY=0 NormalZ=1 AngleXU=0 Radius=3.9
  constraints (2):
    c: Coincident(g0,g-1)
    c: Diameter(g0) = 7.8
FEATURE [PartDesign::Pad] Pad046
  BaseFeature = -> Pad045
  Direction = (0,0,-1)
  Length = 4
  Length2 = 10
  Profile = -> Sketch138
  ReferenceAxis = -> Sketch138 [N_Axis]
  Refine = true
  Reversed = true
  Suppressed = false
  Type = 0
FEATURE [Sketcher::SketchObject] Sketch139
  ArcFitTolerance = 1e-06
  AttachmentSupport = -> [Pad046]
  FullyConstrained = true
  MakeInternals = false
  MapMode = 5
  Placement = pos=(0,0,4) rot=(0,0,1;0rad)
  sketch-geometry (1):
    g0: Circle CenterX=0 CenterY=0 CenterZ=0 NormalX=0 NormalY=0 NormalZ=1 AngleXU=0 Radius=1.55
  constraints (2):
    c: Coincident(g0,g-1)
    c: Diameter(g0) = 3.1
FEATURE [PartDesign::Pocket] Pocket092
  BaseFeature = -> Pad046
  Direction = (0,0,-1)
  Length = 13
  Length2 = 5
  Profile = -> Sketch139
  ReferenceAxis = -> Sketch139 [N_Axis]
  Refine = true
  Suppressed = false
  Type = 0
FEATURE [PartDesign::Chamfer] Chamfer003
  Angle = 45
  Base = -> Pocket092 [Edge9,Edge3]
  BaseFeature = -> Pocket092
  ChamferType = 0
  FlipDirection = false
  Refine = true
  Size = 0.2
  Size2 = 1
  SupportTransform = false
  Suppressed = false
  UseAllEdges = false
FEATURE [PartDesign::Body] Body010  label="Body"
  AllowCompound = false
  Group = -> [Sketch137,Pad045,Sketch138,Pad046,Sketch139,Pocket092,Chamfer003]
  Origin = -> Origin
  Tip = -> Chamfer003
FEATURE [App::DocumentObjectGroup] Group  label="src"
  Group = -> [Body001,Body002,Body003,Body005,Body,Body006,kame32_pcb_002,Body008,Body009,Body010]
